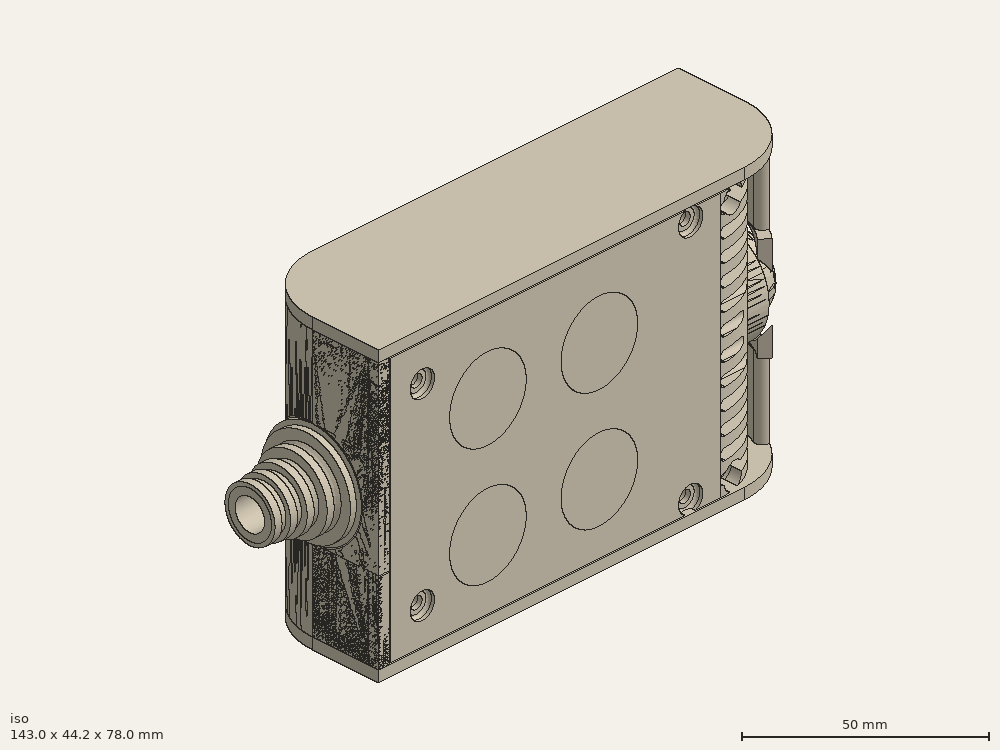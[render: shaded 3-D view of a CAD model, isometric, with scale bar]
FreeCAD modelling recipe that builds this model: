
FCSTD DOCUMENT  (FreeCAD 0.19R0.19.2)
Label: enclosure_142
License: All rights reserved
LicenseURL: http://en.wikipedia.org/wiki/All_rights_reserved
objects: Part::Feature×90, Part::Revolution×90, Part::MultiFuse×76, Sketcher::SketchObject×49, Part::Extrusion×37, Part::Cut×35, Part::Cylinder×34, Part::Fillet×27, Part::Box×22, App::MeasureDistance×4
note: 460 computed .brp shape members not serialized (recipe doc carries the construction recipe); baked Part::Feature solids carry a one-line shape summary decoded from their .brp

FEATURE [Sketcher::SketchObject] Sketch  label="topSketch"
  FullyConstrained = true
  sketch-geometry (20):
    g0: LineSegment StartX=5.21097e-06 StartY=3 StartZ=0 EndX=5.21097e-06 EndY=19 EndZ=0
    g1: ArcOfCircle CenterX=19 CenterY=19 CenterZ=0 NormalX=0 NormalY=0 NormalZ=1 AngleXU=0 Radius=19 StartAngle=1.5708 EndAngle=3.14159
    g2: ArcOfCircle CenterX=19 CenterY=19 CenterZ=0 NormalX=0 NormalY=0 NormalZ=1 AngleXU=0 Radius=16 StartAngle=1.5708 EndAngle=3.14159
    g3: LineSegment StartX=114 StartY=35 StartZ=0 EndX=19 EndY=35 EndZ=0
    g4: LineSegment StartX=5.21097e-06 StartY=3 StartZ=0 EndX=5.21097e-06 EndY=0 EndZ=0
    g5: LineSegment StartX=3 StartY=0 StartZ=0 EndX=5.21097e-06 EndY=0 EndZ=0
    g6: LineSegment StartX=3 StartY=19 StartZ=0 EndX=3 EndY=0 EndZ=0
    g7: LineSegment StartX=19 StartY=38 StartZ=0 EndX=124 EndY=38 EndZ=0
    g8: Circle CenterX=119 CenterY=35 CenterZ=0 NormalX=0 NormalY=0 NormalZ=1 AngleXU=0 Radius=1
    g9: Circle CenterX=121 CenterY=35 CenterZ=0 NormalX=0 NormalY=0 NormalZ=1 AngleXU=0 Radius=1
    g10: Circle CenterX=121 CenterY=33 CenterZ=0 NormalX=0 NormalY=0 NormalZ=1 AngleXU=0 Radius=1
    g11: BSplineCurve PolesCount=3 KnotsCount=2 Degree=2 IsPeriodic=0
    g12: GeomPoint X=119 Y=35 Z=0
    g13: GeomPoint X=121 Y=33 Z=0
    g14: LineSegment StartX=119 StartY=35 StartZ=0 EndX=114 EndY=35 EndZ=0
    g15: ArcOfCircle CenterX=105 CenterY=19 CenterZ=0 NormalX=0 NormalY=0 NormalZ=1 AngleXU=0 Radius=19 StartAngle=5.7297 EndAngle=6.28319
    g16: ArcOfCircle CenterX=105 CenterY=19 CenterZ=0 NormalX=0 NormalY=0 NormalZ=1 AngleXU=0 Radius=16 StartAngle=5.60905 EndAngle=6.28319
    g17: LineSegment StartX=121 StartY=33 StartZ=0 EndX=121 EndY=19 EndZ=0
    g18: LineSegment StartX=124 StartY=38 StartZ=0 EndX=124 EndY=19 EndZ=0
    g19: LineSegment StartX=117.5 StartY=9.01251 StartZ=0 EndX=121.163 EndY=9.0125 EndZ=0
  constraints (46):
    c: Vertical(g0)
    c: Block(g0)
    c: Coincident(g1,g0)
    c: Block(g1)
    c: Coincident(g2,g1)
    c: Block(g2)
    c: Coincident(g3,g2)
    c: Horizontal(g3)
    c: Tangent(g3,g2)
    c: Coincident(g4,g0)
    c: Distance(g4) = 3
    c: Vertical(g4)
    c: Coincident(g5,g4)
    c: Horizontal(g5)
    c: Coincident(g6,g2)
    c: Coincident(g6,g5)
    c: Vertical(g6)
    c: Horizontal(g7)
    c: Distance(g7) = 105
    c: Coincident(g7,g1)
    c: Block(g3)
    c: Weight(g8) = 1
    c: Equal(g8,g9)
    c: Equal(g8,g10)
    c: InternalAlignment(g8,g11)
    c: InternalAlignment(g9,g11)
    c: InternalAlignment(g10,g11)
    c: InternalAlignment(g12,g11)
    c: InternalAlignment(g13,g11)
    c: Block(g11)
    c: Coincident(g14,g11)
    c: Coincident(g14,g3)
    c: Horizontal(g14)
    c: Block(g15)
    c: Coincident(g16,g15)
    c: Block(g16)
    c: Coincident(g17,g11)
    c: Coincident(g17,g16)
    c: Vertical(g17)
    c: Distance(g17) = 14
    c: Coincident(g18,g7)
    c: Coincident(g18,g15)
    c: Vertical(g18)
    c: Distance(g18) = 19
    c: Coincident(g19,g16)
    c: Coincident(g19,g15)
FEATURE [Sketcher::SketchObject] Sketch001  label="bottomSketch"
  FullyConstrained = true
  sketch-geometry (32):
    g0: LineSegment StartX=3.3 StartY=-6.03275e-07 StartZ=0 EndX=98 EndY=-6.03275e-07 EndZ=0
    g1: ArcOfCircle CenterX=98 CenterY=19 CenterZ=0 NormalX=0 NormalY=0 NormalZ=1 AngleXU=0 Radius=19 StartAngle=4.71239 EndAngle=5.71103
    g2: LineSegment StartX=6.3 StartY=8 StartZ=0 EndX=3.3 EndY=8 EndZ=0
    g3: LineSegment StartX=3.3 StartY=8 StartZ=0 EndX=3.3 EndY=-6.03275e-07 EndZ=0
    g4: ArcOfCircle CenterX=8.3 CenterY=5 CenterZ=0 NormalX=0 NormalY=0 NormalZ=1 AngleXU=0 Radius=2 StartAngle=3.14159 EndAngle=4.71239
    g5: LineSegment StartX=6.3 StartY=8 StartZ=0 EndX=6.3 EndY=5 EndZ=0
    g6: ArcOfCircle CenterX=98 CenterY=19 CenterZ=0 NormalX=0 NormalY=0 NormalZ=1 AngleXU=0 Radius=12.7 StartAngle=4.71239 EndAngle=6.28319
    g7: LineSegment StartX=94.7 StartY=3 StartZ=0 EndX=8.3 EndY=3 EndZ=0
    g8-g12: Circle x5 (B-spline internal-alignment scaffolding for g13; pole/knot coordinates omitted)
    g13: BSplineCurve PolesCount=5 KnotsCount=3 Degree=3 IsPeriodic=0
    g14: GeomPoint X=98 Y=6.3 Z=0
    g15: GeomPoint X=96.3938 Y=4.71946 Z=0
    g16: GeomPoint X=94.7 Y=3 Z=0
    g17-g23: Circle x7 (B-spline internal-alignment scaffolding for g24; pole/knot coordinates omitted)
    g24: BSplineCurve PolesCount=7 KnotsCount=5 Degree=3 IsPeriodic=0
    g25-g29: GeomPoint x5 (B-spline internal-alignment scaffolding for g24; pole/knot coordinates omitted)
    g30: ArcOfCircle CenterX=98 CenterY=19 CenterZ=0 NormalX=0 NormalY=0 NormalZ=1 AngleXU=0 Radius=15.7 StartAngle=5.81226 EndAngle=6.28319
    g31: LineSegment StartX=110.7 StartY=19 StartZ=0 EndX=113.7 EndY=19 EndZ=0
  constraints (41):
    c: Horizontal(g0)
    c: Coincident(g1,g0)
    c: Block(g1)
    c: Horizontal(g2)
    c: Distance(g2) = 3
    c: Coincident(g3,g2)
    c: Vertical(g3)
    c: Coincident(g3,g0)
    c: Block(g4)
    c: Block(g2)
    c: Coincident(g5,g2)
    c: Coincident(g5,g4)
    c: Vertical(g5)
    c: Coincident(g6,g1)
    c: Block(g6)
    c: Coincident(g7,g4)
    c: Horizontal(g7)
    c: Block(g0)
    c: Block(g7)
    c: Block(g3)
    c: Coincident(g13,g6)
    c: Weight(g8) = 1
    c: Equal(g8, g9-g12) x4
    c: Coincident(g13,g7)
    c: InternalAlignment(g8-g12 -> g13) x5
    c: InternalAlignment(g14,g13)
    c: InternalAlignment(g15,g13)
    c: InternalAlignment(g16,g13)
    c: Block(g13)
    c: Weight(g17) = 1
    c: Equal(g17, g18-g23) x6
    c: Coincident(g24,g1)
    c: InternalAlignment(g17-g23 -> g24) x7
    c: InternalAlignment(g25-g29 -> g24) x5
    c: Block(g24)
    c: Coincident(g30,g24)
    c: Coincident(g31,g6)
    c: Coincident(g31,g30)
    c: Horizontal(g31)
    c: Block(g31)
    c: Block(g30)
FEATURE [Part::Extrusion] Extrude  label="top"
  Base = -> Sketch
  Dir = (0,0,1)
  DirMode = 2
  FaceMakerClass = Part::FaceMakerBullseye
  LengthFwd = 72
  LengthRev = 0
  Solid = true
  Symmetric = false
FEATURE [Part::Extrusion] Extrude001  label="bottom"
  Base = -> Sketch001
  Dir = (0,0,1)
  DirMode = 2
  FaceMakerClass = Part::FaceMakerBullseye
  LengthFwd = 71.4
  LengthRev = 0
  Placement = pos=(0,0,0.3) rot=(0,0,1;0rad)
  Solid = true
  Symmetric = false
FEATURE [Sketcher::SketchObject] Sketch002  label="topSketch001"
  FullyConstrained = true
  sketch-geometry (6):
    g0: ArcOfCircle CenterX=19 CenterY=19 CenterZ=0 NormalX=0 NormalY=0 NormalZ=1 AngleXU=0 Radius=19 StartAngle=1.5708 EndAngle=3.14159
    g1: LineSegment StartX=5.22862e-06 StartY=19 StartZ=0 EndX=5.22862e-06 EndY=1.19904e-11 EndZ=0
    g2: LineSegment StartX=19 StartY=38 StartZ=0 EndX=124 EndY=38 EndZ=0
    g3: LineSegment StartX=5.22862e-06 StartY=1.19904e-11 StartZ=0 EndX=105 EndY=1.19904e-11 EndZ=0
    g4: ArcOfCircle CenterX=105 CenterY=19 CenterZ=0 NormalX=0 NormalY=0 NormalZ=1 AngleXU=0 Radius=19 StartAngle=4.71239 EndAngle=6.28319
    g5: LineSegment StartX=124 StartY=38 StartZ=0 EndX=124 EndY=19 EndZ=0
  constraints (16):
    c: Block(g0)
    c: Coincident(g1,g0)
    c: Vertical(g1)
    c: Horizontal(g2)
    c: Distance(g2) = 105
    c: Coincident(g2,g0)
    c: Distance(g1) = 19
    c: Coincident(g3,g1)
    c: Horizontal(g3)
    c: Distance(g3) = 105
    c: Block(g4)
    c: Coincident(g4,g3)
    c: Coincident(g5,g2)
    c: Coincident(g5,g4)
    c: Vertical(g5)
    c: Distance(g5) = 19
FEATURE [Part::Extrusion] Extrude002  label="sideA"
  Base = -> Sketch002
  Dir = (0,0,1)
  DirMode = 2
  FaceMakerClass = Part::FaceMakerBullseye
  LengthFwd = 3
  LengthRev = 0
  Placement = pos=(0,0,-3) rot=(0,0,1;0rad)
  Solid = true
  Symmetric = false
FEATURE [Sketcher::SketchObject] Sketch003  label="topSketch002"
  FullyConstrained = true
  sketch-geometry (6):
    g0: LineSegment StartX=19 StartY=38 StartZ=0 EndX=117 EndY=38 EndZ=0
    g1: ArcOfCircle CenterX=19 CenterY=19 CenterZ=0 NormalX=0 NormalY=0 NormalZ=1 AngleXU=0 Radius=19 StartAngle=1.5708 EndAngle=3.14159
    g2: LineSegment StartX=117 StartY=38 StartZ=0 EndX=117 EndY=19 EndZ=0
    g3: LineSegment StartX=98 StartY=1.0161e-12 StartZ=0 EndX=5.22862e-06 EndY=1.0161e-12 EndZ=0
    g4: LineSegment StartX=5.22862e-06 StartY=19 StartZ=0 EndX=5.22862e-06 EndY=1.0161e-12 EndZ=0
    g5: ArcOfCircle CenterX=98 CenterY=19 CenterZ=0 NormalX=0 NormalY=0 NormalZ=1 AngleXU=0 Radius=19 StartAngle=4.71239 EndAngle=6.28319
  constraints (16):
    c: Horizontal(g0)
    c: Distance(g0) = 98
    c: Coincident(g1,g0)
    c: Block(g1)
    c: Coincident(g2,g0)
    c: Vertical(g2)
    c: Distance(g2) = 19
    c: Horizontal(g3)
    c: Coincident(g4,g1)
    c: Vertical(g4)
    c: Coincident(g3,g4)
    c: Block(g3)
    c: Coincident(g5,g2)
    c: Coincident(g5,g3)
    c: Block(g0)
    c: Block(g5)
FEATURE [Sketcher::SketchObject] Sketch004
  FullyConstrained = true
  MapMode = 3
  Placement = pos=(0,0,0) rot=(1,0,0;1.5708rad)
  Support = -> [Extrude]
  sketch-geometry (8):
    g0: Circle CenterX=80.351 CenterY=-67.6202 CenterZ=0 NormalX=0 NormalY=0 NormalZ=1 AngleXU=0 Radius=2
    g1: Circle CenterX=80.351 CenterY=-67.6202 CenterZ=0 NormalX=0 NormalY=0 NormalZ=1 AngleXU=0 Radius=3
    g2: Circle CenterX=80.351 CenterY=-4.92017 CenterZ=0 NormalX=0 NormalY=0 NormalZ=1 AngleXU=0 Radius=2
    g3: Circle CenterX=80.351 CenterY=-4.92017 CenterZ=0 NormalX=0 NormalY=0 NormalZ=1 AngleXU=0 Radius=3
    g4: Circle CenterX=23.851 CenterY=-4.92017 CenterZ=0 NormalX=0 NormalY=0 NormalZ=1 AngleXU=0 Radius=2
    g5: Circle CenterX=23.851 CenterY=-4.92017 CenterZ=0 NormalX=0 NormalY=0 NormalZ=1 AngleXU=0 Radius=3
    g6: Circle CenterX=23.851 CenterY=-67.6202 CenterZ=0 NormalX=0 NormalY=0 NormalZ=1 AngleXU=0 Radius=2
    g7: Circle CenterX=23.851 CenterY=-67.6202 CenterZ=0 NormalX=0 NormalY=0 NormalZ=1 AngleXU=0 Radius=3
  constraints (8):
    c: Block(g3)
    c: Block(g2)
    c: Block(g1)
    c: Block(g0)
    c: Block(g6)
    c: Block(g7)
    c: Block(g4)
    c: Block(g5)
FEATURE [Part::Extrusion] Extrude004
  Base = -> Sketch004
  Dir = (0,-1,2e-16)
  DirMode = 2
  FaceMakerClass = Part::FaceMakerBullseye
  LengthFwd = 6
  LengthRev = 0
  Placement = pos=(0,9,0) rot=(0,0,1;0rad)
  Solid = true
  Symmetric = false
FEATURE [Sketcher::SketchObject] Sketch005
  FullyConstrained = true
  MapMode = 3
  Placement = pos=(0,0,0) rot=(1,0,0;1.5708rad)
  Support = -> [Extrude]
  sketch-geometry (8):
    g0: Circle CenterX=80.351 CenterY=-67.6202 CenterZ=0 NormalX=0 NormalY=0 NormalZ=1 AngleXU=0 Radius=3
    g1: Circle CenterX=80.351 CenterY=-4.92017 CenterZ=0 NormalX=0 NormalY=0 NormalZ=1 AngleXU=0 Radius=3
    g2: Circle CenterX=23.851 CenterY=-4.92017 CenterZ=0 NormalX=0 NormalY=0 NormalZ=1 AngleXU=0 Radius=3
    g3: Circle CenterX=23.851 CenterY=-67.6202 CenterZ=0 NormalX=0 NormalY=0 NormalZ=1 AngleXU=0 Radius=3
    g4: Circle CenterX=23.851 CenterY=-67.6202 CenterZ=0 NormalX=0 NormalY=0 NormalZ=1 AngleXU=0 Radius=5
    g5: Circle CenterX=80.351 CenterY=-67.6202 CenterZ=0 NormalX=0 NormalY=0 NormalZ=1 AngleXU=0 Radius=5
    g6: Circle CenterX=23.851 CenterY=-4.92017 CenterZ=0 NormalX=0 NormalY=0 NormalZ=1 AngleXU=0 Radius=5
    g7: Circle CenterX=80.351 CenterY=-4.92017 CenterZ=0 NormalX=0 NormalY=0 NormalZ=1 AngleXU=0 Radius=5
  constraints (8):
    c: Block(g1)
    c: Block(g0)
    c: Block(g3)
    c: Block(g2)
    c: Block(g5)
    c: Block(g4)
    c: Block(g6)
    c: Block(g7)
FEATURE [Part::Extrusion] Extrude005
  Base = -> Sketch005
  Dir = (0,-1,2e-16)
  DirMode = 2
  FaceMakerClass = Part::FaceMakerBullseye
  LengthFwd = 2
  LengthRev = 0
  Solid = true
  Symmetric = false
FEATURE [Sketcher::SketchObject] Sketch006
  FullyConstrained = true
  MapMode = 3
  Placement = pos=(0,0,0) rot=(1,0,0;1.5708rad)
  sketch-geometry (8):
    g0: Circle CenterX=80.351 CenterY=-67.6202 CenterZ=0 NormalX=0 NormalY=0 NormalZ=1 AngleXU=0 Radius=3
    g1: Circle CenterX=80.351 CenterY=-4.92017 CenterZ=0 NormalX=0 NormalY=0 NormalZ=1 AngleXU=0 Radius=3
    g2: Circle CenterX=23.851 CenterY=-4.92017 CenterZ=0 NormalX=0 NormalY=0 NormalZ=1 AngleXU=0 Radius=3
    g3: Circle CenterX=23.851 CenterY=-67.6202 CenterZ=0 NormalX=0 NormalY=0 NormalZ=1 AngleXU=0 Radius=3
    g4: Circle CenterX=23.851 CenterY=-67.6202 CenterZ=0 NormalX=0 NormalY=0 NormalZ=1 AngleXU=0 Radius=5
    g5: Circle CenterX=80.351 CenterY=-67.6202 CenterZ=0 NormalX=0 NormalY=0 NormalZ=1 AngleXU=0 Radius=5
    g6: Circle CenterX=23.851 CenterY=-4.92017 CenterZ=0 NormalX=0 NormalY=0 NormalZ=1 AngleXU=0 Radius=5
    g7: Circle CenterX=80.351 CenterY=-4.92017 CenterZ=0 NormalX=0 NormalY=0 NormalZ=1 AngleXU=0 Radius=5
  constraints (8):
    c: Block(g1)
    c: Block(g0)
    c: Block(g3)
    c: Block(g2)
    c: Block(g5)
    c: Block(g4)
    c: Block(g6)
    c: Block(g7)
FEATURE [Part::Extrusion] Extrude007
  Base = -> Sketch006
  Dir = (0,-1,2e-16)
  DirMode = 2
  FaceMakerClass = Part::FaceMakerBullseye
  LengthFwd = 2
  LengthRev = 0
  Solid = true
  Symmetric = false
FEATURE [Part::Fillet] Fillet
  Base = -> Extrude007
  Edges = 4 edges r=1.99: [Edge6,Edge12,Edge18,Edge24]
FEATURE [Part::Cut] Cut
  Base = -> Extrude005
  Placement = pos=(0,5,0) rot=(0,0,1;0rad)
  Tool = -> Fillet
FEATURE [Part::MultiFuse] Fusion  label="pCBScrews"
  Placement = pos=(-2.5,0,72.3) rot=(0,0,1;0rad)
  Shapes = -> [Extrude004,Cut]
FEATURE [App::MeasureDistance] Distance  label="Distance: 0.69 mm"
  Distance = 0.685967
  P1 = (24.0138,2.9647,0.3)
  P2 = (23.8901,3,-0.373787)
FEATURE [App::MeasureDistance] Distance001  label="Distance: 0.53 mm"
  Distance = 0.533607
  P1 = (80.2939,3,72.2334)
  P2 = (80.281,2.99661,71.7)
FEATURE [Part::Fillet] Fillet001
  Base = -> Extrude001
  Edges = 1 edges r=2.4: [Edge17]
FEATURE [Part::Fillet] Fillet002  label="bottom001"
  Base = -> Fillet001
  Edges = 1 edges r=2.4: [Edge36]
FEATURE [Part::Fillet] Fillet003  label="top001"
  Base = -> Extrude
  Edges = 1 edges r=2: [Edge1]
FEATURE [Sketcher::SketchObject] Sketch007
  FullyConstrained = true
  sketch-geometry (16):
    g0: LineSegment StartX=4 StartY=0 StartZ=0 EndX=4 EndY=2.4 EndZ=0
    g1: LineSegment StartX=4 StartY=2.4 StartZ=0 EndX=7 EndY=2.4 EndZ=0
    g2: LineSegment StartX=4 StartY=0 StartZ=0 EndX=5.7 EndY=0 EndZ=0
    g3: LineSegment StartX=5.7 StartY=0 StartZ=0 EndX=5.7 EndY=-5.6 EndZ=0
    g4-g8: Circle x5 (B-spline internal-alignment scaffolding for g9; pole/knot coordinates omitted)
    g9: BSplineCurve PolesCount=5 KnotsCount=3 Degree=3 IsPeriodic=0
    g10: GeomPoint X=7 Y=2.4 Z=0
    g11: GeomPoint X=10.4582 Y=-1.55472 Z=0
    g12: GeomPoint X=14 Y=-5.6 Z=0
    g13: LineSegment StartX=14 StartY=-5.6 StartZ=0 EndX=14 EndY=-14.1 EndZ=0
    g14: LineSegment StartX=14 StartY=-14.1 StartZ=0 EndX=6.5 EndY=-14.1 EndZ=0
    g15: LineSegment StartX=5.7 StartY=-5.6 StartZ=0 EndX=6.5 EndY=-14.1 EndZ=0
  constraints (28):
    c: Distance(g0) = 2.4
    c: Vertical(g0)
    c: Block(g0)
    c: Coincident(g1,g0)
    c: Horizontal(g1)
    c: Distance(g1) = 3
    c: Coincident(g2,g0)
    c: Horizontal(g2)
    c: Distance(g2) = 1.7
    c: Coincident(g3,g2)
    c: Vertical(g3)
    c: Distance(g3) = 5.6
    c: Coincident(g9,g1)
    c: Weight(g4) = 1
    c: Equal(g4, g5-g8) x4
    c: InternalAlignment(g4-g8 -> g9) x5
    c: InternalAlignment(g10,g9)
    c: InternalAlignment(g11,g9)
    c: InternalAlignment(g12,g9)
    c: Block(g9)
    c: Coincident(g13,g9)
    c: Vertical(g13)
    c: Distance(g13) = 8.5
    c: Coincident(g14,g13)
    c: Horizontal(g14)
    c: Distance(g14) = 7.5
    c: Coincident(g15,g3)
    c: Coincident(g15,g14)
FEATURE [Part::Feature] Face
  shape: bbox 10 x 16.5 x 2e-07 mm, 1 faces, 0 solids (baked)
FEATURE [Part::Revolution] Revolve  label="plugHousing"
  Angle = 360
  Axis = (0,1,0)
  Base = (0,0,0)
  FaceMakerClass = Part::FaceMakerBullseye
  Placement = pos=(0,0,36.15) rot=(0,0,1;0rad)
  Solid = false
  Source = -> Face
  Symmetric = false
FEATURE [Part::Feature] Face001
  shape: bbox 10 x 16.5 x 2e-07 mm, 1 faces, 0 solids (baked)
FEATURE [Part::Revolution] Revolve001  label="plugHousing001"
  Angle = 360
  Axis = (0,1,0)
  Base = (0,0,0)
  FaceMakerClass = Part::FaceMakerBullseye
  Placement = pos=(0,0,36.15) rot=(0,0,1;0rad)
  Solid = false
  Source = -> Face001
  Symmetric = false
FEATURE [Part::MultiFuse] Fusion001  label="plugHousing002"
  Placement = pos=(0,0,0) rot=(0,0,1;1.5708rad)
  Shapes = -> [Revolve001,Revolve]
FEATURE [Part::Feature] Face002
  shape: bbox 10 x 16.5 x 2e-07 mm, 1 faces, 0 solids (baked)
FEATURE [Part::Revolution] Revolve003  label="plugHousing005"
  Angle = 360
  Axis = (0,1,0)
  Base = (0,0,0)
  FaceMakerClass = Part::FaceMakerBullseye
  Placement = pos=(0,0,36.15) rot=(0,0,1;0rad)
  Solid = false
  Source = -> Face002
  Symmetric = false
FEATURE [Part::Feature] Face003
  shape: bbox 10 x 16.5 x 2e-07 mm, 1 faces, 0 solids (baked)
FEATURE [Part::Revolution] Revolve002  label="plugHousing003"
  Angle = 360
  Axis = (0,1,0)
  Base = (0,0,0)
  FaceMakerClass = Part::FaceMakerBullseye
  Placement = pos=(0,0,36.15) rot=(0,0,1;0rad)
  Solid = false
  Source = -> Face003
  Symmetric = false
FEATURE [Part::MultiFuse] Fusion002  label="plugHousing004"
  Placement = pos=(0,0,0) rot=(0,0,1;1.5708rad)
  Shapes = -> [Revolve002,Revolve003]
FEATURE [Part::MultiFuse] Fusion003  label="plugHousing006"
  Placement = pos=(0,19,0) rot=(0,0,1;3.14159rad)
  Shapes = -> [Fusion002,Fusion001]
FEATURE [Part::Feature] Face004
  shape: bbox 10 x 16.5 x 2e-07 mm, 1 faces, 0 solids (baked)
FEATURE [Part::Revolution] Revolve006  label="plugHousing010"
  Angle = 360
  Axis = (0,1,0)
  Base = (0,0,0)
  FaceMakerClass = Part::FaceMakerBullseye
  Placement = pos=(0,0,36.15) rot=(0,0,1;0rad)
  Solid = false
  Source = -> Face004
  Symmetric = false
FEATURE [Part::Feature] Face005
  shape: bbox 10 x 16.5 x 2e-07 mm, 1 faces, 0 solids (baked)
FEATURE [Part::Revolution] Revolve007  label="plugHousing011"
  Angle = 360
  Axis = (0,1,0)
  Base = (0,0,0)
  FaceMakerClass = Part::FaceMakerBullseye
  Placement = pos=(0,0,36.15) rot=(0,0,1;0rad)
  Solid = false
  Source = -> Face005
  Symmetric = false
FEATURE [Part::Feature] Face006
  shape: bbox 10 x 16.5 x 2e-07 mm, 1 faces, 0 solids (baked)
FEATURE [Part::Revolution] Revolve004  label="plugHousing007"
  Angle = 360
  Axis = (0,1,0)
  Base = (0,0,0)
  FaceMakerClass = Part::FaceMakerBullseye
  Placement = pos=(0,0,36.15) rot=(0,0,1;0rad)
  Solid = false
  Source = -> Face006
  Symmetric = false
FEATURE [Part::MultiFuse] Fusion004  label="plugHousing009"
  Placement = pos=(0,0,0) rot=(0,0,1;1.5708rad)
  Shapes = -> [Revolve004,Revolve007]
FEATURE [Part::Feature] Face007
  shape: bbox 10 x 16.5 x 2e-07 mm, 1 faces, 0 solids (baked)
FEATURE [Part::Revolution] Revolve005  label="plugHousing008"
  Angle = 360
  Axis = (0,1,0)
  Base = (0,0,0)
  FaceMakerClass = Part::FaceMakerBullseye
  Placement = pos=(0,0,36.15) rot=(0,0,1;0rad)
  Solid = false
  Source = -> Face007
  Symmetric = false
FEATURE [Part::MultiFuse] Fusion005  label="plugHousing012"
  Placement = pos=(0,0,0) rot=(0,0,1;1.5708rad)
  Shapes = -> [Revolve006,Revolve005]
FEATURE [Part::MultiFuse] Fusion006  label="plugHousing013"
  Placement = pos=(0,19,0) rot=(0,0,1;3.14159rad)
  Shapes = -> [Fusion005,Fusion004]
FEATURE [Part::MultiFuse] Fusion007  label="plugHousing014"
  Placement = pos=(122.621,0,-0.15) rot=(0,0,1;0rad)
  Shapes = -> [Fusion003,Fusion006]
FEATURE [Part::Cylinder] Cylinder002
  Angle = 360
  AttacherType = Attacher::AttachEngine3D
  Height = 20
  Placement = pos=(0,0,36.15) rot=(0,0,1;0rad)
  Radius = 4
FEATURE [Part::Cylinder] Cylinder003
  Angle = 360
  AttacherType = Attacher::AttachEngine3D
  Height = 10
  Placement = pos=(0,0,36.15) rot=(0,0,1;0rad)
  Radius = 4
FEATURE [Part::MultiFuse] Fusion009  label="removeToCreateHoleForPlugHousing"
  Placement = pos=(70,19,36.15) rot=(0,1,0;1.5708rad)
  Shapes = -> [Cylinder002,Cylinder003]
FEATURE [Part::Cylinder] Cylinder004
  Angle = 360
  AttacherType = Attacher::AttachEngine3D
  Height = 20
  Placement = pos=(0,0,36.15) rot=(0,0,1;0rad)
  Radius = 4
FEATURE [Part::Cylinder] Cylinder005
  Angle = 360
  AttacherType = Attacher::AttachEngine3D
  Height = 10
  Placement = pos=(0,0,36.15) rot=(0,0,1;0rad)
  Radius = 4
FEATURE [Part::MultiFuse] Fusion010  label="removeToCreateHoleForPlugHousing001"
  Placement = pos=(70,19,36.15) rot=(0,1,0;1.5708rad)
  Shapes = -> [Cylinder004,Cylinder005]
FEATURE [Part::Cut] Cut001
  Base = -> Fillet003
  Tool = -> Fusion010
FEATURE [Part::Cut] Cut002  label="Bottom"
  Base = -> Fillet002
  Tool = -> Fusion009
FEATURE [Part::Feature] Face008
  shape: bbox 10 x 16.5 x 2e-07 mm, 1 faces, 0 solids (baked)
FEATURE [Part::Revolution] Revolve011  label="plugHousing021"
  Angle = 360
  Axis = (0,1,0)
  Base = (0,0,0)
  FaceMakerClass = Part::FaceMakerBullseye
  Placement = pos=(0,0,36.15) rot=(0,0,1;0rad)
  Solid = false
  Source = -> Face008
  Symmetric = false
FEATURE [Part::Feature] Face009
  shape: bbox 10 x 16.5 x 2e-07 mm, 1 faces, 0 solids (baked)
FEATURE [Part::Revolution] Revolve012  label="plugHousing022"
  Angle = 360
  Axis = (0,1,0)
  Base = (0,0,0)
  FaceMakerClass = Part::FaceMakerBullseye
  Placement = pos=(0,0,36.15) rot=(0,0,1;0rad)
  Solid = false
  Source = -> Face009
  Symmetric = false
FEATURE [Part::Feature] Face010 .. Face013  x4 (patterned run collapsed; names and placements below)
  shape: bbox 10 x 16.5 x 2e-07 mm, 1 faces, 0 solids (baked)
FEATURE [Part::Revolution] Revolve015  label="plugHousing027"
  Angle = 360
  Axis = (0,1,0)
  Base = (0,0,0)
  FaceMakerClass = Part::FaceMakerBullseye
  Placement = pos=(0,0,36.15) rot=(0,0,1;0rad)
  Solid = false
  Source = -> Face013
  Symmetric = false
FEATURE [Part::Feature] Face014
  shape: bbox 10 x 16.5 x 2e-07 mm, 1 faces, 0 solids (baked)
FEATURE [Part::Feature] Face015
  shape: bbox 10 x 16.5 x 2e-07 mm, 1 faces, 0 solids (baked)
FEATURE [Part::Feature] Face016
  shape: bbox 10 x 16.5 x 2e-07 mm, 1 faces, 0 solids (baked)
FEATURE [Part::Revolution] Revolve019  label="plugHousing033"
  Angle = 360
  Axis = (0,1,0)
  Base = (0,0,0)
  FaceMakerClass = Part::FaceMakerBullseye
  Placement = pos=(0,0,36.15) rot=(0,0,1;0rad)
  Solid = false
  Source = -> Face016
  Symmetric = false
FEATURE [Part::Feature] Face017
  shape: bbox 10 x 16.5 x 2e-07 mm, 1 faces, 0 solids (baked)
FEATURE [Part::Revolution] Revolve020  label="plugHousing034"
  Angle = 360
  Axis = (0,1,0)
  Base = (0,0,0)
  FaceMakerClass = Part::FaceMakerBullseye
  Placement = pos=(0,0,36.15) rot=(0,0,1;0rad)
  Solid = false
  Source = -> Face017
  Symmetric = false
FEATURE [Part::Feature] Face018
  shape: bbox 10 x 16.5 x 2e-07 mm, 1 faces, 0 solids (baked)
FEATURE [Part::Revolution] Revolve016  label="plugHousing030"
  Angle = 360
  Axis = (0,1,0)
  Base = (0,0,0)
  FaceMakerClass = Part::FaceMakerBullseye
  Placement = pos=(0,0,36.15) rot=(0,0,1;0rad)
  Solid = false
  Source = -> Face018
  Symmetric = false
FEATURE [Part::MultiFuse] Fusion020  label="plugHousing038"
  Placement = pos=(0,0,0) rot=(0,0,1;1.5708rad)
  Shapes = -> [Revolve016,Revolve020]
FEATURE [Part::Feature] Face019
  shape: bbox 10 x 16.5 x 2e-07 mm, 1 faces, 0 solids (baked)
FEATURE [Part::Feature] Face020
  shape: bbox 10 x 16.5 x 2e-07 mm, 1 faces, 0 solids (baked)
FEATURE [Part::Revolution] Revolve017  label="plugHousing031"
  Angle = 360
  Axis = (0,1,0)
  Base = (0,0,0)
  FaceMakerClass = Part::FaceMakerBullseye
  Placement = pos=(0,0,36.15) rot=(0,0,1;0rad)
  Solid = false
  Source = -> Face020
  Symmetric = false
FEATURE [Part::MultiFuse] Fusion021  label="plugHousing039"
  Placement = pos=(0,0,0) rot=(0,0,1;1.5708rad)
  Shapes = -> [Revolve019,Revolve017]
FEATURE [Part::MultiFuse] Fusion023  label="plugHousing041"
  Placement = pos=(0,19,0) rot=(0,0,1;3.14159rad)
  Shapes = -> [Fusion021,Fusion020]
FEATURE [Part::Revolution] Revolve022  label="plugHousing043"
  Angle = 360
  Axis = (0,1,0)
  Base = (0,0,0)
  FaceMakerClass = Part::FaceMakerBullseye
  Placement = pos=(0,0,36.15) rot=(0,0,1;0rad)
  Solid = false
  Source = -> Face019
  Symmetric = false
FEATURE [Part::Feature] Face021
  shape: bbox 10 x 16.5 x 2e-07 mm, 1 faces, 0 solids (baked)
FEATURE [Part::Revolution] Revolve023  label="plugHousing044"
  Angle = 360
  Axis = (0,1,0)
  Base = (0,0,0)
  FaceMakerClass = Part::FaceMakerBullseye
  Placement = pos=(0,0,36.15) rot=(0,0,1;0rad)
  Solid = false
  Source = -> Face021
  Symmetric = false
FEATURE [Part::Feature] Face022
  shape: bbox 10 x 16.5 x 2e-07 mm, 1 faces, 0 solids (baked)
FEATURE [Part::Revolution] Revolve018  label="plugHousing032"
  Angle = 360
  Axis = (0,1,0)
  Base = (0,0,0)
  FaceMakerClass = Part::FaceMakerBullseye
  Placement = pos=(0,0,36.15) rot=(0,0,1;0rad)
  Solid = false
  Source = -> Face022
  Symmetric = false
FEATURE [Part::MultiFuse] Fusion022  label="plugHousing040"
  Placement = pos=(0,0,0) rot=(0,0,1;1.5708rad)
  Shapes = -> [Revolve018,Revolve023]
FEATURE [Part::Feature] Face023
  shape: bbox 10 x 16.5 x 2e-07 mm, 1 faces, 0 solids (baked)
FEATURE [Part::Revolution] Revolve021  label="plugHousing035"
  Angle = 360
  Axis = (0,1,0)
  Base = (0,0,0)
  FaceMakerClass = Part::FaceMakerBullseye
  Placement = pos=(0,0,36.15) rot=(0,0,1;0rad)
  Solid = false
  Source = -> Face023
  Symmetric = false
FEATURE [Part::MultiFuse] Fusion018  label="plugHousing036"
  Placement = pos=(0,0,0) rot=(0,0,1;1.5708rad)
  Shapes = -> [Revolve022,Revolve021]
FEATURE [Part::MultiFuse] Fusion019  label="plugHousing037"
  Placement = pos=(0,19,0) rot=(0,0,1;3.14159rad)
  Shapes = -> [Fusion018,Fusion022]
FEATURE [Part::MultiFuse] Fusion024  label="plugHousing042"
  Placement = pos=(122.621,0,-0.15) rot=(0,0,1;0rad)
  Shapes = -> [Fusion023,Fusion019]
FEATURE [Part::Cylinder] Cylinder006
  Angle = 360
  AttacherType = Attacher::AttachEngine3D
  Height = 20
  Placement = pos=(0,0,36.15) rot=(0,0,1;0rad)
  Radius = 14.3
FEATURE [Part::Cylinder] Cylinder007
  Angle = 360
  AttacherType = Attacher::AttachEngine3D
  Height = 10
  Placement = pos=(0,0,36.15) rot=(0,0,1;0rad)
  Radius = 4
FEATURE [Part::MultiFuse] Fusion026  label="removeToCreteHoleForPlugHousing"
  Placement = pos=(70,19,36) rot=(0,1,0;1.5708rad)
  Shapes = -> [Cylinder006,Cylinder007]
FEATURE [Part::Box] Box001  label="Cube001"
  AttacherType = Attacher::AttachEngine3D
  Height = 28
  Length = 3
  Placement = pos=(110.7,19,22) rot=(0,0,1;0rad)
  Width = 15.7
FEATURE [Part::Cut] Cut003  label="top002"
  Base = -> Cut001
  Tool = -> Fusion007
FEATURE [Part::Revolution] Revolve008  label="plugHousing015"
  Angle = 360
  Axis = (0,1,0)
  Base = (0,0,0)
  FaceMakerClass = Part::FaceMakerBullseye
  Placement = pos=(0,0,36.15) rot=(0,0,1;0rad)
  Solid = false
  Source = -> Face010
  Symmetric = false
FEATURE [Part::MultiFuse] Fusion013  label="plugHousing020"
  Placement = pos=(0,0,0) rot=(0,0,1;1.5708rad)
  Shapes = -> [Revolve008,Revolve012]
FEATURE [Part::Cut] Cut004  label="top003"
  Base = -> Cut003
  Placement = pos=(1,0,0) rot=(0,0,1;0rad)
  Tool = -> Fusion026
FEATURE [Part::Cylinder] Cylinder008
  Angle = 360
  AttacherType = Attacher::AttachEngine3D
  Height = 20
  Placement = pos=(0,0,36.15) rot=(0,0,1;0rad)
  Radius = 10.3
FEATURE [Part::Cylinder] Cylinder009
  Angle = 360
  AttacherType = Attacher::AttachEngine3D
  Height = 10
  Placement = pos=(0,0,36.15) rot=(0,0,1;0rad)
  Radius = 4
FEATURE [Part::MultiFuse] Fusion027  label="removeToCreteHoleForPlugHousing001"
  Placement = pos=(70,19,36) rot=(0,1,0;1.5708rad)
  Shapes = -> [Cylinder008,Cylinder009]
FEATURE [Part::Cut] Cut005  label="plugHousingTab"
  Base = -> Box001
  Tool = -> Fusion027
FEATURE [Part::MultiFuse] Fusion028  label="plugHousing045"
  Shapes = -> [Fusion024,Cut005]
FEATURE [Part::Box] Box002  label="Cube002"
  AttacherType = Attacher::AttachEngine3D
  Height = 28.8
  Length = 3
  Placement = pos=(107.3,28,21.6) rot=(0,0,1;0rad)
  Width = 7
FEATURE [Part::Box] Box003  label="Cube003"
  AttacherType = Attacher::AttachEngine3D
  Height = 3
  Length = 6.4
  Placement = pos=(107.3,28,18.6) rot=(0,0,1;0rad)
  Width = 7
FEATURE [Part::Box] Box004  label="Cube004"
  AttacherType = Attacher::AttachEngine3D
  Height = 3
  Length = 6.4
  Placement = pos=(107.3,28,50.4) rot=(0,0,1;0rad)
  Width = 7
FEATURE [Part::MultiFuse] Fusion029  label="plugHousingBracketHolder"
  Shapes = -> [Box004,Box002,Box003]
FEATURE [Part::Cylinder] Cylinder010
  Angle = 360
  AttacherType = Attacher::AttachEngine3D
  Height = 20
  Placement = pos=(0,0,36.15) rot=(0,0,1;0rad)
  Radius = 14.3
FEATURE [Part::Cylinder] Cylinder011
  Angle = 360
  AttacherType = Attacher::AttachEngine3D
  Height = 10
  Placement = pos=(0,0,36.15) rot=(0,0,1;0rad)
  Radius = 4
FEATURE [Part::MultiFuse] Fusion030  label="removeToCreteHoleForPlugHousing002"
  Placement = pos=(70,19,36) rot=(0,1,0;1.5708rad)
  Shapes = -> [Cylinder010,Cylinder011]
FEATURE [Part::Cut] Cut006  label="plugHousingBracketHolder001"
  Base = -> Fusion029
  Tool = -> Fusion030
FEATURE [Part::Cylinder] Cylinder012
  Angle = 360
  AttacherType = Attacher::AttachEngine3D
  Height = 20
  Placement = pos=(0,0,36.15) rot=(0,0,1;0rad)
  Radius = 7
FEATURE [Part::Cylinder] Cylinder013
  Angle = 360
  AttacherType = Attacher::AttachEngine3D
  Height = 10
  Placement = pos=(0,0,36.15) rot=(0,0,1;0rad)
  Radius = 4
FEATURE [Part::MultiFuse] Fusion032  label="removeToCreteHoleForPlugHousing003"
  Placement = pos=(70,19,36) rot=(0,1,0;1.5708rad)
  Shapes = -> [Cylinder012,Cylinder013]
FEATURE [Part::Cut] Cut007  label="bottom002"
  Base = -> Cut002
  Tool = -> Fusion032
FEATURE [Sketcher::SketchObject] Sketch008
  FullyConstrained = true
  sketch-geometry (54):
    g0: LineSegment StartX=-4.2 StartY=0 StartZ=0 EndX=-6.2 EndY=0 EndZ=0
    g1: LineSegment StartX=-14 StartY=-18 StartZ=0 EndX=-14 EndY=-26.5 EndZ=0
    g2: LineSegment StartX=-4.2 StartY=0 StartZ=0 EndX=-4.2 EndY=-13.4877 EndZ=0
    g3: Circle CenterX=-4.2 CenterY=-13.4877 CenterZ=0 NormalX=0 NormalY=0 NormalZ=1 AngleXU=0 Radius=1
    g4: Circle CenterX=-4.2 CenterY=-26.5 CenterZ=0 NormalX=0 NormalY=0 NormalZ=1 AngleXU=0 Radius=1
    g5: Circle CenterX=-8.2 CenterY=-26.5 CenterZ=0 NormalX=0 NormalY=0 NormalZ=1 AngleXU=0 Radius=1
    g6: BSplineCurve PolesCount=3 KnotsCount=2 Degree=2 IsPeriodic=0
    g7: GeomPoint X=-4.2 Y=-13.4877 Z=0
    g8: GeomPoint X=-8.2 Y=-26.5 Z=0
    g9: LineSegment StartX=-14 StartY=-26.5 StartZ=0 EndX=-8.2 EndY=-26.5 EndZ=0
    g10: LineSegment StartX=-10.15 StartY=-12 StartZ=0 EndX=-10.15 EndY=-14 EndZ=0
    g11: LineSegment StartX=-12.8401 StartY=-16 StartZ=0 EndX=-10.1571 EndY=-16 EndZ=0
    g12: LineSegment StartX=-10.15 StartY=-14 StartZ=0 EndX=-8.70761 EndY=-14 EndZ=0
    g13: LineSegment StartX=-12.8401 StartY=-16 StartZ=0 EndX=-12.8401 EndY=-17.6958 EndZ=0
    g14: LineSegment StartX=-10.15 StartY=-12 StartZ=0 EndX=-7.79258 EndY=-12 EndZ=0
    g15: Circle CenterX=-6.2215 CenterY=-2 CenterZ=0 NormalX=0 NormalY=0 NormalZ=1 AngleXU=0 Radius=1
    g16: Circle CenterX=-6.22762 CenterY=-2.58724 CenterZ=0 NormalX=0 NormalY=0 NormalZ=1 AngleXU=0 Radius=1
    g17: Circle CenterX=-6.32538 CenterY=-4 CenterZ=0 NormalX=0 NormalY=0 NormalZ=1 AngleXU=0 Radius=1
    g18: BSplineCurve PolesCount=3 KnotsCount=2 Degree=2 IsPeriodic=0
    g19: GeomPoint X=-6.2215 Y=-2 Z=0
    g20: GeomPoint X=-6.32538 Y=-4 Z=0
    g21: Circle CenterX=-6.48644 CenterY=-5.99526 CenterZ=0 NormalX=0 NormalY=0 NormalZ=1 AngleXU=0 Radius=1
    g22: Circle CenterX=-6.58486 CenterY=-6.99526 CenterZ=0 NormalX=0 NormalY=0 NormalZ=1 AngleXU=0 Radius=1
    g23: Circle CenterX=-6.77343 CenterY=-8 CenterZ=0 NormalX=0 NormalY=0 NormalZ=1 AngleXU=0 Radius=1
    g24: BSplineCurve PolesCount=3 KnotsCount=2 Degree=2 IsPeriodic=0
    g25: GeomPoint X=-6.48644 Y=-5.99526 Z=0
    g26: GeomPoint X=-6.77343 Y=-8 Z=0
    g27: Circle CenterX=-7.19003 CenterY=-10 CenterZ=0 NormalX=0 NormalY=0 NormalZ=1 AngleXU=0 Radius=1
    g28: Circle CenterX=-7.44407 CenterY=-11.0915 CenterZ=0 NormalX=0 NormalY=0 NormalZ=1 AngleXU=0 Radius=1
    g29: Circle CenterX=-7.79258 CenterY=-12 CenterZ=0 NormalX=0 NormalY=0 NormalZ=1 AngleXU=0 Radius=1
    g30: BSplineCurve PolesCount=3 KnotsCount=2 Degree=2 IsPeriodic=0
    g31: GeomPoint X=-7.19003 Y=-10 Z=0
    g32: GeomPoint X=-7.79258 Y=-12 Z=0
    g33: Circle CenterX=-8.70761 CenterY=-14 CenterZ=0 NormalX=0 NormalY=0 NormalZ=1 AngleXU=0 Radius=1
    g34: Circle CenterX=-9.33087 CenterY=-15.1837 CenterZ=0 NormalX=0 NormalY=0 NormalZ=1 AngleXU=0 Radius=1
    g35: Circle CenterX=-10.1571 CenterY=-16 CenterZ=0 NormalX=0 NormalY=0 NormalZ=1 AngleXU=0 Radius=1
    g36: BSplineCurve PolesCount=3 KnotsCount=2 Degree=2 IsPeriodic=0
    g37: GeomPoint X=-8.70761 Y=-14 Z=0
    g38: GeomPoint X=-10.1571 Y=-16 Z=0
    g39: Circle CenterX=-12.8401 CenterY=-17.6958 CenterZ=0 NormalX=0 NormalY=0 NormalZ=1 AngleXU=0 Radius=1
    g40: Circle CenterX=-13.3521 CenterY=-17.9027 CenterZ=0 NormalX=0 NormalY=0 NormalZ=1 AngleXU=0 Radius=1
    g41: Circle CenterX=-14 CenterY=-18 CenterZ=0 NormalX=0 NormalY=0 NormalZ=1 AngleXU=0 Radius=1
    g42: BSplineCurve PolesCount=3 KnotsCount=2 Degree=2 IsPeriodic=0
    g43: GeomPoint X=-12.8401 Y=-17.6958 Z=0
    g44: GeomPoint X=-14 Y=-18 Z=0
    g45: LineSegment StartX=-6.2 StartY=0 StartZ=0 EndX=-7.2 EndY=0 EndZ=0
    g46: LineSegment StartX=-7.2 StartY=0 StartZ=0 EndX=-7.2 EndY=-2 EndZ=0
    g47: LineSegment StartX=-7.2 StartY=-2 StartZ=0 EndX=-6.2215 EndY=-2 EndZ=0
    g48: LineSegment StartX=-6.32538 StartY=-4 StartZ=0 EndX=-7.65538 EndY=-4 EndZ=0
    g49: LineSegment StartX=-7.65538 StartY=-4 StartZ=0 EndX=-7.65538 EndY=-5.99526 EndZ=0
    g50: LineSegment StartX=-7.65538 StartY=-5.99526 StartZ=0 EndX=-6.48644 EndY=-5.99526 EndZ=0
    g51: LineSegment StartX=-6.77343 StartY=-8 StartZ=0 EndX=-8.43343 EndY=-8 EndZ=0
    g52: LineSegment StartX=-8.43343 StartY=-8 StartZ=0 EndX=-8.43343 EndY=-10 EndZ=0
    g53: LineSegment StartX=-8.43343 StartY=-10 StartZ=0 EndX=-7.19003 EndY=-10 EndZ=0
  constraints (112):
    c: Horizontal(g0)
    c: Distance(g0) = 2
    c: Block(g0)
    c: Vertical(g1)
    c: Coincident(g2,g0)
    c: Vertical(g2)
    c: Block(g2)
    c: Coincident(g6,g2)
    c: Weight(g3) = 1
    c: Equal(g3,g4)
    c: Equal(g3,g5)
    c: InternalAlignment(g3,g6)
    c: InternalAlignment(g4,g6)
    c: InternalAlignment(g5,g6)
    c: InternalAlignment(g7,g6)
    c: InternalAlignment(g8,g6)
    c: Block(g6)
    c: Coincident(g9,g1)
    c: Coincident(g9,g6)
    c: Horizontal(g9)
    c: Vertical(g10)
    c: Block(g10)
    c: Horizontal(g11)
    c: Block(g11)
    c: Coincident(g12,g10)
    c: Horizontal(g12)
    c: Block(g12)
    c: Coincident(g13,g11)
    c: Vertical(g13)
    c: Block(g13)
    c: Coincident(g14,g10)
    c: Horizontal(g14)
    c: Block(g14)
    c: Block(g9)
    c: Block(g1)
    c: Weight(g15) = 1
    c: Equal(g15,g16)
    c: Equal(g15,g17)
    c: InternalAlignment(g15,g18)
    c: InternalAlignment(g16,g18)
    c: InternalAlignment(g17,g18)
    c: InternalAlignment(g19,g18)
    c: InternalAlignment(g20,g18)
    c: Weight(g21) = 1
    c: Equal(g21,g22)
    c: Equal(g21,g23)
    c: InternalAlignment(g21,g24)
    c: InternalAlignment(g22,g24)
    c: InternalAlignment(g23,g24)
    c: InternalAlignment(g25,g24)
    c: InternalAlignment(g26,g24)
    c: Weight(g27) = 1
    c: Equal(g27,g28)
    c: Equal(g27,g29)
    c: Coincident(g30,g14)
    c: InternalAlignment(g27,g30)
    c: InternalAlignment(g28,g30)
    c: InternalAlignment(g29,g30)
    c: InternalAlignment(g31,g30)
    c: InternalAlignment(g32,g30)
    c: Coincident(g36,g12)
    c: Weight(g33) = 1
    c: Equal(g33,g34)
    c: Equal(g33,g35)
    c: Coincident(g36,g11)
    c: InternalAlignment(g33,g36)
    c: InternalAlignment(g34,g36)
    c: InternalAlignment(g35,g36)
    c: InternalAlignment(g37,g36)
    c: InternalAlignment(g38,g36)
    c: Coincident(g42,g13)
    c: Weight(g39) = 1
    c: Equal(g39,g40)
    c: Equal(g39,g41)
    c: Coincident(g42,g1)
    c: InternalAlignment(g39,g42)
    c: InternalAlignment(g40,g42)
    c: InternalAlignment(g41,g42)
    c: InternalAlignment(g43,g42)
    c: InternalAlignment(g44,g42)
    c: Block(g18)
    c: Block(g24)
    c: Block(g30)
    c: Block(g36)
    c: Block(g42)
    c: Horizontal(g45)
    c: Coincident(g45,g0)
    c: Vertical(g46)
    c: Coincident(g46,g45)
    c: Coincident(g47,g46)
    c: Coincident(g47,g18)
    c: Horizontal(g47)
    c: Block(g46)
    c: Coincident(g48,g18)
    c: Horizontal(g48)
    c: Distance(g48) = 1.33
    c: Vertical(g49)
    c: Coincident(g49,g48)
    c: Coincident(g50,g49)
    c: Coincident(g50,g24)
    c: Horizontal(g50)
    c: Tangent(g50,g22)
    c: Horizontal(g51)
    c: Coincident(g51,g24)
    c: Block(g51)
    c: Vertical(g52)
    c: Block(g52)
    c: Coincident(g52,g51)
    c: Coincident(g53,g52)
    c: Coincident(g53,g30)
    c: Horizontal(g53)
    c: Distance(g1) = 8.5
FEATURE [Part::Feature] Face024
  shape: bbox 9.8 x 26.5 x 2e-07 mm, 1 faces, 0 solids (baked)
FEATURE [Part::Revolution] Revolve024
  Angle = 360
  Axis = (0,1,0)
  Base = (0,0,0)
  FaceMakerClass = Part::FaceMakerBullseye
  Placement = pos=(0,0,0) rot=(0,0,1;1.5708rad)
  Solid = false
  Source = -> Face024
  Symmetric = false
FEATURE [Part::Feature] Face025
  shape: bbox 9.8 x 26.5 x 2e-07 mm, 1 faces, 0 solids (baked)
FEATURE [Part::Revolution] Revolve025
  Angle = 360
  Axis = (0,1,0)
  Base = (0,0,0)
  FaceMakerClass = Part::FaceMakerBullseye
  Placement = pos=(0,0,0) rot=(0,0,1;1.5708rad)
  Solid = false
  Source = -> Face025
  Symmetric = false
FEATURE [Part::MultiFuse] Fusion033
  Placement = pos=(-18,19,36) rot=(0,0,1;0rad)
  Shapes = -> [Revolve025,Revolve024]
FEATURE [Part::Cylinder] Cylinder014
  Angle = 360
  AttacherType = Attacher::AttachEngine3D
  Height = 20
  Placement = pos=(0,0,36.15) rot=(0,0,1;0rad)
  Radius = 14.3
FEATURE [Part::Cylinder] Cylinder015
  Angle = 360
  AttacherType = Attacher::AttachEngine3D
  Height = 10
  Placement = pos=(0,0,36.15) rot=(0,0,1;0rad)
  Radius = 4
FEATURE [Part::MultiFuse] Fusion034  label="removeToCreteHoleForPlugHousing004"
  Placement = pos=(-42,19,36) rot=(0,1,0;1.5708rad)
  Shapes = -> [Cylinder014,Cylinder015]
FEATURE [Part::Cut] Cut008  label="top004"
  Base = -> Cut004
  Placement = pos=(-1,0,0) rot=(0,0,1;0rad)
  Tool = -> Fusion034
FEATURE [Part::Box] Box005  label="Cube005"
  AttacherType = Attacher::AttachEngine3D
  Height = 28
  Length = 3
  Placement = pos=(110.7,19,22) rot=(0,0,1;0rad)
  Width = 15.7
FEATURE [Part::Cylinder] Cylinder016
  Angle = 360
  AttacherType = Attacher::AttachEngine3D
  Height = 10
  Placement = pos=(0,0,36.15) rot=(0,0,1;0rad)
  Radius = 4
FEATURE [Part::Cylinder] Cylinder017
  Angle = 360
  AttacherType = Attacher::AttachEngine3D
  Height = 20
  Placement = pos=(0,0,36.15) rot=(0,0,1;0rad)
  Radius = 10.3
FEATURE [Part::MultiFuse] Fusion035  label="removeToCreteHoleForPlugHousing005"
  Placement = pos=(70,19,36) rot=(0,1,0;1.5708rad)
  Shapes = -> [Cylinder017,Cylinder016]
FEATURE [Part::Cut] Cut009  label="plugHousingTab001"
  Base = -> Box005
  Placement = pos=(-107.4,-14,0) rot=(0,0,1;0rad)
  Tool = -> Fusion035
FEATURE [Part::Box] Box006  label="Cube006"
  AttacherType = Attacher::AttachEngine3D
  Height = 28
  Length = 3
  Placement = pos=(110.7,19,22) rot=(0,0,1;0rad)
  Width = 15.7
FEATURE [Part::Cylinder] Cylinder018
  Angle = 360
  AttacherType = Attacher::AttachEngine3D
  Height = 10
  Placement = pos=(0,0,36.15) rot=(0,0,1;0rad)
  Radius = 4
FEATURE [Part::Cylinder] Cylinder019
  Angle = 360
  AttacherType = Attacher::AttachEngine3D
  Height = 20
  Placement = pos=(0,0,36.15) rot=(0,0,1;0rad)
  Radius = 10.3
FEATURE [Part::MultiFuse] Fusion036  label="removeToCreteHoleForPlugHousing006"
  Placement = pos=(70,19,36) rot=(0,1,0;1.5708rad)
  Shapes = -> [Cylinder019,Cylinder018]
FEATURE [Part::Cut] Cut010  label="plugHousingTab002"
  Base = -> Box006
  Placement = pos=(-107.4,-14,0) rot=(0,0,1;0rad)
  Tool = -> Fusion036
FEATURE [Part::MultiFuse] Fusion037
  Placement = pos=(9.6,23,0) rot=(0,0,1;3.14159rad)
  Shapes = -> [Cut009,Cut010]
FEATURE [Part::Box] Box  label="Cube"
  AttacherType = Attacher::AttachEngine3D
  Height = 10
  Length = 3
  Placement = pos=(3.3,4,12) rot=(0,0,1;0rad)
  Width = 10
FEATURE [Part::Fillet] Fillet004
  Base = -> Fusion028
  Edges = 1 edges r=2: [Edge25]
FEATURE [Part::Fillet] Fillet005  label="plugHousing046"
  Base = -> Fillet004
  Edges = 1 edges r=2: [Edge8]
FEATURE [Part::Fillet] Fillet006
  Base = -> Box
  Edges = 1 edges r=2: [Edge11]
FEATURE [Part::Box] Box007  label="Cube007"
  AttacherType = Attacher::AttachEngine3D
  Height = 10
  Length = 3
  Placement = pos=(3.3,4,50) rot=(0,0,1;0rad)
  Width = 10
FEATURE [Part::Fillet] Fillet007
  Base = -> Box007
  Edges = 1 edges r=2: [Edge12]
FEATURE [Part::Box] Box008  label="Cube008"
  AttacherType = Attacher::AttachEngine3D
  Height = 28
  Length = 4
  Placement = pos=(5,0,22) rot=(0,0,1;0rad)
  Width = 10
FEATURE [Part::Fillet] Fillet008
  Base = -> Box008
  Edges = 1 edges r=1: [Edge7]
FEATURE [Part::Fillet] Fillet009
  Base = -> Fillet008
  Edges = 1 edges r=2: [Edge5]
FEATURE [Part::Fillet] Fillet010
  Base = -> Fillet009
  Edges = 1 edges r=2: [Edge2]
FEATURE [Sketcher::SketchObject] Sketch009  label="topSketch003"
  FullyConstrained = true
  sketch-geometry (4):
    g0: LineSegment StartX=16.8446 StartY=31.512 StartZ=0 EndX=16.3251 EndY=34.4666 EndZ=0
    g1: ArcOfCircle CenterX=19 CenterY=19.2524 CenterZ=0 NormalX=0 NormalY=0 NormalZ=1 AngleXU=0 Radius=15.4476 StartAngle=1.74483 EndAngle=2.72717
    g2: ArcOfCircle CenterX=19 CenterY=19.2524 CenterZ=0 NormalX=0 NormalY=0 NormalZ=1 AngleXU=0 Radius=12.4476 StartAngle=1.74483 EndAngle=2.73189
    g3: LineSegment StartX=4.86004 StartY=25.4725 StartZ=0 EndX=7.58253 EndY=24.2107 EndZ=0
  constraints (7):
    c: Block(g0)
    c: Coincident(g1,g0)
    c: Coincident(g2,g0)
    c: Coincident(g3,g1)
    c: Coincident(g3,g2)
    c: Block(g1)
    c: Block(g2)
FEATURE [Part::Extrusion] Extrude008
  Base = -> Sketch009
  Dir = (0,0,1)
  DirMode = 2
  FaceMakerClass = Part::FaceMakerBullseye
  LengthFwd = 10
  LengthRev = 0
  Placement = pos=(0,0,31) rot=(0,0,1;0rad)
  Solid = true
  Symmetric = false
FEATURE [Part::Cylinder] Cylinder020
  Angle = 360
  AttacherType = Attacher::AttachEngine3D
  Height = 20
  Placement = pos=(0,0,36.15) rot=(0,0,1;0rad)
  Radius = 8.2
FEATURE [Part::Cylinder] Cylinder021
  Angle = 360
  AttacherType = Attacher::AttachEngine3D
  Height = 10
  Placement = pos=(0,0,36.15) rot=(0,0,1;0rad)
  Radius = 4
FEATURE [Part::MultiFuse] Fusion038  label="removeToCreteHoleForPlugHousing007"
  Placement = pos=(-42,19,36) rot=(0,1,0;1.5708rad)
  Shapes = -> [Cylinder020,Cylinder021]
FEATURE [Part::Cut] Cut011
  Base = -> Extrude008
  Tool = -> Fusion038
FEATURE [Part::Fillet] Fillet011
  Base = -> Cut011
  Edges = 1 edges r=2: [Edge1]
FEATURE [Part::Fillet] Fillet012
  Base = -> Fillet011
  Edges = 1 edges r=2.5: [Edge1]
FEATURE [Part::Fillet] Fillet013
  Base = -> Fillet012
  Edges = 1 edges r=2.5: [Edge2]
FEATURE [Part::Box] Box010  label="Cube010"
  AttacherType = Attacher::AttachEngine3D
  Height = 16
  Length = 8
  Placement = pos=(12.7,31.52,28) rot=(0,0,1;0rad)
  Width = 4
FEATURE [Sketcher::SketchObject] Sketch010  label="topSketch004"
  FullyConstrained = true
  sketch-geometry (4):
    g0: LineSegment StartX=16.8446 StartY=31.512 StartZ=0 EndX=16.3251 EndY=34.4666 EndZ=0
    g1: ArcOfCircle CenterX=19 CenterY=19.2524 CenterZ=0 NormalX=0 NormalY=0 NormalZ=1 AngleXU=0 Radius=15.4476 StartAngle=1.74483 EndAngle=2.72717
    g2: ArcOfCircle CenterX=19 CenterY=19.2524 CenterZ=0 NormalX=0 NormalY=0 NormalZ=1 AngleXU=0 Radius=12.4476 StartAngle=1.74483 EndAngle=2.73189
    g3: LineSegment StartX=4.86004 StartY=25.4725 StartZ=0 EndX=7.58253 EndY=24.2107 EndZ=0
  constraints (7):
    c: Block(g0)
    c: Coincident(g1,g0)
    c: Coincident(g2,g0)
    c: Coincident(g3,g1)
    c: Coincident(g3,g2)
    c: Block(g1)
    c: Block(g2)
FEATURE [Part::Cylinder] Cylinder022
  Angle = 360
  AttacherType = Attacher::AttachEngine3D
  Height = 10
  Placement = pos=(0,0,36.15) rot=(0,0,1;0rad)
  Radius = 4
FEATURE [Sketcher::SketchObject] Sketch011  label="topSketch005"
  FullyConstrained = true
  sketch-geometry (4):
    g0: LineSegment StartX=16.8446 StartY=31.512 StartZ=0 EndX=16.3251 EndY=34.4666 EndZ=0
    g1: ArcOfCircle CenterX=19 CenterY=19.2524 CenterZ=0 NormalX=0 NormalY=0 NormalZ=1 AngleXU=0 Radius=15.4476 StartAngle=1.74483 EndAngle=2.72717
    g2: ArcOfCircle CenterX=19 CenterY=19.2524 CenterZ=0 NormalX=0 NormalY=0 NormalZ=1 AngleXU=0 Radius=12.4476 StartAngle=1.74483 EndAngle=2.73189
    g3: LineSegment StartX=4.86004 StartY=25.4725 StartZ=0 EndX=7.58253 EndY=24.2107 EndZ=0
  constraints (7):
    c: Block(g0)
    c: Coincident(g1,g0)
    c: Coincident(g2,g0)
    c: Coincident(g3,g1)
    c: Coincident(g3,g2)
    c: Block(g1)
    c: Block(g2)
FEATURE [Part::Extrusion] Extrude010
  Base = -> Sketch011
  Dir = (0,0,1)
  DirMode = 2
  FaceMakerClass = Part::FaceMakerBullseye
  LengthFwd = 10.6
  LengthRev = 0
  Placement = pos=(0,0,31) rot=(0,0,1;0rad)
  Solid = true
  Symmetric = false
FEATURE [Part::Cylinder] Cylinder023
  Angle = 360
  AttacherType = Attacher::AttachEngine3D
  Height = 20
  Placement = pos=(0,0,36.15) rot=(0,0,1;0rad)
  Radius = 8.2
FEATURE [Part::MultiFuse] Fusion039  label="removeToCreteHoleForPlugHousing008"
  Placement = pos=(-42,19,36) rot=(0,1,0;1.5708rad)
  Shapes = -> [Cylinder023,Cylinder022]
FEATURE [Part::Cut] Cut012
  Base = -> Extrude010
  Placement = pos=(0,0,-0.3) rot=(0,0,1;0rad)
  Tool = -> Fusion039
FEATURE [Part::Cut] Cut013
  Base = -> Box010
  Tool = -> Cut012
FEATURE [Part::Fillet] Fillet014
  Base = -> Cut013
  Edges = 1 edges r=0.7: [Edge13]
FEATURE [Part::Fillet] Fillet015
  Base = -> Fillet014
  Edges = 1 edges r=0.7: [Edge13]
FEATURE [Part::Fillet] Fillet016
  Base = -> Fillet015
  Edges = 1 edges r=0.7: [Edge16]
FEATURE [Part::Fillet] Fillet017
  Base = -> Fillet016
  Edges = 1 edges r=0.7: [Edge11]
FEATURE [Part::Fillet] Fillet018
  Base = -> Fillet017
  Edges = 1 edges r=0.7: [Edge10]
FEATURE [Part::Fillet] Fillet019
  Base = -> Fillet018
  Edges = 1 edges r=1.2: [Edge5]
FEATURE [Part::Fillet] Fillet020
  Base = -> Fillet019
  Edges = 1 edges r=1.2: [Edge12]
FEATURE [Part::Fillet] Fillet021
  Base = -> Fillet020
  Edges = 1 edges r=2: [Edge1]
  Placement = pos=(0.3,0,0) rot=(0,0,1;0rad)
FEATURE [Part::MultiFuse] Fusion040  label="top005"
  Shapes = -> [Cut008,Fillet021]
FEATURE [Part::MultiFuse] Fusion041  label="wireHolder"
  Shapes = -> [Fusion033,Fillet013]
FEATURE [Part::MultiFuse] Fusion042
  Shapes = -> [Fillet007,Fusion041]
FEATURE [Part::MultiFuse] Fusion043  label="wireHolder001"
  Shapes = -> [Fusion042,Fillet010]
FEATURE [Part::MultiFuse] Fusion044  label="wireHolder002"
  Shapes = -> [Fillet006,Fusion037,Fusion043]
FEATURE [Part::Feature] Face026
  shape: bbox 11 x 6 x 2e-07 mm, 1 faces, 0 solids (baked)
FEATURE [Part::Revolution] Revolve026
  Angle = 360
  Axis = (0,1,0)
  Base = (0,0,0)
  FaceMakerClass = Part::FaceMakerBullseye
  Placement = pos=(30.3,-1,19.7) rot=(0,0,1;0rad)
  Solid = false
  Source = -> Face026
  Symmetric = false
FEATURE [Sketcher::SketchObject] Sketch013  label="topSketch006"
  FullyConstrained = true
  sketch-geometry (13):
    g0: LineSegment StartX=117 StartY=19 StartZ=0 EndX=117 EndY=38 EndZ=0
    g1: ArcOfCircle CenterX=98 CenterY=19 CenterZ=0 NormalX=0 NormalY=0 NormalZ=1 AngleXU=0 Radius=19 StartAngle=5.7297 EndAngle=6.28319
    g2: LineSegment StartX=0 StartY=3 StartZ=0 EndX=0 EndY=19 EndZ=0
    g3: LineSegment StartX=19 StartY=38 StartZ=0 EndX=117 EndY=38 EndZ=0
    g4: ArcOfCircle CenterX=19 CenterY=19 CenterZ=0 NormalX=0 NormalY=0 NormalZ=1 AngleXU=0 Radius=19 StartAngle=1.5708 EndAngle=3.14159
    g5: ArcOfCircle CenterX=19 CenterY=19 CenterZ=0 NormalX=0 NormalY=0 NormalZ=1 AngleXU=0 Radius=16 StartAngle=1.5708 EndAngle=3.14159
    g6: ArcOfCircle CenterX=98 CenterY=19 CenterZ=0 NormalX=0 NormalY=0 NormalZ=1 AngleXU=0 Radius=16 StartAngle=5.60905 EndAngle=6.28319
    g7: LineSegment StartX=114 StartY=19 StartZ=0 EndX=114 EndY=35 EndZ=0
    g8: LineSegment StartX=110.5 StartY=9.01251 StartZ=0 EndX=114.163 EndY=9.01251 EndZ=0
    g9: LineSegment StartX=114 StartY=35 StartZ=0 EndX=19 EndY=35 EndZ=0
    g10: LineSegment StartX=0 StartY=3 StartZ=0 EndX=0 EndY=0 EndZ=0
    g11: LineSegment StartX=3 StartY=0 StartZ=0 EndX=0 EndY=0 EndZ=0
    g12: LineSegment StartX=3 StartY=19 StartZ=0 EndX=3 EndY=0 EndZ=0
  constraints (33):
    c: Vertical(g0)
    c: Distance(g0) = 19
    c: Block(g0)
    c: Coincident(g1,g0)
    c: Block(g1)
    c: Vertical(g2)
    c: Block(g2)
    c: Coincident(g3,g0)
    c: Horizontal(g3)
    c: Distance(g3) = 98
    c: Coincident(g4,g3)
    c: Coincident(g4,g2)
    c: Block(g4)
    c: Coincident(g5,g4)
    c: Coincident(g6,g1)
    c: Block(g6)
    c: Block(g5)
    c: Coincident(g7,g6)
    c: Vertical(g7)
    c: Coincident(g8,g6)
    c: Coincident(g8,g1)
    c: Coincident(g9,g7)
    c: Coincident(g9,g5)
    c: Horizontal(g9)
    c: Tangent(g9,g5)
    c: Coincident(g10,g2)
    c: Distance(g10) = 3
    c: Vertical(g10)
    c: Coincident(g11,g10)
    c: Horizontal(g11)
    c: Coincident(g12,g5)
    c: Coincident(g12,g11)
    c: Vertical(g12)
FEATURE [Part::Extrusion] Extrude011  label="top006"
  Base = -> Sketch013
  Dir = (0,0,1)
  DirMode = 2
  FaceMakerClass = Part::FaceMakerBullseye
  LengthFwd = 72
  LengthRev = 0
  Solid = true
  Symmetric = false
FEATURE [Sketcher::SketchObject] Sketch014
  FullyConstrained = true
  MapMode = 3
  Placement = pos=(0,0,0) rot=(1,0,0;1.5708rad)
  Support = -> [Extrude011]
  sketch-geometry (8):
    g0: Circle CenterX=80.351 CenterY=-67.6202 CenterZ=0 NormalX=0 NormalY=0 NormalZ=1 AngleXU=0 Radius=2
    g1: Circle CenterX=80.351 CenterY=-67.6202 CenterZ=0 NormalX=0 NormalY=0 NormalZ=1 AngleXU=0 Radius=3
    g2: Circle CenterX=80.351 CenterY=-4.92017 CenterZ=0 NormalX=0 NormalY=0 NormalZ=1 AngleXU=0 Radius=2
    g3: Circle CenterX=80.351 CenterY=-4.92017 CenterZ=0 NormalX=0 NormalY=0 NormalZ=1 AngleXU=0 Radius=3
    g4: Circle CenterX=23.851 CenterY=-4.92017 CenterZ=0 NormalX=0 NormalY=0 NormalZ=1 AngleXU=0 Radius=2
    g5: Circle CenterX=23.851 CenterY=-4.92017 CenterZ=0 NormalX=0 NormalY=0 NormalZ=1 AngleXU=0 Radius=3
    g6: Circle CenterX=23.851 CenterY=-67.6202 CenterZ=0 NormalX=0 NormalY=0 NormalZ=1 AngleXU=0 Radius=2
    g7: Circle CenterX=23.851 CenterY=-67.6202 CenterZ=0 NormalX=0 NormalY=0 NormalZ=1 AngleXU=0 Radius=3
  constraints (8):
    c: Block(g3)
    c: Block(g2)
    c: Block(g1)
    c: Block(g0)
    c: Block(g6)
    c: Block(g7)
    c: Block(g4)
    c: Block(g5)
FEATURE [Part::Feature] Face027
  shape: bbox 11 x 6 x 2e-07 mm, 1 faces, 0 solids (baked)
FEATURE [Part::Revolution] Revolve027
  Angle = 360
  Axis = (0,1,0)
  Base = (0,0,0)
  FaceMakerClass = Part::FaceMakerBullseye
  Placement = pos=(30.3,-1,51.7) rot=(0,0,1;0rad)
  Solid = false
  Source = -> Face027
  Symmetric = false
FEATURE [Part::Feature] Face028
  shape: bbox 11 x 6 x 2e-07 mm, 1 faces, 0 solids (baked)
FEATURE [Part::Revolution] Revolve028
  Angle = 360
  Axis = (0,1,0)
  Base = (0,0,0)
  FaceMakerClass = Part::FaceMakerBullseye
  Placement = pos=(62.3,-1,19.7) rot=(0,0,1;0rad)
  Solid = false
  Source = -> Face028
  Symmetric = false
FEATURE [Part::Feature] Face029
  shape: bbox 11 x 6 x 2e-07 mm, 1 faces, 0 solids (baked)
FEATURE [Part::Revolution] Revolve029
  Angle = 360
  Axis = (0,1,0)
  Base = (0,0,0)
  FaceMakerClass = Part::FaceMakerBullseye
  Placement = pos=(62.3,-1,51.7) rot=(0,0,1;0rad)
  Solid = false
  Source = -> Face029
  Symmetric = false
FEATURE [Part::Feature] Wire
  shape: bbox 11 x 5.2 x 2e-07 mm, 0 faces, 0 solids (baked)
FEATURE [Part::Revolution] Revolve030
  Angle = 360
  Axis = (0,1,0)
  Base = (0,0,0)
  FaceMakerClass = Part::FaceMakerBullseye
  Placement = pos=(30.3,38,19.7) rot=(0,0,1;0rad)
  Solid = true
  Source = -> Wire
  Symmetric = false
FEATURE [Part::Feature] Wire001
  shape: bbox 11 x 5.2 x 2e-07 mm, 0 faces, 0 solids (baked)
FEATURE [Part::Revolution] Revolve031
  Angle = 360
  Axis = (0,1,0)
  Base = (0,0,0)
  FaceMakerClass = Part::FaceMakerBullseye
  Placement = pos=(30.3,38,51.7) rot=(0,0,1;0rad)
  Solid = true
  Source = -> Wire001
  Symmetric = false
FEATURE [Part::Feature] Wire002
  shape: bbox 11 x 5.2 x 2e-07 mm, 0 faces, 0 solids (baked)
FEATURE [Part::Revolution] Revolve032
  Angle = 360
  Axis = (0,1,0)
  Base = (0,0,0)
  FaceMakerClass = Part::FaceMakerBullseye
  Placement = pos=(62.3,38,51.7) rot=(0,0,1;0rad)
  Solid = true
  Source = -> Wire002
  Symmetric = false
FEATURE [Part::Feature] Wire003
  shape: bbox 11 x 5.2 x 2e-07 mm, 0 faces, 0 solids (baked)
FEATURE [Part::Revolution] Revolve033
  Angle = 360
  Axis = (0,1,0)
  Base = (0,0,0)
  FaceMakerClass = Part::FaceMakerBullseye
  Placement = pos=(62.3,38,19.7) rot=(0,0,1;0rad)
  Solid = true
  Source = -> Wire003
  Symmetric = false
FEATURE [Part::MultiFuse] Fusion045  label="altRandScrewHousing"
  Shapes = -> [Revolve029,Revolve027,Revolve028,Revolve026]
FEATURE [Part::MultiFuse] Fusion046  label="fanScrewHousing"
  Shapes = -> [Revolve033,Revolve032,Revolve031,Revolve030]
FEATURE [Sketcher::SketchObject] Sketch015
  FullyConstrained = true
  sketch-geometry (17):
    g0: Circle CenterX=-3.5 CenterY=23.5 CenterZ=0 NormalX=0 NormalY=0 NormalZ=1 AngleXU=0 Radius=1
    g1: Circle CenterX=-1 CenterY=15.25 CenterZ=0 NormalX=0 NormalY=0 NormalZ=1 AngleXU=0 Radius=1
    g2: Circle CenterX=-3.5 CenterY=7 CenterZ=0 NormalX=0 NormalY=0 NormalZ=1 AngleXU=0 Radius=1
    g3: BSplineCurve PolesCount=3 KnotsCount=2 Degree=2 IsPeriodic=0
    g4: GeomPoint X=-3.5 Y=23.5 Z=0
    g5: GeomPoint X=-3.5 Y=7 Z=0
    g6: Circle CenterX=-4.8 CenterY=30.5 CenterZ=0 NormalX=0 NormalY=0 NormalZ=1 AngleXU=0 Radius=1
    g7: Circle CenterX=-3.5 CenterY=30.5 CenterZ=0 NormalX=0 NormalY=0 NormalZ=1 AngleXU=0 Radius=1
    g8: Circle CenterX=-3.5 CenterY=29.2 CenterZ=0 NormalX=0 NormalY=0 NormalZ=1 AngleXU=0 Radius=1
    g9: BSplineCurve PolesCount=3 KnotsCount=2 Degree=2 IsPeriodic=0
    g10: GeomPoint X=-4.8 Y=30.5 Z=0
    g11: GeomPoint X=-3.5 Y=29.2 Z=0
    g12: LineSegment StartX=-3.5 StartY=29.2 StartZ=0 EndX=-3.5 EndY=23.5 EndZ=0
    g13: LineSegment StartX=-4.8 StartY=30.5 StartZ=0 EndX=0 EndY=30.5 EndZ=0
    g14: LineSegment StartX=-3.5 StartY=0.3 StartZ=0 EndX=0 EndY=0.3 EndZ=0
    g15: LineSegment StartX=-3.5 StartY=0.3 StartZ=0 EndX=-3.5 EndY=7 EndZ=0
    g16: LineSegment StartX=0 StartY=0.3 StartZ=0 EndX=0 EndY=30.5 EndZ=0
  constraints (33):
    c: Weight(g0) = 1
    c: Equal(g0,g1)
    c: Equal(g0,g2)
    c: InternalAlignment(g0,g3)
    c: InternalAlignment(g1,g3)
    c: InternalAlignment(g2,g3)
    c: InternalAlignment(g4,g3)
    c: InternalAlignment(g5,g3)
    c: Block(g3)
    c: Weight(g6) = 1
    c: Equal(g6,g7)
    c: Equal(g6,g8)
    c: InternalAlignment(g6,g9)
    c: InternalAlignment(g7,g9)
    c: InternalAlignment(g8,g9)
    c: InternalAlignment(g10,g9)
    c: InternalAlignment(g11,g9)
    c: Block(g9)
    c: Coincident(g12,g9)
    c: Coincident(g12,g3)
    c: Vertical(g12)
    c: Coincident(g13,g9)
    c: Horizontal(g13)
    c: Distance(g13) = 4.8
    c: Horizontal(g14)
    c: Block(g14)
    c: Coincident(g15,g14)
    c: Coincident(g15,g3)
    c: Vertical(g15)
    c: Coincident(g16,g14)
    c: Coincident(g16,g13)
    c: Vertical(g16)
    c: Tangent(g16,g1)
FEATURE [Sketcher::SketchObject] Sketch016
  FullyConstrained = true
  sketch-geometry (16):
    g0: Circle CenterX=-3.5 CenterY=23.5 CenterZ=0 NormalX=0 NormalY=0 NormalZ=1 AngleXU=0 Radius=1
    g1: Circle CenterX=-1 CenterY=15.25 CenterZ=0 NormalX=0 NormalY=0 NormalZ=1 AngleXU=0 Radius=1
    g2: Circle CenterX=-3.5 CenterY=7 CenterZ=0 NormalX=0 NormalY=0 NormalZ=1 AngleXU=0 Radius=1
    g3: BSplineCurve PolesCount=3 KnotsCount=2 Degree=2 IsPeriodic=0
    g4: GeomPoint X=-3.5 Y=23.5 Z=0
    g5: GeomPoint X=-3.5 Y=7 Z=0
    g6: LineSegment StartX=-3.5 StartY=28.2 StartZ=0 EndX=-3.5 EndY=23.5 EndZ=0
    g7: LineSegment StartX=0 StartY=29.5 StartZ=0 EndX=0 EndY=30 EndZ=0
    g8: LineSegment StartX=-3.5 StartY=28.2 StartZ=0 EndX=-3.5 EndY=30 EndZ=0
    g9: LineSegment StartX=0 StartY=30 StartZ=0 EndX=0 EndY=30.5 EndZ=0
    g10: LineSegment StartX=0 StartY=30.5 StartZ=0 EndX=-3.5 EndY=30.5 EndZ=0
    g11: LineSegment StartX=-3.5 StartY=30.5 StartZ=0 EndX=-3.5 EndY=30 EndZ=0
    g12: LineSegment StartX=0 StartY=29.5 StartZ=0 EndX=0 EndY=5 EndZ=0
    g13: LineSegment StartX=-3.5 StartY=0.3 StartZ=0 EndX=-3.5 EndY=7 EndZ=0
    g14: LineSegment StartX=-3.5 StartY=0.3 StartZ=0 EndX=0 EndY=0.3 EndZ=0
    g15: LineSegment StartX=0 StartY=5 StartZ=0 EndX=0 EndY=0.3 EndZ=0
  constraints (39):
    c: Weight(g0) = 1
    c: Equal(g0,g1)
    c: Equal(g0,g2)
    c: InternalAlignment(g0,g3)
    c: InternalAlignment(g1,g3)
    c: InternalAlignment(g2,g3)
    c: InternalAlignment(g4,g3)
    c: InternalAlignment(g5,g3)
    c: Block(g3)
    c: Coincident(g6,g3)
    c: Vertical(g6)
    c: Vertical(g7)
    c: Distance(g7) = 0.5
    c: Coincident(g8,g6)
    c: Vertical(g8)
    c: Block(g6)
    c: Block(g7)
    c: Vertical(g9)
    c: Equal(g7,g9) = 0.5
    c: Block(g9)
    c: Coincident(g9,g7)
    c: Horizontal(g10)
    c: Coincident(g10,g9)
    c: Coincident(g11,g10)
    c: Coincident(g11,g8)
    c: Vertical(g11)
    c: Block(g11)
    c: Coincident(g12,g7)
    c: Vertical(g12)
    c: Coincident(g13,g3)
    c: Vertical(g13)
    c: Distance(g13) = 6.7
    c: Coincident(g14,g13)
    c: Horizontal(g14)
    c: Block(g14)
    c: Coincident(g15,g12)
    c: Coincident(g15,g14)
    c: Vertical(g15)
    c: Block(g15)
FEATURE [Sketcher::SketchObject] Sketch017
  FullyConstrained = true
  sketch-geometry (11):
    g0: LineSegment StartX=-3.5 StartY=1e-16 StartZ=0 EndX=-1.6 EndY=1e-16 EndZ=0
    g1: LineSegment StartX=-1.6 StartY=1e-16 StartZ=0 EndX=-1.6 EndY=1.5 EndZ=0
    g2: LineSegment StartX=-3.5 StartY=1.5 StartZ=0 EndX=-1.6 EndY=1.5 EndZ=0
    g3: LineSegment StartX=-3.5 StartY=1e-16 StartZ=0 EndX=-4.8 EndY=1e-16 EndZ=0
    g4: Circle CenterX=-3.5 CenterY=1.3 CenterZ=0 NormalX=0 NormalY=0 NormalZ=1 AngleXU=0 Radius=1
    g5: Circle CenterX=-3.5 CenterY=1e-16 CenterZ=0 NormalX=0 NormalY=0 NormalZ=1 AngleXU=0 Radius=1
    g6: Circle CenterX=-4.8 CenterY=1e-16 CenterZ=0 NormalX=0 NormalY=0 NormalZ=1 AngleXU=0 Radius=1
    g7: BSplineCurve PolesCount=3 KnotsCount=2 Degree=2 IsPeriodic=0
    g8: GeomPoint X=-3.5 Y=1.3 Z=0
    g9: GeomPoint X=-4.8 Y=1e-16 Z=0
    g10: LineSegment StartX=-3.5 StartY=1.3 StartZ=0 EndX=-3.5 EndY=1.5 EndZ=0
  constraints (24):
    c: Horizontal(g0)
    c: Distance(g0) = 1.9
    c: Block(g0)
    c: Coincident(g1,g0)
    c: Vertical(g1)
    c: Coincident(g2,g1)
    c: Horizontal(g2)
    c: Coincident(g3,g0)
    c: Horizontal(g3)
    c: Distance(g3) = 1.3
    c: Weight(g4) = 1
    c: Equal(g4,g5)
    c: Coincident(g5,g0)
    c: Equal(g4,g6)
    c: Coincident(g7,g3)
    c: InternalAlignment(g4,g7)
    c: InternalAlignment(g5,g7)
    c: InternalAlignment(g6,g7)
    c: InternalAlignment(g8,g7)
    c: InternalAlignment(g9,g7)
    c: Coincident(g10,g7)
    c: Coincident(g10,g2)
    c: Vertical(g10)
    c: Block(g10)
FEATURE [Part::Feature] Face035
  shape: bbox 3.2 x 1.5 x 2e-07 mm, 1 faces, 0 solids (baked)
FEATURE [Part::Revolution] Revolve039  label="backCaseScrewRetainer"
  Angle = 360
  Axis = (0,1,0)
  Base = (0,0,0)
  FaceMakerClass = Part::FaceMakerBullseye
  Placement = pos=(12.5,3,62) rot=(0,0,1;0rad)
  Solid = false
  Source = -> Face035
  Symmetric = false
FEATURE [Part::Feature] Face036
  shape: bbox 3.2 x 1.5 x 2e-07 mm, 1 faces, 0 solids (baked)
FEATURE [Part::Feature] Face039
  shape: bbox 4.8 x 30.2 x 2e-07 mm, 1 faces, 0 solids (baked)
FEATURE [Part::Revolution] Revolve043  label="frontCaseScrewPost002"
  Angle = 360
  Axis = (0,1,0)
  Base = (0,0,0)
  FaceMakerClass = Part::FaceMakerBullseye
  Placement = pos=(89.5,4.5,3.5) rot=(0,0,1;0rad)
  Solid = false
  Source = -> Face039
  Symmetric = false
FEATURE [Part::Feature] Face042
  shape: bbox 4.8 x 30.2 x 2e-07 mm, 1 faces, 0 solids (baked)
FEATURE [Part::Revolution] Revolve046  label="frontCaseScrewPost003"
  Angle = 360
  Axis = (0,1,0)
  Base = (0,0,0)
  FaceMakerClass = Part::FaceMakerBullseye
  Placement = pos=(89.5,4.5,68.5) rot=(0,0,1;0rad)
  Solid = false
  Source = -> Face042
  Symmetric = false
FEATURE [Part::Feature] Face043
  shape: bbox 3.2 x 1.5 x 2e-07 mm, 1 faces, 0 solids (baked)
FEATURE [Part::Revolution] Revolve047  label="frontCaseScrewRetainer002"
  Angle = 360
  Axis = (0,1,0)
  Base = (0,0,0)
  FaceMakerClass = Part::FaceMakerBullseye
  Placement = pos=(89.5,3,68.5) rot=(0,0,1;0rad)
  Solid = false
  Source = -> Face043
  Symmetric = false
FEATURE [Part::Feature] Face044
  shape: bbox 3.2 x 1.5 x 2e-07 mm, 1 faces, 0 solids (baked)
FEATURE [Part::Revolution] Revolve048  label="frontCaseScrewRetainer003"
  Angle = 360
  Axis = (0,1,0)
  Base = (0,0,0)
  FaceMakerClass = Part::FaceMakerBullseye
  Placement = pos=(89.5,3,3.5) rot=(0,0,1;0rad)
  Solid = false
  Source = -> Face044
  Symmetric = false
FEATURE [App::MeasureDistance] Distance002  label="Distance: 1.67 mm"
  Distance = 1.66921
  P1 = (99.2361,4.7524,71.7)
  P2 = (99.2347,6.42161,71.7)
FEATURE [Sketcher::SketchObject] Sketch018
  FullyConstrained = true
  sketch-geometry (7):
    g0: LineSegment StartX=0 StartY=0 StartZ=0 EndX=0 EndY=6 EndZ=0
    g1: Circle CenterX=0 CenterY=0 CenterZ=0 NormalX=0 NormalY=0 NormalZ=1 AngleXU=0 Radius=1
    g2: Circle CenterX=8 CenterY=6 CenterZ=0 NormalX=0 NormalY=0 NormalZ=1 AngleXU=0 Radius=1
    g3: BSplineCurve PolesCount=3 KnotsCount=2 Degree=2 IsPeriodic=0
    g4: GeomPoint X=0 Y=0 Z=0
    g5: GeomPoint X=8 Y=6 Z=0
    g6: LineSegment StartX=0 StartY=6 StartZ=0 EndX=8 EndY=6 EndZ=0
  constraints (14):
    c: Coincident(g0,g-1)
    c: Distance(g0) = 6
    c: Vertical(g0)
    c: Coincident(g3,g0)
    c: Weight(g1) = 1
    c: Equal(g1,g2)
    c: InternalAlignment(g1,g3)
    c: InternalAlignment(g2,g3)
    c: InternalAlignment(g4,g3)
    c: InternalAlignment(g5,g3)
    c: Block(g3)
    c: Coincident(g6,g0)
    c: Coincident(g6,g3)
    c: Horizontal(g6)
FEATURE [Part::Extrusion] Extrude012  label="caseScrewPillarBracket"
  Base = -> Sketch018
  Dir = (0,0,1)
  DirMode = 2
  FaceMakerClass = Part::FaceMakerBullseye
  LengthFwd = 2.4
  LengthRev = 0
  Placement = pos=(15.76,29,8.8) rot=(0,1,0;0rad)
  Solid = true
  Symmetric = false
FEATURE [Sketcher::SketchObject] Sketch019
  FullyConstrained = true
  sketch-geometry (7):
    g0: LineSegment StartX=0 StartY=0 StartZ=0 EndX=0 EndY=6 EndZ=0
    g1: Circle CenterX=0 CenterY=0 CenterZ=0 NormalX=0 NormalY=0 NormalZ=1 AngleXU=0 Radius=1
    g2: Circle CenterX=8 CenterY=6 CenterZ=0 NormalX=0 NormalY=0 NormalZ=1 AngleXU=0 Radius=1
    g3: BSplineCurve PolesCount=3 KnotsCount=2 Degree=2 IsPeriodic=0
    g4: GeomPoint X=0 Y=0 Z=0
    g5: GeomPoint X=8 Y=6 Z=0
    g6: LineSegment StartX=0 StartY=6 StartZ=0 EndX=8 EndY=6 EndZ=0
  constraints (14):
    c: Coincident(g0,g-1)
    c: Distance(g0) = 6
    c: Vertical(g0)
    c: Coincident(g3,g0)
    c: Weight(g1) = 1
    c: Equal(g1,g2)
    c: InternalAlignment(g1,g3)
    c: InternalAlignment(g2,g3)
    c: InternalAlignment(g4,g3)
    c: InternalAlignment(g5,g3)
    c: Block(g3)
    c: Coincident(g6,g0)
    c: Coincident(g6,g3)
    c: Horizontal(g6)
FEATURE [Part::Extrusion] Extrude013  label="caseScrewPillarBracket001"
  Base = -> Sketch019
  Dir = (0,0,1)
  DirMode = 2
  FaceMakerClass = Part::FaceMakerBullseye
  LengthFwd = 2.4
  LengthRev = 0
  Placement = pos=(15.76,29,60.8) rot=(0,0,1;0rad)
  Solid = true
  Symmetric = false
FEATURE [Sketcher::SketchObject] Sketch020
  FullyConstrained = true
  sketch-geometry (7):
    g0: LineSegment StartX=0 StartY=0 StartZ=0 EndX=0 EndY=6 EndZ=0
    g1: Circle CenterX=0 CenterY=0 CenterZ=0 NormalX=0 NormalY=0 NormalZ=1 AngleXU=0 Radius=1
    g2: Circle CenterX=8 CenterY=6 CenterZ=0 NormalX=0 NormalY=0 NormalZ=1 AngleXU=0 Radius=1
    g3: BSplineCurve PolesCount=3 KnotsCount=2 Degree=2 IsPeriodic=0
    g4: GeomPoint X=0 Y=0 Z=0
    g5: GeomPoint X=8 Y=6 Z=0
    g6: LineSegment StartX=0 StartY=6 StartZ=0 EndX=8 EndY=6 EndZ=0
  constraints (14):
    c: Coincident(g0,g-1)
    c: Distance(g0) = 6
    c: Vertical(g0)
    c: Coincident(g3,g0)
    c: Weight(g1) = 1
    c: Equal(g1,g2)
    c: InternalAlignment(g1,g3)
    c: InternalAlignment(g2,g3)
    c: InternalAlignment(g4,g3)
    c: InternalAlignment(g5,g3)
    c: Block(g3)
    c: Coincident(g6,g0)
    c: Coincident(g6,g3)
    c: Horizontal(g6)
FEATURE [Part::Extrusion] Extrude014  label="caseScrewPillarBracket002"
  Base = -> Sketch020
  Dir = (0,0,1)
  DirMode = 2
  FaceMakerClass = Part::FaceMakerBullseye
  LengthFwd = 2.4
  LengthRev = 0
  Placement = pos=(13.7,29,13.26) rot=(0,-1,0;1.5708rad)
  Solid = true
  Symmetric = false
FEATURE [Sketcher::SketchObject] Sketch021
  FullyConstrained = true
  sketch-geometry (7):
    g0: LineSegment StartX=0 StartY=0 StartZ=0 EndX=0 EndY=6 EndZ=0
    g1: Circle CenterX=0 CenterY=0 CenterZ=0 NormalX=0 NormalY=0 NormalZ=1 AngleXU=0 Radius=1
    g2: Circle CenterX=8 CenterY=6 CenterZ=0 NormalX=0 NormalY=0 NormalZ=1 AngleXU=0 Radius=1
    g3: BSplineCurve PolesCount=3 KnotsCount=2 Degree=2 IsPeriodic=0
    g4: GeomPoint X=0 Y=0 Z=0
    g5: GeomPoint X=8 Y=6 Z=0
    g6: LineSegment StartX=0 StartY=6 StartZ=0 EndX=8 EndY=6 EndZ=0
  constraints (14):
    c: Coincident(g0,g-1)
    c: Distance(g0) = 6
    c: Vertical(g0)
    c: Coincident(g3,g0)
    c: Weight(g1) = 1
    c: Equal(g1,g2)
    c: InternalAlignment(g1,g3)
    c: InternalAlignment(g2,g3)
    c: InternalAlignment(g4,g3)
    c: InternalAlignment(g5,g3)
    c: Block(g3)
    c: Coincident(g6,g0)
    c: Coincident(g6,g3)
    c: Horizontal(g6)
FEATURE [Part::Extrusion] Extrude015  label="caseScrewPillarBracket003"
  Base = -> Sketch021
  Dir = (0,0,1)
  DirMode = 2
  FaceMakerClass = Part::FaceMakerBullseye
  LengthFwd = 2.4
  LengthRev = 0
  Placement = pos=(11.3,29,58.74) rot=(0,1,0;1.5708rad)
  Solid = true
  Symmetric = false
FEATURE [Sketcher::SketchObject] Sketch022
  FullyConstrained = true
  sketch-geometry (7):
    g0: LineSegment StartX=0 StartY=0 StartZ=0 EndX=0 EndY=6 EndZ=0
    g1: Circle CenterX=0 CenterY=0 CenterZ=0 NormalX=0 NormalY=0 NormalZ=1 AngleXU=0 Radius=1
    g2: Circle CenterX=8 CenterY=6 CenterZ=0 NormalX=0 NormalY=0 NormalZ=1 AngleXU=0 Radius=1
    g3: BSplineCurve PolesCount=3 KnotsCount=2 Degree=2 IsPeriodic=0
    g4: GeomPoint X=0 Y=0 Z=0
    g5: GeomPoint X=8 Y=6 Z=0
    g6: LineSegment StartX=0 StartY=6 StartZ=0 EndX=8 EndY=6 EndZ=0
  constraints (14):
    c: Coincident(g0,g-1)
    c: Distance(g0) = 6
    c: Vertical(g0)
    c: Coincident(g3,g0)
    c: Weight(g1) = 1
    c: Equal(g1,g2)
    c: InternalAlignment(g1,g3)
    c: InternalAlignment(g2,g3)
    c: InternalAlignment(g4,g3)
    c: InternalAlignment(g5,g3)
    c: Block(g3)
    c: Coincident(g6,g0)
    c: Coincident(g6,g3)
    c: Horizontal(g6)
FEATURE [Part::Extrusion] Extrude016  label="caseScrewPillarBracket004"
  Base = -> Sketch022
  Dir = (0,0,1)
  DirMode = 2
  FaceMakerClass = Part::FaceMakerBullseye
  LengthFwd = 2.4
  LengthRev = 0
  Placement = pos=(88.3,29,65.23) rot=(0,1,0;1.5708rad)
  Solid = true
  Symmetric = false
FEATURE [Sketcher::SketchObject] Sketch023
  FullyConstrained = true
  sketch-geometry (7):
    g0: LineSegment StartX=0 StartY=0 StartZ=0 EndX=0 EndY=6 EndZ=0
    g1: Circle CenterX=0 CenterY=0 CenterZ=0 NormalX=0 NormalY=0 NormalZ=1 AngleXU=0 Radius=1
    g2: Circle CenterX=8 CenterY=6 CenterZ=0 NormalX=0 NormalY=0 NormalZ=1 AngleXU=0 Radius=1
    g3: BSplineCurve PolesCount=3 KnotsCount=2 Degree=2 IsPeriodic=0
    g4: GeomPoint X=0 Y=0 Z=0
    g5: GeomPoint X=8 Y=6 Z=0
    g6: LineSegment StartX=0 StartY=6 StartZ=0 EndX=8 EndY=6 EndZ=0
  constraints (14):
    c: Coincident(g0,g-1)
    c: Distance(g0) = 6
    c: Vertical(g0)
    c: Coincident(g3,g0)
    c: Weight(g1) = 1
    c: Equal(g1,g2)
    c: InternalAlignment(g1,g3)
    c: InternalAlignment(g2,g3)
    c: InternalAlignment(g4,g3)
    c: InternalAlignment(g5,g3)
    c: Block(g3)
    c: Coincident(g6,g0)
    c: Coincident(g6,g3)
    c: Horizontal(g6)
FEATURE [Part::Extrusion] Extrude017  label="caseScrewPillarBracket005"
  Base = -> Sketch023
  Dir = (0,0,1)
  DirMode = 2
  FaceMakerClass = Part::FaceMakerBullseye
  LengthFwd = 2.4
  LengthRev = 0
  Placement = pos=(90.7,29,6.77) rot=(0,-1,0;1.5708rad)
  Solid = true
  Symmetric = false
FEATURE [Sketcher::SketchObject] Sketch024
  FullyConstrained = true
  sketch-geometry (7):
    g0: LineSegment StartX=0 StartY=0 StartZ=0 EndX=0 EndY=6 EndZ=0
    g1: Circle CenterX=0 CenterY=0 CenterZ=0 NormalX=0 NormalY=0 NormalZ=1 AngleXU=0 Radius=1
    g2: Circle CenterX=8 CenterY=6 CenterZ=0 NormalX=0 NormalY=0 NormalZ=1 AngleXU=0 Radius=1
    g3: BSplineCurve PolesCount=3 KnotsCount=2 Degree=2 IsPeriodic=0
    g4: GeomPoint X=0 Y=0 Z=0
    g5: GeomPoint X=8 Y=6 Z=0
    g6: LineSegment StartX=0 StartY=6 StartZ=0 EndX=8 EndY=6 EndZ=0
  constraints (14):
    c: Coincident(g0,g-1)
    c: Distance(g0) = 6
    c: Vertical(g0)
    c: Coincident(g3,g0)
    c: Weight(g1) = 1
    c: Equal(g1,g2)
    c: InternalAlignment(g1,g3)
    c: InternalAlignment(g2,g3)
    c: InternalAlignment(g4,g3)
    c: InternalAlignment(g5,g3)
    c: Block(g3)
    c: Coincident(g6,g0)
    c: Coincident(g6,g3)
    c: Horizontal(g6)
FEATURE [Part::Extrusion] Extrude018  label="caseScrewPillarBracket006"
  Base = -> Sketch024
  Dir = (0,0,1)
  DirMode = 2
  FaceMakerClass = Part::FaceMakerBullseye
  LengthFwd = 2.4
  LengthRev = 0
  Placement = pos=(103.7,29,6.77) rot=(0,-1,0;1.5708rad)
  Solid = true
  Symmetric = false
FEATURE [Sketcher::SketchObject] Sketch025
  FullyConstrained = true
  sketch-geometry (7):
    g0: LineSegment StartX=0 StartY=0 StartZ=0 EndX=0 EndY=6 EndZ=0
    g1: Circle CenterX=0 CenterY=0 CenterZ=0 NormalX=0 NormalY=0 NormalZ=1 AngleXU=0 Radius=1
    g2: Circle CenterX=8 CenterY=6 CenterZ=0 NormalX=0 NormalY=0 NormalZ=1 AngleXU=0 Radius=1
    g3: BSplineCurve PolesCount=3 KnotsCount=2 Degree=2 IsPeriodic=0
    g4: GeomPoint X=0 Y=0 Z=0
    g5: GeomPoint X=8 Y=6 Z=0
    g6: LineSegment StartX=0 StartY=6 StartZ=0 EndX=8 EndY=6 EndZ=0
  constraints (14):
    c: Coincident(g0,g-1)
    c: Distance(g0) = 6
    c: Vertical(g0)
    c: Coincident(g3,g0)
    c: Weight(g1) = 1
    c: Equal(g1,g2)
    c: InternalAlignment(g1,g3)
    c: InternalAlignment(g2,g3)
    c: InternalAlignment(g4,g3)
    c: InternalAlignment(g5,g3)
    c: Block(g3)
    c: Coincident(g6,g0)
    c: Coincident(g6,g3)
    c: Horizontal(g6)
FEATURE [Part::Extrusion] Extrude019  label="caseScrewPillarBracket007"
  Base = -> Sketch025
  Dir = (0,0,1)
  DirMode = 2
  FaceMakerClass = Part::FaceMakerBullseye
  LengthFwd = 2.4
  LengthRev = 0
  Placement = pos=(101.3,29,65.23) rot=(0,1,0;1.5708rad)
  Solid = true
  Symmetric = false
FEATURE [Part::Box] Box011  label="frontCaseScrewPillarBracket"
  AttacherType = Attacher::AttachEngine3D
  Height = 2.4
  Length = 16
  Placement = pos=(87,28,2.3) rot=(0,0,1;0rad)
  Width = 7
FEATURE [Part::Box] Box012  label="frontCaseScrewPillarBracket001"
  AttacherType = Attacher::AttachEngine3D
  Height = 2.4
  Length = 16
  Placement = pos=(87,28,67.3) rot=(0,0,1;0rad)
  Width = 7
FEATURE [Sketcher::SketchObject] Sketch026
  FullyConstrained = true
  sketch-geometry (17):
    g0: Circle CenterX=-3.5 CenterY=23.5 CenterZ=0 NormalX=0 NormalY=0 NormalZ=1 AngleXU=0 Radius=1
    g1: Circle CenterX=-1 CenterY=15.25 CenterZ=0 NormalX=0 NormalY=0 NormalZ=1 AngleXU=0 Radius=1
    g2: Circle CenterX=-3.5 CenterY=7 CenterZ=0 NormalX=0 NormalY=0 NormalZ=1 AngleXU=0 Radius=1
    g3: BSplineCurve PolesCount=3 KnotsCount=2 Degree=2 IsPeriodic=0
    g4: GeomPoint X=-3.5 Y=23.5 Z=0
    g5: GeomPoint X=-3.5 Y=7 Z=0
    g6: Circle CenterX=-4.8 CenterY=30.5 CenterZ=0 NormalX=0 NormalY=0 NormalZ=1 AngleXU=0 Radius=1
    g7: Circle CenterX=-3.5 CenterY=30.5 CenterZ=0 NormalX=0 NormalY=0 NormalZ=1 AngleXU=0 Radius=1
    g8: Circle CenterX=-3.5 CenterY=29.2 CenterZ=0 NormalX=0 NormalY=0 NormalZ=1 AngleXU=0 Radius=1
    g9: BSplineCurve PolesCount=3 KnotsCount=2 Degree=2 IsPeriodic=0
    g10: GeomPoint X=-4.8 Y=30.5 Z=0
    g11: GeomPoint X=-3.5 Y=29.2 Z=0
    g12: LineSegment StartX=-3.5 StartY=29.2 StartZ=0 EndX=-3.5 EndY=23.5 EndZ=0
    g13: LineSegment StartX=-4.8 StartY=30.5 StartZ=0 EndX=0 EndY=30.5 EndZ=0
    g14: LineSegment StartX=-3.5 StartY=5 StartZ=0 EndX=-3.5 EndY=7 EndZ=0
    g15: LineSegment StartX=0 StartY=5 StartZ=0 EndX=0 EndY=30.5 EndZ=0
    g16: LineSegment StartX=-3.5 StartY=5 StartZ=0 EndX=0 EndY=5 EndZ=0
  constraints (33):
    c: Weight(g0) = 1
    c: Equal(g0,g1)
    c: Equal(g0,g2)
    c: InternalAlignment(g0,g3)
    c: InternalAlignment(g1,g3)
    c: InternalAlignment(g2,g3)
    c: InternalAlignment(g4,g3)
    c: InternalAlignment(g5,g3)
    c: Block(g3)
    c: Weight(g6) = 1
    c: Equal(g6,g7)
    c: Equal(g6,g8)
    c: InternalAlignment(g6,g9)
    c: InternalAlignment(g7,g9)
    c: InternalAlignment(g8,g9)
    c: InternalAlignment(g10,g9)
    c: InternalAlignment(g11,g9)
    c: Block(g9)
    c: Coincident(g12,g9)
    c: Coincident(g12,g3)
    c: Vertical(g12)
    c: Coincident(g13,g9)
    c: Horizontal(g13)
    c: Distance(g13) = 4.8
    c: Coincident(g14,g3)
    c: Vertical(g14)
    c: Coincident(g15,g13)
    c: Vertical(g15)
    c: Tangent(g15,g1)
    c: Distance(g14) = 2
    c: Coincident(g16,g14)
    c: Horizontal(g16)
    c: Coincident(g15,g16)
FEATURE [Part::Feature] Face050
  shape: bbox 4.8 x 25.5 x 2e-07 mm, 1 faces, 0 solids (baked)
FEATURE [Part::Revolution] Revolve054  label="moreFrontCaseScrewPost001"
  Angle = 360
  Axis = (0,1,0)
  Base = (0,0,0)
  FaceMakerClass = Part::FaceMakerBullseye
  Placement = pos=(102.5,4.5,3.5) rot=(0,0,1;0rad)
  Solid = false
  Source = -> Face050
  Symmetric = false
FEATURE [Part::Feature] Face051
  shape: bbox 4.8 x 25.5 x 2e-07 mm, 1 faces, 0 solids (baked)
FEATURE [Part::Revolution] Revolve055  label="moreFrontCaseScrewPost002"
  Angle = 360
  Axis = (0,1,0)
  Base = (0,0,0)
  FaceMakerClass = Part::FaceMakerBullseye
  Placement = pos=(102.5,4.5,68.5) rot=(0,0,1;0rad)
  Solid = false
  Source = -> Face051
  Symmetric = false
FEATURE [Sketcher::SketchObject] Sketch027
  FullyConstrained = true
  sketch-geometry (10):
    g0: LineSegment StartX=-1.6 StartY=4.7 StartZ=0 EndX=-1.6 EndY=1.7 EndZ=0
    g1: LineSegment StartX=-3.5 StartY=4.7 StartZ=0 EndX=-1.6 EndY=4.7 EndZ=0
    g2: LineSegment StartX=-1.6 StartY=1.7 StartZ=0 EndX=-1.6 EndY=1.5 EndZ=0
    g3: LineSegment StartX=-1.6 StartY=1.5 StartZ=0 EndX=-5.2 EndY=1.5 EndZ=0
    g4: Circle CenterX=-3.5 CenterY=4.7 CenterZ=0 NormalX=0 NormalY=0 NormalZ=1 AngleXU=0 Radius=1
    g5: Circle CenterX=-3.59627 CenterY=2.99743 CenterZ=0 NormalX=0 NormalY=0 NormalZ=1 AngleXU=0 Radius=1
    g6: Circle CenterX=-5.2 CenterY=1.5 CenterZ=0 NormalX=0 NormalY=0 NormalZ=1 AngleXU=0 Radius=1
    g7: BSplineCurve PolesCount=3 KnotsCount=2 Degree=2 IsPeriodic=0
    g8: GeomPoint X=-3.5 Y=4.7 Z=0
    g9: GeomPoint X=-5.2 Y=1.5 Z=0
  constraints (23):
    c: Vertical(g0)
    c: Distance(g0) = 3
    c: Coincident(g1,g0)
    c: Horizontal(g1)
    c: Block(g0)
    c: Block(g1)
    c: Coincident(g2,g0)
    c: Vertical(g2)
    c: Distance(g2) = 0.2
    c: Coincident(g3,g2)
    c: Horizontal(g3)
    c: Block(g3)
    c: Coincident(g7,g1)
    c: Weight(g4) = 1
    c: Equal(g4,g5)
    c: Equal(g4,g6)
    c: Coincident(g7,g3)
    c: InternalAlignment(g4,g7)
    c: InternalAlignment(g5,g7)
    c: InternalAlignment(g6,g7)
    c: InternalAlignment(g8,g7)
    c: InternalAlignment(g9,g7)
    c: Block(g7)
FEATURE [Sketcher::SketchObject] Sketch028
  FullyConstrained = true
  sketch-geometry (18):
    g0: LineSegment StartX=0 StartY=3e-16 StartZ=0 EndX=0 EndY=1.7 EndZ=0
    g1: LineSegment StartX=-3.5 StartY=0 StartZ=0 EndX=-3.5 EndY=0.9 EndZ=0
    g2: Circle CenterX=-2.7 CenterY=1.7 CenterZ=0 NormalX=0 NormalY=0 NormalZ=1 AngleXU=0 Radius=1
    g3: Circle CenterX=-3.5 CenterY=1.7 CenterZ=0 NormalX=0 NormalY=0 NormalZ=1 AngleXU=0 Radius=1
    g4: Circle CenterX=-3.5 CenterY=0.9 CenterZ=0 NormalX=0 NormalY=0 NormalZ=1 AngleXU=0 Radius=1
    g5: BSplineCurve PolesCount=3 KnotsCount=2 Degree=2 IsPeriodic=0
    g6: GeomPoint X=-2.7 Y=1.7 Z=0
    g7: GeomPoint X=-3.5 Y=0.9 Z=0
    g8: LineSegment StartX=-3.5 StartY=0 StartZ=0 EndX=-3.5 EndY=-7 EndZ=0
    g9: LineSegment StartX=0 StartY=3e-16 StartZ=0 EndX=0 EndY=-7 EndZ=0
    g10: LineSegment StartX=-3.5 StartY=-7 StartZ=0 EndX=0 EndY=-7 EndZ=0
    g11: LineSegment StartX=-2.7 StartY=1.7 StartZ=0 EndX=-1.6 EndY=1.7 EndZ=0
    g12: LineSegment StartX=0 StartY=1.7 StartZ=0 EndX=0 EndY=4.5 EndZ=0
    g13: LineSegment StartX=0 StartY=4.5 StartZ=0 EndX=0 EndY=10.8 EndZ=0
    g14: LineSegment StartX=0 StartY=10.8 StartZ=0 EndX=-2 EndY=10.8 EndZ=0
    g15: LineSegment StartX=-1.6 StartY=4.7 StartZ=0 EndX=-1.6 EndY=1.7 EndZ=0
    g16: LineSegment StartX=-1.6 StartY=4.7 StartZ=0 EndX=-2 EndY=4.7 EndZ=0
    g17: LineSegment StartX=-2 StartY=4.7 StartZ=0 EndX=-2 EndY=10.8 EndZ=0
  constraints (44):
    c: Vertical(g0)
    c: Vertical(g1)
    c: Distance(g1) = 0.9
    c: Block(g0)
    c: Distance(g0) = 1.7
    c: Weight(g2) = 1
    c: Equal(g2,g3)
    c: Equal(g2,g4)
    c: Coincident(g5,g1)
    c: InternalAlignment(g2,g5)
    c: InternalAlignment(g3,g5)
    c: InternalAlignment(g4,g5)
    c: InternalAlignment(g6,g5)
    c: InternalAlignment(g7,g5)
    c: Block(g5)
    c: Coincident(g8,g1)
    c: Vertical(g8)
    c: Distance(g8) = 7
    c: Vertical(g9)
    c: Equal(g8,g9) = 7
    c: Coincident(g9,g0)
    c: Coincident(g10,g8)
    c: Coincident(g10,g9)
    c: Horizontal(g10)
    c: Coincident(g11,g5)
    c: Horizontal(g11)
    c: Coincident(g12,g0)
    c: Vertical(g12)
    c: Distance(g12) = 2.8
    c: Coincident(g13,g12)
    c: Vertical(g13)
    c: Distance(g13) = 6.3
    c: Coincident(g14,g13)
    c: Horizontal(g14)
    c: Distance(g14) = 2
    c: Vertical(g15)
    c: Distance(g15) = 3
    c: Block(g11)
    c: Coincident(g15,g11)
    c: Coincident(g16,g15)
    c: Horizontal(g16)
    c: Coincident(g17,g16)
    c: Coincident(g17,g14)
    c: Vertical(g17)
FEATURE [Part::Revolution] Revolve040  label="backCaseScrewRetainer001"
  Angle = 360
  Axis = (0,1,0)
  Base = (0,0,0)
  FaceMakerClass = Part::FaceMakerBullseye
  Placement = pos=(12.5,3,10) rot=(0,0,1;0rad)
  Solid = false
  Source = -> Face036
  Symmetric = false
FEATURE [Part::Feature] Face055
  shape: bbox 3.5 x 30.2 x 2e-07 mm, 1 faces, 0 solids (baked)
FEATURE [Part::Revolution] Revolve059  label="backCaseScrewPost"
  Angle = 360
  Axis = (0,1,0)
  Base = (0,0,0)
  FaceMakerClass = Part::FaceMakerBullseye
  Placement = pos=(12.5,4.5,10) rot=(0,0,1;0rad)
  Solid = false
  Source = -> Face055
  Symmetric = false
FEATURE [Part::Feature] Face056
  shape: bbox 3.5 x 30.2 x 2e-07 mm, 1 faces, 0 solids (baked)
FEATURE [Part::Revolution] Revolve060  label="backCaseScrewPost001"
  Angle = 360
  Axis = (0,1,0)
  Base = (0,0,0)
  FaceMakerClass = Part::FaceMakerBullseye
  Placement = pos=(12.5,4.5,62) rot=(0,0,1;0rad)
  Solid = false
  Source = -> Face056
  Symmetric = false
FEATURE [Part::Feature] Face057
  shape: bbox 3.5 x 17.8 x 2e-07 mm, 1 faces, 0 solids (baked)
FEATURE [Part::Revolution] Revolve061  label="removeToCreateScrewAndThreadedInsertHole"
  Angle = 360
  Axis = (0,1,0)
  Base = (0,0,0)
  FaceMakerClass = Part::FaceMakerBullseye
  Placement = pos=(12.5,0,10) rot=(0,0,1;0rad)
  Solid = false
  Source = -> Face057
  Symmetric = false
FEATURE [Part::Feature] Face058
  shape: bbox 3.5 x 17.8 x 2e-07 mm, 1 faces, 0 solids (baked)
FEATURE [Part::Revolution] Revolve062  label="removeToCreateScrewAndThreadedInsertHole001"
  Angle = 360
  Axis = (0,1,0)
  Base = (0,0,0)
  FaceMakerClass = Part::FaceMakerBullseye
  Placement = pos=(12.5,0,62) rot=(0,0,1;0rad)
  Solid = false
  Source = -> Face058
  Symmetric = false
FEATURE [Part::Feature] Face059
  shape: bbox 3.5 x 17.8 x 2e-07 mm, 1 faces, 0 solids (baked)
FEATURE [Part::Revolution] Revolve063  label="removeToCreateScrewAndThreadedInsertHole002"
  Angle = 360
  Axis = (0,1,0)
  Base = (0,0,0)
  FaceMakerClass = Part::FaceMakerBullseye
  Placement = pos=(89.5,0,68.5) rot=(0,0,1;0rad)
  Solid = false
  Source = -> Face059
  Symmetric = false
FEATURE [Part::Feature] Face060
  shape: bbox 3.5 x 17.8 x 2e-07 mm, 1 faces, 0 solids (baked)
FEATURE [Part::Revolution] Revolve064  label="removeToCreateScrewAndThreadedInsertHole003"
  Angle = 360
  Axis = (0,1,0)
  Base = (0,0,0)
  FaceMakerClass = Part::FaceMakerBullseye
  Placement = pos=(89.5,0,3.5) rot=(0,0,1;0rad)
  Solid = false
  Source = -> Face060
  Symmetric = false
FEATURE [Part::Feature] Face061
  shape: bbox 3.5 x 17.8 x 2e-07 mm, 1 faces, 0 solids (baked)
FEATURE [Part::Revolution] Revolve065  label="removeToCreateScrewAndThreadedInsertHole004"
  Angle = 360
  Axis = (0,1,0)
  Base = (0,0,0)
  FaceMakerClass = Part::FaceMakerBullseye
  Placement = pos=(102.5,4.7,3.5) rot=(0,0,1;0rad)
  Solid = false
  Source = -> Face061
  Symmetric = false
FEATURE [Part::Feature] Face062
  shape: bbox 3.5 x 17.8 x 2e-07 mm, 1 faces, 0 solids (baked)
FEATURE [Part::Revolution] Revolve066  label="removeToCreateScrewAndThreadedInsertHole005"
  Angle = 360
  Axis = (0,1,0)
  Base = (0,0,0)
  FaceMakerClass = Part::FaceMakerBullseye
  Placement = pos=(102.5,4.7,68.5) rot=(0,0,1;0rad)
  Solid = false
  Source = -> Face062
  Symmetric = false
FEATURE [Part::MultiFuse] Fusion047  label="makeHoles"
  Shapes = -> [Revolve066,Revolve065,Revolve064,Revolve063,Revolve062,Revolve061]
FEATURE [Part::Feature] Face063
  shape: bbox 3.6 x 3.2 x 2e-07 mm, 1 faces, 0 solids (baked)
FEATURE [Part::Revolution] Revolve067  label="moreFrontCaseScrewRetainer002"
  Angle = 360
  Axis = (0,1,0)
  Base = (0,0,0)
  FaceMakerClass = Part::FaceMakerBullseye
  Placement = pos=(102.5,4.5,68.5) rot=(0,0,1;0rad)
  Solid = false
  Source = -> Face063
  Symmetric = false
FEATURE [Part::Feature] Face064
  shape: bbox 3.6 x 3.2 x 2e-07 mm, 1 faces, 0 solids (baked)
FEATURE [Part::Revolution] Revolve068  label="moreFrontCaseScrewRetainer003"
  Angle = 360
  Axis = (0,1,0)
  Base = (0,0,0)
  FaceMakerClass = Part::FaceMakerBullseye
  Placement = pos=(102.5,4.5,3.5) rot=(0,0,1;0rad)
  Solid = false
  Source = -> Face064
  Symmetric = false
FEATURE [Part::Feature] Face065
  shape: bbox 3.5 x 17.8 x 2e-07 mm, 1 faces, 0 solids (baked)
FEATURE [Part::Revolution] Revolve069  label="removeToCreateScrewAndThreadedInsertHole006"
  Angle = 360
  Axis = (0,1,0)
  Base = (0,0,0)
  FaceMakerClass = Part::FaceMakerBullseye
  Placement = pos=(12.5,0,10) rot=(0,0,1;0rad)
  Solid = false
  Source = -> Face065
  Symmetric = false
FEATURE [Part::Feature] Face066
  shape: bbox 3.5 x 17.8 x 2e-07 mm, 1 faces, 0 solids (baked)
FEATURE [Part::Revolution] Revolve070  label="removeToCreateScrewAndThreadedInsertHole007"
  Angle = 360
  Axis = (0,1,0)
  Base = (0,0,0)
  FaceMakerClass = Part::FaceMakerBullseye
  Placement = pos=(12.5,0,62) rot=(0,0,1;0rad)
  Solid = false
  Source = -> Face066
  Symmetric = false
FEATURE [Part::Feature] Face067
  shape: bbox 3.5 x 17.8 x 2e-07 mm, 1 faces, 0 solids (baked)
FEATURE [Part::Revolution] Revolve071  label="removeToCreateScrewAndThreadedInsertHole008"
  Angle = 360
  Axis = (0,1,0)
  Base = (0,0,0)
  FaceMakerClass = Part::FaceMakerBullseye
  Placement = pos=(89.5,0,68.5) rot=(0,0,1;0rad)
  Solid = false
  Source = -> Face067
  Symmetric = false
FEATURE [Part::Feature] Face068
  shape: bbox 3.5 x 17.8 x 2e-07 mm, 1 faces, 0 solids (baked)
FEATURE [Part::Revolution] Revolve072  label="removeToCreateScrewAndThreadedInsertHole009"
  Angle = 360
  Axis = (0,1,0)
  Base = (0,0,0)
  FaceMakerClass = Part::FaceMakerBullseye
  Placement = pos=(89.5,0,3.5) rot=(0,0,1;0rad)
  Solid = false
  Source = -> Face068
  Symmetric = false
FEATURE [Part::Feature] Face069
  shape: bbox 3.5 x 17.8 x 2e-07 mm, 1 faces, 0 solids (baked)
FEATURE [Part::Feature] Face070
  shape: bbox 3.5 x 17.8 x 2e-07 mm, 1 faces, 0 solids (baked)
FEATURE [Part::Revolution] Revolve073  label="removeToCreateScrewAndThreadedInsertHole010"
  Angle = 360
  Axis = (0,1,0)
  Base = (0,0,0)
  FaceMakerClass = Part::FaceMakerBullseye
  Placement = pos=(102.5,4.7,3.5) rot=(0,0,1;0rad)
  Solid = false
  Source = -> Face069
  Symmetric = false
FEATURE [Part::Revolution] Revolve074  label="removeToCreateScrewAndThreadedInsertHole011"
  Angle = 360
  Axis = (0,1,0)
  Base = (0,0,0)
  FaceMakerClass = Part::FaceMakerBullseye
  Placement = pos=(102.5,4.7,68.5) rot=(0,0,1;0rad)
  Solid = false
  Source = -> Face070
  Symmetric = false
FEATURE [Part::MultiFuse] Fusion048  label="makeHoles001"
  Shapes = -> [Revolve074,Revolve073,Revolve072,Revolve071,Revolve070,Revolve069]
FEATURE [Part::MultiFuse] Fusion049  label="caseScrewRetainers"
  Shapes = -> [Revolve067,Revolve068,Revolve048,Revolve047,Revolve039,Revolve040]
FEATURE [Part::Cut] Cut015  label="caseScrewRetainers001"
  Base = -> Fusion049
  Tool = -> Fusion048
FEATURE [Part::MultiFuse] Fusion050  label="casePillars"
  Shapes = -> [Revolve055,Revolve054,Revolve043,Revolve046,Revolve059,Revolve060]
FEATURE [Part::Feature] Face071 .. Face076  x6 (patterned run collapsed; names and placements below)
  shape: bbox 3.5 x 17.8 x 2e-07 mm, 1 faces, 0 solids (baked)
FEATURE [Part::Revolution] Revolve075  label="removeToCreateScrewAndThreadedInsertHole012"
  Angle = 360
  Axis = (0,1,0)
  Base = (0,0,0)
  FaceMakerClass = Part::FaceMakerBullseye
  Placement = pos=(12.5,0,10) rot=(0,0,1;0rad)
  Solid = false
  Source = -> Face071
  Symmetric = false
FEATURE [Part::Revolution] Revolve076  label="removeToCreateScrewAndThreadedInsertHole013"
  Angle = 360
  Axis = (0,1,0)
  Base = (0,0,0)
  FaceMakerClass = Part::FaceMakerBullseye
  Placement = pos=(12.5,0,62) rot=(0,0,1;0rad)
  Solid = false
  Source = -> Face072
  Symmetric = false
FEATURE [Part::Revolution] Revolve077  label="removeToCreateScrewAndThreadedInsertHole014"
  Angle = 360
  Axis = (0,1,0)
  Base = (0,0,0)
  FaceMakerClass = Part::FaceMakerBullseye
  Placement = pos=(89.5,0,68.5) rot=(0,0,1;0rad)
  Solid = false
  Source = -> Face073
  Symmetric = false
FEATURE [Part::Revolution] Revolve078  label="removeToCreateScrewAndThreadedInsertHole015"
  Angle = 360
  Axis = (0,1,0)
  Base = (0,0,0)
  FaceMakerClass = Part::FaceMakerBullseye
  Placement = pos=(89.5,0,3.5) rot=(0,0,1;0rad)
  Solid = false
  Source = -> Face074
  Symmetric = false
FEATURE [Part::Revolution] Revolve079  label="removeToCreateScrewAndThreadedInsertHole016"
  Angle = 360
  Axis = (0,1,0)
  Base = (0,0,0)
  FaceMakerClass = Part::FaceMakerBullseye
  Placement = pos=(102.5,4.7,3.5) rot=(0,0,1;0rad)
  Solid = false
  Source = -> Face075
  Symmetric = false
FEATURE [Part::Revolution] Revolve080  label="removeToCreateScrewAndThreadedInsertHole017"
  Angle = 360
  Axis = (0,1,0)
  Base = (0,0,0)
  FaceMakerClass = Part::FaceMakerBullseye
  Placement = pos=(102.5,4.7,68.5) rot=(0,0,1;0rad)
  Solid = false
  Source = -> Face076
  Symmetric = false
FEATURE [Part::MultiFuse] Fusion051  label="makeHoles002"
  Shapes = -> [Revolve080,Revolve079,Revolve078,Revolve077,Revolve076,Revolve075]
FEATURE [Part::Cut] Cut016  label="caesPillars"
  Base = -> Fusion050
  Tool = -> Fusion051
FEATURE [Part::Revolution] Revolve009  label="plugHousing016"
  Angle = 360
  Axis = (0,1,0)
  Base = (0,0,0)
  FaceMakerClass = Part::FaceMakerBullseye
  Placement = pos=(0,0,36.15) rot=(0,0,1;0rad)
  Solid = false
  Source = -> Face012
  Symmetric = false
FEATURE [Part::MultiFuse] Fusion014  label="plugHousing023"
  Placement = pos=(0,0,0) rot=(0,0,1;1.5708rad)
  Shapes = -> [Revolve011,Revolve009]
FEATURE [Part::Revolution] Revolve010  label="plugHousing017"
  Angle = 360
  Axis = (0,1,0)
  Base = (0,0,0)
  FaceMakerClass = Part::FaceMakerBullseye
  Placement = pos=(0,0,36.15) rot=(0,0,1;0rad)
  Solid = false
  Source = -> Face014
  Symmetric = false
FEATURE [Part::MultiFuse] Fusion015  label="plugHousing024"
  Placement = pos=(0,0,0) rot=(0,0,1;1.5708rad)
  Shapes = -> [Revolve010,Revolve015]
FEATURE [Part::Revolution] Revolve014  label="plugHousing026"
  Angle = 360
  Axis = (0,1,0)
  Base = (0,0,0)
  FaceMakerClass = Part::FaceMakerBullseye
  Placement = pos=(0,0,36.15) rot=(0,0,1;0rad)
  Solid = false
  Source = -> Face011
  Symmetric = false
FEATURE [Part::Revolution] Revolve013  label="plugHousing025"
  Angle = 360
  Axis = (0,1,0)
  Base = (0,0,0)
  FaceMakerClass = Part::FaceMakerBullseye
  Placement = pos=(0,0,36.15) rot=(0,0,1;0rad)
  Solid = false
  Source = -> Face015
  Symmetric = false
FEATURE [Part::MultiFuse] Fusion016  label="plugHousing028"
  Placement = pos=(0,19,0) rot=(0,0,1;3.14159rad)
  Shapes = -> [Fusion014,Fusion013]
FEATURE [Part::MultiFuse] Fusion011  label="plugHousing018"
  Placement = pos=(0,0,0) rot=(0,0,1;1.5708rad)
  Shapes = -> [Revolve014,Revolve013]
FEATURE [Part::MultiFuse] Fusion012  label="plugHousing019"
  Placement = pos=(0,19,0) rot=(0,0,1;3.14159rad)
  Shapes = -> [Fusion011,Fusion015]
FEATURE [Part::MultiFuse] Fusion017  label="plugHousing029"
  Placement = pos=(122.621,0,-0.15) rot=(0,0,1;0rad)
  Shapes = -> [Fusion016,Fusion012]
FEATURE [Part::MultiFuse] Fusion052  label="casePillarRetainers"
  Shapes = -> [Extrude012,Extrude013,Extrude014,Extrude015,Extrude016,Extrude017,Extrude018,Extrude019,Box011,Box012]
FEATURE [Part::Feature] Face077
  shape: bbox 3.5 x 17.8 x 2e-07 mm, 1 faces, 0 solids (baked)
FEATURE [Part::Revolution] Revolve081  label="removeToCreateScrewAndThreadedInsertHole018"
  Angle = 360
  Axis = (0,1,0)
  Base = (0,0,0)
  FaceMakerClass = Part::FaceMakerBullseye
  Placement = pos=(62.3,30.3,19.7) rot=(0,0,1;0rad)
  Solid = false
  Source = -> Face077
  Symmetric = false
FEATURE [Part::Feature] Face078
  shape: bbox 3.5 x 17.8 x 2e-07 mm, 1 faces, 0 solids (baked)
FEATURE [Part::Revolution] Revolve082  label="removeToCreateScrewAndThreadedInsertHole019"
  Angle = 360
  Axis = (0,1,0)
  Base = (0,0,0)
  FaceMakerClass = Part::FaceMakerBullseye
  Placement = pos=(62.3,30.3,51.7) rot=(0,0,1;0rad)
  Solid = false
  Source = -> Face078
  Symmetric = false
FEATURE [Part::Feature] Face079
  shape: bbox 3.5 x 17.8 x 2e-07 mm, 1 faces, 0 solids (baked)
FEATURE [Part::Revolution] Revolve083  label="removeToCreateScrewAndThreadedInsertHole020"
  Angle = 360
  Axis = (0,1,0)
  Base = (0,0,0)
  FaceMakerClass = Part::FaceMakerBullseye
  Placement = pos=(30.3,30.3,19.7) rot=(0,0,1;0rad)
  Solid = false
  Source = -> Face079
  Symmetric = false
FEATURE [Part::Feature] Face080
  shape: bbox 3.5 x 17.8 x 2e-07 mm, 1 faces, 0 solids (baked)
FEATURE [Part::Revolution] Revolve084  label="removeToCreateScrewAndThreadedInsertHole021"
  Angle = 360
  Axis = (0,1,0)
  Base = (0,0,0)
  FaceMakerClass = Part::FaceMakerBullseye
  Placement = pos=(30.3,30.3,51.7) rot=(0,0,1;0rad)
  Solid = false
  Source = -> Face080
  Symmetric = false
FEATURE [Part::MultiFuse] Fusion053  label="createThreadedInsertHolesForFan"
  Shapes = -> [Revolve081,Revolve082,Revolve083,Revolve084]
FEATURE [Part::Cut] Cut017  label="fanScrewHousing001"
  Base = -> Fusion046
  Tool = -> Fusion053
FEATURE [Part::Feature] Face081
  shape: bbox 3.5 x 17.8 x 2e-07 mm, 1 faces, 0 solids (baked)
FEATURE [Part::Revolution] Revolve085  label="removeToCreateScrewAndThreadedInsertHole022"
  Angle = 360
  Axis = (0,1,0)
  Base = (0,0,0)
  FaceMakerClass = Part::FaceMakerBullseye
  Placement = pos=(62.3,30.3,19.7) rot=(0,0,1;0rad)
  Solid = false
  Source = -> Face081
  Symmetric = false
FEATURE [Part::Feature] Face082
  shape: bbox 3.5 x 17.8 x 2e-07 mm, 1 faces, 0 solids (baked)
FEATURE [Part::Revolution] Revolve086  label="removeToCreateScrewAndThreadedInsertHole023"
  Angle = 360
  Axis = (0,1,0)
  Base = (0,0,0)
  FaceMakerClass = Part::FaceMakerBullseye
  Placement = pos=(62.3,30.3,51.7) rot=(0,0,1;0rad)
  Solid = false
  Source = -> Face082
  Symmetric = false
FEATURE [Part::Feature] Face083
  shape: bbox 3.5 x 17.8 x 2e-07 mm, 1 faces, 0 solids (baked)
FEATURE [Part::Revolution] Revolve087  label="removeToCreateScrewAndThreadedInsertHole024"
  Angle = 360
  Axis = (0,1,0)
  Base = (0,0,0)
  FaceMakerClass = Part::FaceMakerBullseye
  Placement = pos=(30.3,30.3,19.7) rot=(0,0,1;0rad)
  Solid = false
  Source = -> Face083
  Symmetric = false
FEATURE [Part::Feature] Face084
  shape: bbox 3.5 x 17.8 x 2e-07 mm, 1 faces, 0 solids (baked)
FEATURE [Part::Revolution] Revolve088  label="removeToCreateScrewAndThreadedInsertHole025"
  Angle = 360
  Axis = (0,1,0)
  Base = (0,0,0)
  FaceMakerClass = Part::FaceMakerBullseye
  Placement = pos=(30.3,30.3,51.7) rot=(0,0,1;0rad)
  Solid = false
  Source = -> Face084
  Symmetric = false
FEATURE [Part::MultiFuse] Fusion054  label="createThreadedInsertHolesForFan001"
  Shapes = -> [Revolve085,Revolve086,Revolve087,Revolve088]
FEATURE [Part::Cut] Cut018  label="top007"
  Base = -> Fusion040
  Tool = -> Fusion054
FEATURE [Sketcher::SketchObject] Sketch029
  FullyConstrained = false
  Placement = pos=(0,0,0) rot=(1,0,0;1.5708rad)
  sketch-geometry (24):
    g0: ArcOfCircle CenterX=-4 CenterY=-10.5 CenterZ=0 NormalX=0 NormalY=0 NormalZ=1 AngleXU=0 Radius=1.5 StartAngle=6e-16 EndAngle=3.14159
    g1: ArcOfCircle CenterX=-34.2 CenterY=-10.5 CenterZ=0 NormalX=0 NormalY=0 NormalZ=1 AngleXU=0 Radius=1.5 StartAngle=0 EndAngle=3.14159
    g2: ArcOfCircle CenterX=-34.2 CenterY=-27.7 CenterZ=0 NormalX=0 NormalY=0 NormalZ=1 AngleXU=0 Radius=1.5 StartAngle=3.14159 EndAngle=6.28319
    g3: ArcOfCircle CenterX=-4 CenterY=-27.7 CenterZ=0 NormalX=0 NormalY=0 NormalZ=1 AngleXU=0 Radius=1.5 StartAngle=3.1416 EndAngle=6.28319
    g4: ArcOfCircle CenterX=-10 CenterY=-4.3 CenterZ=0 NormalX=0 NormalY=0 NormalZ=1 AngleXU=0 Radius=1.5 StartAngle=2e-16 EndAngle=3.14159
    g5: ArcOfCircle CenterX=-16.1 CenterY=-1.8 CenterZ=0 NormalX=0 NormalY=0 NormalZ=1 AngleXU=0 Radius=1.5 StartAngle=5e-16 EndAngle=3.14159
    g6: ArcOfCircle CenterX=-22.1 CenterY=-1.8 CenterZ=0 NormalX=0 NormalY=0 NormalZ=1 AngleXU=0 Radius=1.5 StartAngle=5e-16 EndAngle=3.14159
    g7: ArcOfCircle CenterX=-28.2 CenterY=-4.3 CenterZ=0 NormalX=0 NormalY=0 NormalZ=1 AngleXU=0 Radius=1.5 StartAngle=2e-16 EndAngle=3.14159
    g8: ArcOfCircle CenterX=-10 CenterY=-33.9 CenterZ=0 NormalX=0 NormalY=0 NormalZ=1 AngleXU=0 Radius=1.5 StartAngle=3.14159 EndAngle=6.28319
    g9: ArcOfCircle CenterX=-16.1 CenterY=-36.4 CenterZ=0 NormalX=0 NormalY=0 NormalZ=1 AngleXU=0 Radius=1.5 StartAngle=3.14159 EndAngle=6.28319
    g10: ArcOfCircle CenterX=-22.1 CenterY=-36.4 CenterZ=0 NormalX=0 NormalY=0 NormalZ=1 AngleXU=0 Radius=1.5 StartAngle=3.14159 EndAngle=6.28319
    g11: ArcOfCircle CenterX=-28.2 CenterY=-33.9 CenterZ=0 NormalX=0 NormalY=0 NormalZ=1 AngleXU=0 Radius=1.5 StartAngle=3.14159 EndAngle=6.28319
    g12: LineSegment StartX=-35.7 StartY=-10.5 StartZ=0 EndX=-35.7 EndY=-27.7 EndZ=0
    g13: LineSegment StartX=-32.7 StartY=-10.5 StartZ=0 EndX=-32.7 EndY=-27.7 EndZ=0
    g14: LineSegment StartX=-29.7 StartY=-33.9 StartZ=0 EndX=-29.7 EndY=-4.3 EndZ=0
    g15: LineSegment StartX=-26.7 StartY=-33.9 StartZ=0 EndX=-26.7 EndY=-4.3 EndZ=0
    g16: LineSegment StartX=-2.5 StartY=-10.5 StartZ=0 EndX=-2.5 EndY=-27.7 EndZ=0
    g17: LineSegment StartX=-8.5 StartY=-4.3 StartZ=0 EndX=-8.5 EndY=-33.9 EndZ=0
    g18: LineSegment StartX=-5.5 StartY=-10.5 StartZ=0 EndX=-5.5 EndY=-27.7 EndZ=0
    g19: LineSegment StartX=-11.5 StartY=-4.3 StartZ=0 EndX=-11.5 EndY=-33.9 EndZ=0
    g20: LineSegment StartX=-14.6 StartY=-1.8 StartZ=0 EndX=-14.6 EndY=-36.4 EndZ=0
    g21: LineSegment StartX=-17.6 StartY=-1.8 StartZ=0 EndX=-17.6 EndY=-36.4 EndZ=0
    g22: LineSegment StartX=-20.6 StartY=-36.4 StartZ=0 EndX=-20.6 EndY=-1.8 EndZ=0
    g23: LineSegment StartX=-23.6 StartY=-1.8 StartZ=0 EndX=-23.6 EndY=-36.4 EndZ=0
  constraints (48):
    c: Block(g0)
    c: Block(g1)
    c: Block(g2)
    c: Block(g3)
    c: Block(g4)
    c: Block(g5)
    c: Block(g6)
    c: Block(g7)
    c: Block(g8)
    c: Block(g9)
    c: Block(g10)
    c: Block(g11)
    c: Coincident(g12,g1)
    c: Coincident(g12,g2)
    c: Vertical(g12)
    c: Coincident(g13,g1)
    c: Coincident(g13,g2)
    c: Vertical(g13)
    c: Coincident(g14,g11)
    c: Coincident(g14,g7)
    c: Vertical(g14)
    c: Coincident(g15,g11)
    c: Coincident(g15,g7)
    c: Vertical(g15)
    c: Coincident(g16,g0)
    c: Coincident(g16,g3)
    c: Vertical(g16)
    c: Coincident(g17,g4)
    c: Coincident(g17,g8)
    c: Vertical(g17)
    c: Coincident(g18,g0)
    c: Coincident(g18,g3)
    c: Vertical(g18)
    c: Coincident(g19,g4)
    c: Coincident(g19,g8)
    c: Vertical(g19)
    c: Coincident(g20,g5)
    c: Coincident(g20,g9)
    c: Vertical(g20)
    c: Coincident(g21,g5)
    c: Coincident(g21,g9)
    c: Vertical(g21)
    c: Coincident(g22,g10)
    c: Coincident(g22,g6)
    c: Vertical(g22)
    c: Coincident(g23,g6)
    c: Coincident(g23,g10)
    c: Vertical(g23)
FEATURE [Part::Extrusion] Extrude020  label="removeToCreateFanGrillHoles"
  Base = -> Sketch029
  Dir = (0,-1,6e-16)
  DirMode = 2
  FaceMakerClass = Part::FaceMakerBullseye
  LengthFwd = 10
  LengthRev = 0
  Placement = pos=(65.4,44,54.82) rot=(0,0,1;0rad)
  Solid = true
  Symmetric = false
FEATURE [Part::MultiFuse] Fusion055  label="top008"
  Shapes = -> [Cut017,Cut018]
FEATURE [Part::Cut] Cut019  label="top009"
  Base = -> Fusion055
  Tool = -> Extrude020
FEATURE [App::MeasureDistance] Distance003  label="Distance: 71.95 mm"
  Distance = 71.9513
  P1 = (117,38,72)
  P2 = (117,38,0.0487319)
FEATURE [Sketcher::SketchObject] Sketch030
  FullyConstrained = true
  Placement = pos=(117,19,0) rot=(0.57735,0.57735,0.57735;2.0944rad)
  sketch-geometry (48):
    g0: LineSegment StartX=-49.19 StartY=69.25 StartZ=0 EndX=-49.19 EndY=66.25 EndZ=0
    g1: LineSegment StartX=-49.19 StartY=63.5 StartZ=0 EndX=-49.19 EndY=60.5 EndZ=0
    g2: LineSegment StartX=-49.19 StartY=57.75 StartZ=0 EndX=-49.19 EndY=54.75 EndZ=0
    g3: LineSegment StartX=-49.19 StartY=52 StartZ=0 EndX=-49.19 EndY=49 EndZ=0
    g4: LineSegment StartX=-49.19 StartY=46.25 StartZ=0 EndX=-49.19 EndY=43.25 EndZ=0
    g5: LineSegment StartX=-49.19 StartY=40.5 StartZ=0 EndX=-49.19 EndY=37.5 EndZ=0
    g6: LineSegment StartX=-49.19 StartY=34.5 StartZ=0 EndX=-49.19 EndY=31.5 EndZ=0
    g7: LineSegment StartX=-49.19 StartY=28.75 StartZ=0 EndX=-49.19 EndY=25.75 EndZ=0
    g8: LineSegment StartX=-49.19 StartY=23 StartZ=0 EndX=-49.19 EndY=20 EndZ=0
    g9: LineSegment StartX=-49.19 StartY=17.25 StartZ=0 EndX=-49.19 EndY=14.25 EndZ=0
    g10: LineSegment StartX=-49.19 StartY=11.5 StartZ=0 EndX=-49.19 EndY=8.5 EndZ=0
    g11: LineSegment StartX=-49.19 StartY=5.75 StartZ=0 EndX=-49.19 EndY=2.75 EndZ=0
    g12: ArcOfCircle CenterX=-1.5 CenterY=67.75 CenterZ=0 NormalX=0 NormalY=0 NormalZ=1 AngleXU=0 Radius=1.5 StartAngle=4.71239 EndAngle=7.85398
    g13: ArcOfCircle CenterX=-1.5 CenterY=62 CenterZ=0 NormalX=0 NormalY=0 NormalZ=1 AngleXU=0 Radius=1.5 StartAngle=4.71239 EndAngle=7.85398
    g14: ArcOfCircle CenterX=-1.5 CenterY=56.25 CenterZ=0 NormalX=0 NormalY=0 NormalZ=1 AngleXU=0 Radius=1.5 StartAngle=4.71239 EndAngle=7.85398
    g15: ArcOfCircle CenterX=-11.49 CenterY=50.5 CenterZ=0 NormalX=0 NormalY=0 NormalZ=1 AngleXU=0 Radius=1.5 StartAngle=4.71239 EndAngle=7.85398
    g16: ArcOfCircle CenterX=-16.28 CenterY=44.75 CenterZ=0 NormalX=0 NormalY=0 NormalZ=1 AngleXU=0 Radius=1.5 StartAngle=4.71239 EndAngle=7.85398
    g17: ArcOfCircle CenterX=-18.2337 CenterY=39 CenterZ=0 NormalX=0 NormalY=0 NormalZ=1 AngleXU=0 Radius=1.5 StartAngle=4.71485 EndAngle=7.85398
    g18: ArcOfCircle CenterX=-16.2837 CenterY=27.25 CenterZ=0 NormalX=0 NormalY=0 NormalZ=1 AngleXU=0 Radius=1.5 StartAngle=4.71485 EndAngle=7.85398
    g19: ArcOfCircle CenterX=-18.2337 CenterY=33 CenterZ=0 NormalX=0 NormalY=0 NormalZ=1 AngleXU=0 Radius=1.5 StartAngle=4.71485 EndAngle=7.85398
    g20: ArcOfCircle CenterX=-11.49 CenterY=21.5 CenterZ=0 NormalX=0 NormalY=0 NormalZ=1 AngleXU=0 Radius=1.5 StartAngle=4.71239 EndAngle=7.85398
    g21: ArcOfCircle CenterX=-1.5 CenterY=4.25 CenterZ=0 NormalX=0 NormalY=0 NormalZ=1 AngleXU=0 Radius=1.5 StartAngle=4.71239 EndAngle=7.85398
    g22: ArcOfCircle CenterX=-1.5 CenterY=10 CenterZ=0 NormalX=0 NormalY=0 NormalZ=1 AngleXU=0 Radius=1.5 StartAngle=4.71239 EndAngle=7.85398
    g23: ArcOfCircle CenterX=-1.5 CenterY=15.75 CenterZ=0 NormalX=0 NormalY=0 NormalZ=1 AngleXU=0 Radius=1.5 StartAngle=4.71239 EndAngle=7.85398
    g24: LineSegment StartX=-49.19 StartY=69.25 StartZ=0 EndX=-1.5 EndY=69.25 EndZ=0
    g25: LineSegment StartX=-49.19 StartY=66.25 StartZ=0 EndX=-1.5 EndY=66.25 EndZ=0
    g26: LineSegment StartX=-49.19 StartY=63.5 StartZ=0 EndX=-1.5 EndY=63.5 EndZ=0
    g27: LineSegment StartX=-49.19 StartY=60.5 StartZ=0 EndX=-1.5 EndY=60.5 EndZ=0
    g28: LineSegment StartX=-49.19 StartY=57.75 StartZ=0 EndX=-1.5 EndY=57.75 EndZ=0
    g29: LineSegment StartX=-49.19 StartY=54.75 StartZ=0 EndX=-1.5 EndY=54.75 EndZ=0
    g30: LineSegment StartX=-49.19 StartY=52 StartZ=0 EndX=-11.49 EndY=52 EndZ=0
    g31: LineSegment StartX=-49.19 StartY=49 StartZ=0 EndX=-11.49 EndY=49 EndZ=0
    g32: LineSegment StartX=-49.19 StartY=46.25 StartZ=0 EndX=-16.28 EndY=46.25 EndZ=0
    g33: LineSegment StartX=-49.19 StartY=43.25 StartZ=0 EndX=-16.28 EndY=43.25 EndZ=0
    g34: LineSegment StartX=-49.19 StartY=40.5 StartZ=0 EndX=-18.2337 EndY=40.5 EndZ=0
    g35: LineSegment StartX=-49.19 StartY=37.5 StartZ=0 EndX=-18.23 EndY=37.5 EndZ=0
    g36: LineSegment StartX=-49.19 StartY=34.5 StartZ=0 EndX=-18.2337 EndY=34.5 EndZ=0
    g37: LineSegment StartX=-49.19 StartY=31.5 StartZ=0 EndX=-18.23 EndY=31.5 EndZ=0
    g38: LineSegment StartX=-49.19 StartY=28.75 StartZ=0 EndX=-16.2837 EndY=28.75 EndZ=0
    g39: LineSegment StartX=-49.19 StartY=25.75 StartZ=0 EndX=-16.28 EndY=25.75 EndZ=0
    g40: LineSegment StartX=-49.19 StartY=23 StartZ=0 EndX=-11.49 EndY=23 EndZ=0
    g41: LineSegment StartX=-49.19 StartY=20 StartZ=0 EndX=-11.49 EndY=20 EndZ=0
    g42: LineSegment StartX=-49.19 StartY=17.25 StartZ=0 EndX=-1.5 EndY=17.25 EndZ=0
    g43: LineSegment StartX=-49.19 StartY=14.25 StartZ=0 EndX=-1.5 EndY=14.25 EndZ=0
    g44: LineSegment StartX=-49.19 StartY=11.5 StartZ=0 EndX=-1.5 EndY=11.5 EndZ=0
    g45: LineSegment StartX=-49.19 StartY=8.5 StartZ=0 EndX=-1.5 EndY=8.5 EndZ=0
    g46: LineSegment StartX=-49.19 StartY=5.75 StartZ=0 EndX=-1.5 EndY=5.75 EndZ=0
    g47: LineSegment StartX=-49.19 StartY=2.75 StartZ=0 EndX=-1.5 EndY=2.75 EndZ=0
  constraints (120):
    c: Vertical(g0)
    c: Distance(g0) = 3
    c: Block(g0)
    c: Vertical(g1)
    c: Distance(g1) = 3
    c: Vertical(g2)
    c: Equal(g0,g2) = 3
    c: Block(g2)
    c: Vertical(g3)
    c: Equal(g1,g3) = 3
    c: Vertical(g4)
    c: Equal(g0,g4) = 3
    c: Block(g4)
    c: Vertical(g5)
    c: Equal(g1,g5) = 3
    c: Vertical(g6)
    c: Equal(g0,g6) = 3
    c: Block(g6)
    c: Vertical(g7)
    c: Equal(g1,g7) = 3
    c: Vertical(g8)
    c: Equal(g0,g8) = 3
    c: Block(g8)
    c: Vertical(g9)
    c: Equal(g1,g9) = 3
    c: Vertical(g10)
    c: Equal(g0,g10) = 3
    c: Block(g10)
    c: Vertical(g11)
    c: Equal(g1,g11) = 3
    c: Block(g12)
    c: Block(g13)
    c: Block(g14)
    c: Block(g15)
    c: Block(g16)
    c: Block(g17)
    c: Block(g18)
    c: Block(g19)
    c: Block(g20)
    c: Block(g21)
    c: Block(g22)
    c: Block(g23)
    c: Block(g11)
    c: Block(g9)
    c: Block(g7)
    c: Block(g5)
    c: Block(g3)
    c: Block(g1)
    c: Coincident(g24,g0)
    c: Coincident(g24,g12)
    c: Horizontal(g24)
    c: Coincident(g25,g0)
    c: Coincident(g25,g12)
    c: Horizontal(g25)
    c: Coincident(g26,g1)
    c: Coincident(g26,g13)
    c: Horizontal(g26)
    c: Coincident(g27,g1)
    c: Coincident(g27,g13)
    c: Horizontal(g27)
    c: Coincident(g28,g2)
    c: Coincident(g28,g14)
    c: Horizontal(g28)
    c: Coincident(g29,g2)
    c: Coincident(g29,g14)
    c: Horizontal(g29)
    c: Coincident(g30,g3)
    c: Coincident(g30,g15)
    c: Horizontal(g30)
    c: Coincident(g31,g3)
    c: Coincident(g31,g15)
    c: Horizontal(g31)
    c: Coincident(g32,g4)
    c: Coincident(g32,g16)
    c: Horizontal(g32)
    c: Coincident(g33,g4)
    c: Coincident(g33,g16)
    c: Horizontal(g33)
    c: Coincident(g34,g5)
    c: Coincident(g34,g17)
    c: Horizontal(g34)
    c: Coincident(g35,g5)
    c: Coincident(g35,g17)
    c: Horizontal(g35)
    c: Coincident(g36,g6)
    c: Coincident(g36,g19)
    c: Horizontal(g36)
    c: Coincident(g37,g6)
    c: Coincident(g37,g19)
    c: Horizontal(g37)
    c: Coincident(g38,g7)
    c: Coincident(g38,g18)
    c: Horizontal(g38)
    c: Coincident(g39,g7)
    c: Coincident(g39,g18)
    c: Horizontal(g39)
    c: Coincident(g40,g8)
    c: Coincident(g40,g20)
    c: Horizontal(g40)
    c: Coincident(g41,g8)
    c: Coincident(g41,g20)
    c: Horizontal(g41)
    c: Coincident(g42,g9)
    c: Coincident(g42,g23)
    c: Horizontal(g42)
    c: Coincident(g43,g9)
    c: Coincident(g43,g23)
    c: Horizontal(g43)
    c: Coincident(g44,g10)
    c: Coincident(g44,g22)
    c: Horizontal(g44)
    c: Coincident(g45,g10)
    c: Coincident(g45,g22)
    c: Horizontal(g45)
    c: Coincident(g46,g11)
    c: Coincident(g46,g21)
    c: Horizontal(g46)
    c: Coincident(g47,g11)
    c: Coincident(g47,g21)
    c: Horizontal(g47)
FEATURE [Sketcher::SketchObject] Sketch031
  FullyConstrained = true
  Placement = pos=(117,19,0) rot=(0.57735,0.57735,0.57735;2.0944rad)
  sketch-geometry (24):
    g0: ArcOfCircle CenterX=-49.19 CenterY=67.75 CenterZ=0 NormalX=0 NormalY=0 NormalZ=1 AngleXU=0 Radius=1.5 StartAngle=1.5708 EndAngle=4.71239
    g1: ArcOfCircle CenterX=-49.19 CenterY=62 CenterZ=0 NormalX=0 NormalY=0 NormalZ=1 AngleXU=0 Radius=1.5 StartAngle=1.5708 EndAngle=4.71239
    g2: ArcOfCircle CenterX=-49.19 CenterY=56.25 CenterZ=0 NormalX=0 NormalY=0 NormalZ=1 AngleXU=0 Radius=1.5 StartAngle=1.5708 EndAngle=4.71239
    g3: ArcOfCircle CenterX=-49.19 CenterY=50.5 CenterZ=0 NormalX=0 NormalY=0 NormalZ=1 AngleXU=0 Radius=1.5 StartAngle=1.5708 EndAngle=4.71239
    g4: ArcOfCircle CenterX=-49.19 CenterY=44.75 CenterZ=0 NormalX=0 NormalY=0 NormalZ=1 AngleXU=0 Radius=1.5 StartAngle=1.5708 EndAngle=4.71239
    g5: ArcOfCircle CenterX=-49.19 CenterY=39 CenterZ=0 NormalX=0 NormalY=0 NormalZ=1 AngleXU=0 Radius=1.5 StartAngle=1.5708 EndAngle=4.71239
    g6: ArcOfCircle CenterX=-49.19 CenterY=33 CenterZ=0 NormalX=0 NormalY=0 NormalZ=1 AngleXU=0 Radius=1.5 StartAngle=1.5708 EndAngle=4.71239
    g7: ArcOfCircle CenterX=-49.19 CenterY=27.25 CenterZ=0 NormalX=0 NormalY=0 NormalZ=1 AngleXU=0 Radius=1.5 StartAngle=1.5708 EndAngle=4.71239
    g8: ArcOfCircle CenterX=-49.19 CenterY=21.5 CenterZ=0 NormalX=0 NormalY=0 NormalZ=1 AngleXU=0 Radius=1.5 StartAngle=1.5708 EndAngle=4.71239
    g9: ArcOfCircle CenterX=-49.19 CenterY=15.75 CenterZ=0 NormalX=0 NormalY=0 NormalZ=1 AngleXU=0 Radius=1.5 StartAngle=1.5708 EndAngle=4.71239
    g10: ArcOfCircle CenterX=-49.19 CenterY=10 CenterZ=0 NormalX=0 NormalY=0 NormalZ=1 AngleXU=0 Radius=1.5 StartAngle=1.5708 EndAngle=4.71239
    g11: ArcOfCircle CenterX=-49.19 CenterY=4.25 CenterZ=0 NormalX=0 NormalY=0 NormalZ=1 AngleXU=0 Radius=1.5 StartAngle=1.5708 EndAngle=4.71239
    g12: LineSegment StartX=-49.19 StartY=69.25 StartZ=0 EndX=-49.19 EndY=66.25 EndZ=0
    g13: LineSegment StartX=-49.19 StartY=63.5 StartZ=0 EndX=-49.19 EndY=60.5 EndZ=0
    g14: LineSegment StartX=-49.19 StartY=57.75 StartZ=0 EndX=-49.19 EndY=54.75 EndZ=0
    g15: LineSegment StartX=-49.19 StartY=52 StartZ=0 EndX=-49.19 EndY=49 EndZ=0
    g16: LineSegment StartX=-49.19 StartY=46.25 StartZ=0 EndX=-49.19 EndY=43.25 EndZ=0
    g17: LineSegment StartX=-49.19 StartY=40.5 StartZ=0 EndX=-49.19 EndY=37.5 EndZ=0
    g18: LineSegment StartX=-49.19 StartY=34.5 StartZ=0 EndX=-49.19 EndY=31.5 EndZ=0
    g19: LineSegment StartX=-49.19 StartY=28.75 StartZ=0 EndX=-49.19 EndY=25.75 EndZ=0
    g20: LineSegment StartX=-49.19 StartY=23 StartZ=0 EndX=-49.19 EndY=20 EndZ=0
    g21: LineSegment StartX=-49.19 StartY=17.25 StartZ=0 EndX=-49.19 EndY=14.25 EndZ=0
    g22: LineSegment StartX=-49.19 StartY=11.5 StartZ=0 EndX=-49.19 EndY=8.5 EndZ=0
    g23: LineSegment StartX=-49.19 StartY=5.75 StartZ=0 EndX=-49.19 EndY=2.75 EndZ=0
  constraints (48):
    c: Block(g0)
    c: Block(g1)
    c: Block(g2)
    c: Block(g3)
    c: Block(g4)
    c: Block(g5)
    c: Block(g6)
    c: Block(g7)
    c: Block(g8)
    c: Block(g9)
    c: Block(g10)
    c: Block(g11)
    c: Coincident(g12,g0)
    c: Coincident(g12,g0)
    c: Vertical(g12)
    c: Vertical(g13)
    c: Coincident(g13,g1)
    c: Vertical(g14)
    c: Coincident(g14,g2)
    c: Vertical(g15)
    c: Coincident(g15,g3)
    c: Vertical(g16)
    c: Coincident(g16,g4)
    c: Vertical(g17)
    c: Coincident(g17,g5)
    c: Vertical(g18)
    c: Coincident(g18,g6)
    c: Vertical(g19)
    c: Coincident(g19,g7)
    c: Vertical(g20)
    c: Coincident(g20,g8)
    c: Vertical(g21)
    c: Coincident(g21,g9)
    c: Vertical(g22)
    c: Coincident(g22,g10)
    c: Vertical(g23)
    c: Coincident(g23,g11)
    c: Block(g23)
    c: Block(g22)
    c: Block(g21)
    c: Block(g20)
    c: Block(g13)
    c: Block(g14)
    c: Block(g15)
    c: Block(g16)
    c: Block(g17)
    c: Block(g18)
    c: Block(g19)
FEATURE [Part::Extrusion] Extrude022
  Base = -> Sketch030
  Dir = (1,-2e-16,2e-16)
  DirMode = 2
  FaceMakerClass = Part::FaceMakerBullseye
  LengthFwd = 19
  LengthRev = 0
  Placement = pos=(-19,0,0) rot=(0,0,1;0rad)
  Solid = true
  Symmetric = false
FEATURE [Part::Fillet] Fillet022
  Base = -> Extrude022
  Edges = 24 edges r=1.49: [Edge6,Edge11,Edge18,Edge23,Edge30,Edge35,Edge42,Edge47,Edge54,Edge59,Edge66,Edge71,Edge78,Edge83,Edge90,Edge95,Edge102,Edge107,Edge114,Edge119,Edge126,Edge131,Edge138,Edge143]
FEATURE [Part::Cut] Cut020  label="top010"
  Base = -> Cut019
  Tool = -> Fillet022
FEATURE [Sketcher::SketchObject] Sketch032
  FullyConstrained = true
  Placement = pos=(117,19,0) rot=(0.57735,0.57735,0.57735;2.0944rad)
  sketch-geometry (48):
    g0: LineSegment StartX=-49.19 StartY=69.25 StartZ=0 EndX=-49.19 EndY=66.25 EndZ=0
    g1: LineSegment StartX=-49.19 StartY=63.5 StartZ=0 EndX=-49.19 EndY=60.5 EndZ=0
    g2: LineSegment StartX=-49.19 StartY=57.75 StartZ=0 EndX=-49.19 EndY=54.75 EndZ=0
    g3: LineSegment StartX=-49.19 StartY=52 StartZ=0 EndX=-49.19 EndY=49 EndZ=0
    g4: LineSegment StartX=-49.19 StartY=46.25 StartZ=0 EndX=-49.19 EndY=43.25 EndZ=0
    g5: LineSegment StartX=-49.19 StartY=40.5 StartZ=0 EndX=-49.19 EndY=37.5 EndZ=0
    g6: LineSegment StartX=-49.19 StartY=34.5 StartZ=0 EndX=-49.19 EndY=31.5 EndZ=0
    g7: LineSegment StartX=-49.19 StartY=28.75 StartZ=0 EndX=-49.19 EndY=25.75 EndZ=0
    g8: LineSegment StartX=-49.19 StartY=23 StartZ=0 EndX=-49.19 EndY=20 EndZ=0
    g9: LineSegment StartX=-49.19 StartY=17.25 StartZ=0 EndX=-49.19 EndY=14.25 EndZ=0
    g10: LineSegment StartX=-49.19 StartY=11.5 StartZ=0 EndX=-49.19 EndY=8.5 EndZ=0
    g11: LineSegment StartX=-49.19 StartY=5.75 StartZ=0 EndX=-49.19 EndY=2.75 EndZ=0
    g12: ArcOfCircle CenterX=-1.5 CenterY=67.75 CenterZ=0 NormalX=0 NormalY=0 NormalZ=1 AngleXU=0 Radius=1.5 StartAngle=4.71239 EndAngle=7.85398
    g13: ArcOfCircle CenterX=-1.5 CenterY=62 CenterZ=0 NormalX=0 NormalY=0 NormalZ=1 AngleXU=0 Radius=1.5 StartAngle=4.71239 EndAngle=7.85398
    g14: ArcOfCircle CenterX=-1.5 CenterY=56.25 CenterZ=0 NormalX=0 NormalY=0 NormalZ=1 AngleXU=0 Radius=1.5 StartAngle=4.71239 EndAngle=7.85398
    g15: ArcOfCircle CenterX=-11.49 CenterY=50.5 CenterZ=0 NormalX=0 NormalY=0 NormalZ=1 AngleXU=0 Radius=1.5 StartAngle=4.71239 EndAngle=7.85398
    g16: ArcOfCircle CenterX=-16.28 CenterY=44.75 CenterZ=0 NormalX=0 NormalY=0 NormalZ=1 AngleXU=0 Radius=1.5 StartAngle=4.71239 EndAngle=7.85398
    g17: ArcOfCircle CenterX=-18.2337 CenterY=39 CenterZ=0 NormalX=0 NormalY=0 NormalZ=1 AngleXU=0 Radius=1.5 StartAngle=4.71485 EndAngle=7.85398
    g18: ArcOfCircle CenterX=-16.2837 CenterY=27.25 CenterZ=0 NormalX=0 NormalY=0 NormalZ=1 AngleXU=0 Radius=1.5 StartAngle=4.71485 EndAngle=7.85398
    g19: ArcOfCircle CenterX=-18.2337 CenterY=33 CenterZ=0 NormalX=0 NormalY=0 NormalZ=1 AngleXU=0 Radius=1.5 StartAngle=4.71485 EndAngle=7.85398
    g20: ArcOfCircle CenterX=-11.49 CenterY=21.5 CenterZ=0 NormalX=0 NormalY=0 NormalZ=1 AngleXU=0 Radius=1.5 StartAngle=4.71239 EndAngle=7.85398
    g21: ArcOfCircle CenterX=-1.5 CenterY=4.25 CenterZ=0 NormalX=0 NormalY=0 NormalZ=1 AngleXU=0 Radius=1.5 StartAngle=4.71239 EndAngle=7.85398
    g22: ArcOfCircle CenterX=-1.5 CenterY=10 CenterZ=0 NormalX=0 NormalY=0 NormalZ=1 AngleXU=0 Radius=1.5 StartAngle=4.71239 EndAngle=7.85398
    g23: ArcOfCircle CenterX=-1.5 CenterY=15.75 CenterZ=0 NormalX=0 NormalY=0 NormalZ=1 AngleXU=0 Radius=1.5 StartAngle=4.71239 EndAngle=7.85398
    g24: LineSegment StartX=-49.19 StartY=69.25 StartZ=0 EndX=-1.5 EndY=69.25 EndZ=0
    g25: LineSegment StartX=-49.19 StartY=66.25 StartZ=0 EndX=-1.5 EndY=66.25 EndZ=0
    g26: LineSegment StartX=-49.19 StartY=63.5 StartZ=0 EndX=-1.5 EndY=63.5 EndZ=0
    g27: LineSegment StartX=-49.19 StartY=60.5 StartZ=0 EndX=-1.5 EndY=60.5 EndZ=0
    g28: LineSegment StartX=-49.19 StartY=57.75 StartZ=0 EndX=-1.5 EndY=57.75 EndZ=0
    g29: LineSegment StartX=-49.19 StartY=54.75 StartZ=0 EndX=-1.5 EndY=54.75 EndZ=0
    g30: LineSegment StartX=-49.19 StartY=52 StartZ=0 EndX=-11.49 EndY=52 EndZ=0
    g31: LineSegment StartX=-49.19 StartY=49 StartZ=0 EndX=-11.49 EndY=49 EndZ=0
    g32: LineSegment StartX=-49.19 StartY=46.25 StartZ=0 EndX=-16.28 EndY=46.25 EndZ=0
    g33: LineSegment StartX=-49.19 StartY=43.25 StartZ=0 EndX=-16.28 EndY=43.25 EndZ=0
    g34: LineSegment StartX=-49.19 StartY=40.5 StartZ=0 EndX=-18.2337 EndY=40.5 EndZ=0
    g35: LineSegment StartX=-49.19 StartY=37.5 StartZ=0 EndX=-18.23 EndY=37.5 EndZ=0
    g36: LineSegment StartX=-49.19 StartY=34.5 StartZ=0 EndX=-18.2337 EndY=34.5 EndZ=0
    g37: LineSegment StartX=-49.19 StartY=31.5 StartZ=0 EndX=-18.23 EndY=31.5 EndZ=0
    g38: LineSegment StartX=-49.19 StartY=28.75 StartZ=0 EndX=-16.2837 EndY=28.75 EndZ=0
    g39: LineSegment StartX=-49.19 StartY=25.75 StartZ=0 EndX=-16.28 EndY=25.75 EndZ=0
    g40: LineSegment StartX=-49.19 StartY=23 StartZ=0 EndX=-11.49 EndY=23 EndZ=0
    g41: LineSegment StartX=-49.19 StartY=20 StartZ=0 EndX=-11.49 EndY=20 EndZ=0
    g42: LineSegment StartX=-49.19 StartY=17.25 StartZ=0 EndX=-1.5 EndY=17.25 EndZ=0
    g43: LineSegment StartX=-49.19 StartY=14.25 StartZ=0 EndX=-1.5 EndY=14.25 EndZ=0
    g44: LineSegment StartX=-49.19 StartY=11.5 StartZ=0 EndX=-1.5 EndY=11.5 EndZ=0
    g45: LineSegment StartX=-49.19 StartY=8.5 StartZ=0 EndX=-1.5 EndY=8.5 EndZ=0
    g46: LineSegment StartX=-49.19 StartY=5.75 StartZ=0 EndX=-1.5 EndY=5.75 EndZ=0
    g47: LineSegment StartX=-49.19 StartY=2.75 StartZ=0 EndX=-1.5 EndY=2.75 EndZ=0
  constraints (120):
    c: Vertical(g0)
    c: Distance(g0) = 3
    c: Block(g0)
    c: Vertical(g1)
    c: Distance(g1) = 3
    c: Vertical(g2)
    c: Equal(g0,g2) = 3
    c: Block(g2)
    c: Vertical(g3)
    c: Equal(g1,g3) = 3
    c: Vertical(g4)
    c: Equal(g0,g4) = 3
    c: Block(g4)
    c: Vertical(g5)
    c: Equal(g1,g5) = 3
    c: Vertical(g6)
    c: Equal(g0,g6) = 3
    c: Block(g6)
    c: Vertical(g7)
    c: Equal(g1,g7) = 3
    c: Vertical(g8)
    c: Equal(g0,g8) = 3
    c: Block(g8)
    c: Vertical(g9)
    c: Equal(g1,g9) = 3
    c: Vertical(g10)
    c: Equal(g0,g10) = 3
    c: Block(g10)
    c: Vertical(g11)
    c: Equal(g1,g11) = 3
    c: Block(g12)
    c: Block(g13)
    c: Block(g14)
    c: Block(g15)
    c: Block(g16)
    c: Block(g17)
    c: Block(g18)
    c: Block(g19)
    c: Block(g20)
    c: Block(g21)
    c: Block(g22)
    c: Block(g23)
    c: Block(g11)
    c: Block(g9)
    c: Block(g7)
    c: Block(g5)
    c: Block(g3)
    c: Block(g1)
    c: Coincident(g24,g0)
    c: Coincident(g24,g12)
    c: Horizontal(g24)
    c: Coincident(g25,g0)
    c: Coincident(g25,g12)
    c: Horizontal(g25)
    c: Coincident(g26,g1)
    c: Coincident(g26,g13)
    c: Horizontal(g26)
    c: Coincident(g27,g1)
    c: Coincident(g27,g13)
    c: Horizontal(g27)
    c: Coincident(g28,g2)
    c: Coincident(g28,g14)
    c: Horizontal(g28)
    c: Coincident(g29,g2)
    c: Coincident(g29,g14)
    c: Horizontal(g29)
    c: Coincident(g30,g3)
    c: Coincident(g30,g15)
    c: Horizontal(g30)
    c: Coincident(g31,g3)
    c: Coincident(g31,g15)
    c: Horizontal(g31)
    c: Coincident(g32,g4)
    c: Coincident(g32,g16)
    c: Horizontal(g32)
    c: Coincident(g33,g4)
    c: Coincident(g33,g16)
    c: Horizontal(g33)
    c: Coincident(g34,g5)
    c: Coincident(g34,g17)
    c: Horizontal(g34)
    c: Coincident(g35,g5)
    c: Coincident(g35,g17)
    c: Horizontal(g35)
    c: Coincident(g36,g6)
    c: Coincident(g36,g19)
    c: Horizontal(g36)
    c: Coincident(g37,g6)
    c: Coincident(g37,g19)
    c: Horizontal(g37)
    c: Coincident(g38,g7)
    c: Coincident(g38,g18)
    c: Horizontal(g38)
    c: Coincident(g39,g7)
    c: Coincident(g39,g18)
    c: Horizontal(g39)
    c: Coincident(g40,g8)
    c: Coincident(g40,g20)
    c: Horizontal(g40)
    c: Coincident(g41,g8)
    c: Coincident(g41,g20)
    c: Horizontal(g41)
    c: Coincident(g42,g9)
    c: Coincident(g42,g23)
    c: Horizontal(g42)
    c: Coincident(g43,g9)
    c: Coincident(g43,g23)
    c: Horizontal(g43)
    c: Coincident(g44,g10)
    c: Coincident(g44,g22)
    c: Horizontal(g44)
    c: Coincident(g45,g10)
    c: Coincident(g45,g22)
    c: Horizontal(g45)
    c: Coincident(g46,g11)
    c: Coincident(g46,g21)
    c: Horizontal(g46)
    c: Coincident(g47,g11)
    c: Coincident(g47,g21)
    c: Horizontal(g47)
FEATURE [Part::Extrusion] Extrude023
  Base = -> Sketch032
  Dir = (1,-2e-16,2e-16)
  DirMode = 2
  FaceMakerClass = Part::FaceMakerBullseye
  LengthFwd = 19
  LengthRev = 0
  Placement = pos=(-19,0,0) rot=(0,0,1;0rad)
  Solid = true
  Symmetric = false
FEATURE [Part::Fillet] Fillet023
  Base = -> Extrude023
  Edges = 24 edges r=1.49: [Edge6,Edge11,Edge18,Edge23,Edge30,Edge35,Edge42,Edge47,Edge54,Edge59,Edge66,Edge71,Edge78,Edge83,Edge90,Edge95,Edge102,Edge107,Edge114,Edge119,Edge126,Edge131,Edge138,Edge143]
  Placement = pos=(0,0.05,0) rot=(0,0,1;0rad)
FEATURE [Part::Cut] Cut014  label="bottom003"
  Base = -> Cut007
  Tool = -> Fusion047
FEATURE [Part::Cut] Cut021  label="bottom004"
  Base = -> Cut014
  Tool = -> Fillet023
FEATURE [Sketcher::SketchObject] Sketch033
  FullyConstrained = true
  Placement = pos=(117,19,0) rot=(0.57735,0.57735,0.57735;2.0944rad)
  sketch-geometry (8):
    g0: LineSegment StartX=-49.19 StartY=69.25 StartZ=0 EndX=-49.19 EndY=66.25 EndZ=0
    g1: LineSegment StartX=-49.19 StartY=5.75 StartZ=0 EndX=-49.19 EndY=2.75 EndZ=0
    g2: ArcOfCircle CenterX=-1.5 CenterY=67.75 CenterZ=0 NormalX=0 NormalY=0 NormalZ=1 AngleXU=0 Radius=1.5 StartAngle=4.71239 EndAngle=7.85398
    g3: ArcOfCircle CenterX=-1.5 CenterY=4.25 CenterZ=0 NormalX=0 NormalY=0 NormalZ=1 AngleXU=0 Radius=1.5 StartAngle=4.71239 EndAngle=7.85398
    g4: LineSegment StartX=-49.19 StartY=69.25 StartZ=0 EndX=-1.5 EndY=69.25 EndZ=0
    g5: LineSegment StartX=-49.19 StartY=66.25 StartZ=0 EndX=-1.5 EndY=66.25 EndZ=0
    g6: LineSegment StartX=-49.19 StartY=5.75 StartZ=0 EndX=-1.5 EndY=5.75 EndZ=0
    g7: LineSegment StartX=-49.19 StartY=2.75 StartZ=0 EndX=-1.5 EndY=2.75 EndZ=0
  constraints (19):
    c: Vertical(g0)
    c: Distance(g0) = 3
    c: Block(g0)
    c: Vertical(g1)
    c: Block(g2)
    c: Block(g3)
    c: Block(g1)
    c: Coincident(g4,g0)
    c: Coincident(g4,g2)
    c: Horizontal(g4)
    c: Coincident(g5,g0)
    c: Coincident(g5,g2)
    c: Horizontal(g5)
    c: Coincident(g6,g1)
    c: Coincident(g6,g3)
    c: Horizontal(g6)
    c: Coincident(g7,g1)
    c: Coincident(g7,g3)
    c: Horizontal(g7)
FEATURE [Sketcher::SketchObject] Sketch034
  FullyConstrained = true
  Placement = pos=(117,19,0) rot=(0.57735,0.57735,0.57735;2.0944rad)
  sketch-geometry (8):
    g0: LineSegment StartX=-49.19 StartY=63.5 StartZ=0 EndX=-49.19 EndY=60.5 EndZ=0
    g1: LineSegment StartX=-49.19 StartY=11.5 StartZ=0 EndX=-49.19 EndY=8.5 EndZ=0
    g2: ArcOfCircle CenterX=-1.5 CenterY=62 CenterZ=0 NormalX=0 NormalY=0 NormalZ=1 AngleXU=0 Radius=1.5 StartAngle=4.71239 EndAngle=7.85398
    g3: ArcOfCircle CenterX=-1.5 CenterY=10 CenterZ=0 NormalX=0 NormalY=0 NormalZ=1 AngleXU=0 Radius=1.5 StartAngle=4.71239 EndAngle=7.85398
    g4: LineSegment StartX=-49.19 StartY=63.5 StartZ=0 EndX=-1.5 EndY=63.5 EndZ=0
    g5: LineSegment StartX=-49.19 StartY=60.5 StartZ=0 EndX=-1.5 EndY=60.5 EndZ=0
    g6: LineSegment StartX=-49.19 StartY=11.5 StartZ=0 EndX=-1.5 EndY=11.5 EndZ=0
    g7: LineSegment StartX=-49.19 StartY=8.5 StartZ=0 EndX=-1.5 EndY=8.5 EndZ=0
  constraints (19):
    c: Vertical(g0)
    c: Distance(g0) = 3
    c: Vertical(g1)
    c: Block(g1)
    c: Block(g2)
    c: Block(g3)
    c: Block(g0)
    c: Coincident(g4,g0)
    c: Coincident(g4,g2)
    c: Horizontal(g4)
    c: Coincident(g5,g0)
    c: Coincident(g5,g2)
    c: Horizontal(g5)
    c: Coincident(g6,g1)
    c: Coincident(g6,g3)
    c: Horizontal(g6)
    c: Coincident(g7,g1)
    c: Coincident(g7,g3)
    c: Horizontal(g7)
FEATURE [Part::Extrusion] Extrude024
  Base = -> Sketch033
  Dir = (1,0,0)
  DirMode = 2
  FaceMakerClass = Part::FaceMakerBullseye
  LengthFwd = 10
  LengthRev = 0
  Solid = true
  Symmetric = false
FEATURE [Part::Extrusion] Extrude025
  Base = -> Sketch034
  Dir = (1,0,0)
  DirMode = 2
  FaceMakerClass = Part::FaceMakerBullseye
  LengthFwd = 10
  LengthRev = 0
  Solid = true
  Symmetric = false
FEATURE [Part::Fillet] Fillet024  label="removeFromtMoreFrontCaseScrewRetainers"
  Base = -> Extrude024
  Edges = 4 edges r=1.49: [Edge6,Edge11,Edge18,Edge23]
  Placement = pos=(-11,0,0) rot=(0,0,1;0rad)
FEATURE [Part::Fillet] Fillet025  label="removeFromtMoreFrontCaseScrewRetainers001"
  Base = -> Extrude025
  Edges = 4 edges r=1.49: [Edge6,Edge11,Edge18,Edge23]
  Placement = pos=(-19,0,0) rot=(0,0,1;0rad)
FEATURE [Part::Cut] Cut022
  Base = -> Cut015
  Tool = -> Fillet025
FEATURE [Part::Cut] Cut023  label="screwRetainers"
  Base = -> Cut022
  Tool = -> Fillet024
FEATURE [Part::MultiFuse] Fusion056  label="bottom005"
  Shapes = -> [Fusion044,Cut021]
FEATURE [Part::MultiFuse] Fusion057  label="casePillars001"
  Shapes = -> [Cut016,Fusion052]
FEATURE [Part::MultiFuse] Fusion058  label="bottom006"
  Shapes = -> [Fusion056,Cut023]
FEATURE [Part::MultiFuse] Fusion059  label="bottom007"
  Shapes = -> [Fusion058,Fillet005]
FEATURE [Part::MultiFuse] Fusion060  label="bottom008"
  Shapes = -> [Fusion059,Fusion]
FEATURE [Part::MultiFuse] Fusion061  label="top011"
  Shapes = -> [Cut006,Cut020]
FEATURE [Part::MultiFuse] Fusion062  label="top012"
  Shapes = -> [Fusion057,Fusion061]
FEATURE [Sketcher::SketchObject] Sketch035  label="topSketch007"
  FullyConstrained = true
  sketch-geometry (6):
    g0: LineSegment StartX=19 StartY=38 StartZ=0 EndX=117 EndY=38 EndZ=0
    g1: ArcOfCircle CenterX=19 CenterY=19 CenterZ=0 NormalX=0 NormalY=0 NormalZ=1 AngleXU=0 Radius=19 StartAngle=1.5708 EndAngle=3.14159
    g2: LineSegment StartX=117 StartY=38 StartZ=0 EndX=117 EndY=19 EndZ=0
    g3: LineSegment StartX=98 StartY=1.0161e-12 StartZ=0 EndX=5.22862e-06 EndY=1.0161e-12 EndZ=0
    g4: LineSegment StartX=5.22862e-06 StartY=19 StartZ=0 EndX=5.22862e-06 EndY=1.0161e-12 EndZ=0
    g5: ArcOfCircle CenterX=98 CenterY=19 CenterZ=0 NormalX=0 NormalY=0 NormalZ=1 AngleXU=0 Radius=19 StartAngle=4.71239 EndAngle=6.28319
  constraints (16):
    c: Horizontal(g0)
    c: Distance(g0) = 98
    c: Coincident(g1,g0)
    c: Block(g1)
    c: Coincident(g2,g0)
    c: Vertical(g2)
    c: Distance(g2) = 19
    c: Horizontal(g3)
    c: Coincident(g4,g1)
    c: Vertical(g4)
    c: Coincident(g3,g4)
    c: Block(g3)
    c: Coincident(g5,g2)
    c: Coincident(g5,g3)
    c: Block(g0)
    c: Block(g5)
FEATURE [Part::Extrusion] Extrude026  label="sideA001"
  Base = -> Sketch035
  Dir = (0,0,1)
  DirMode = 2
  FaceMakerClass = Part::FaceMakerBullseye
  LengthFwd = 3
  LengthRev = 0
  Placement = pos=(0,0,-2.7) rot=(0,0,1;0rad)
  Solid = true
  Symmetric = false
FEATURE [Sketcher::SketchObject] Sketch036  label="topSketch008"
  FullyConstrained = true
  sketch-geometry (6):
    g0: LineSegment StartX=19 StartY=38 StartZ=0 EndX=117 EndY=38 EndZ=0
    g1: ArcOfCircle CenterX=19 CenterY=19 CenterZ=0 NormalX=0 NormalY=0 NormalZ=1 AngleXU=0 Radius=19 StartAngle=1.5708 EndAngle=3.14159
    g2: LineSegment StartX=117 StartY=38 StartZ=0 EndX=117 EndY=19 EndZ=0
    g3: LineSegment StartX=98 StartY=1.0161e-12 StartZ=0 EndX=5.22862e-06 EndY=1.0161e-12 EndZ=0
    g4: LineSegment StartX=5.22862e-06 StartY=19 StartZ=0 EndX=5.22862e-06 EndY=1.0161e-12 EndZ=0
    g5: ArcOfCircle CenterX=98 CenterY=19 CenterZ=0 NormalX=0 NormalY=0 NormalZ=1 AngleXU=0 Radius=19 StartAngle=4.71239 EndAngle=6.28319
  constraints (16):
    c: Horizontal(g0)
    c: Distance(g0) = 98
    c: Coincident(g1,g0)
    c: Block(g1)
    c: Coincident(g2,g0)
    c: Vertical(g2)
    c: Distance(g2) = 19
    c: Horizontal(g3)
    c: Coincident(g4,g1)
    c: Vertical(g4)
    c: Coincident(g3,g4)
    c: Block(g3)
    c: Coincident(g5,g2)
    c: Coincident(g5,g3)
    c: Block(g0)
    c: Block(g5)
FEATURE [Part::Extrusion] Extrude027  label="sideB001"
  Base = -> Sketch036
  Dir = (0,0,1)
  DirMode = 2
  FaceMakerClass = Part::FaceMakerBullseye
  LengthFwd = 3
  LengthRev = 0
  Placement = pos=(0,0,71.7) rot=(0,0,1;0rad)
  Solid = true
  Symmetric = false
FEATURE [Part::MultiFuse] Fusion064  label="removeFromBottom"
  Shapes = -> [Extrude026,Extrude027]
FEATURE [Part::Cut] Cut024  label="bottom009"
  Base = -> Fusion060
  Tool = -> Fusion064
FEATURE [Sketcher::SketchObject] Sketch037  label="topSketch009"
  FullyConstrained = true
  sketch-geometry (6):
    g0: ArcOfCircle CenterX=19 CenterY=19 CenterZ=0 NormalX=0 NormalY=0 NormalZ=1 AngleXU=0 Radius=19 StartAngle=1.5708 EndAngle=3.14159
    g1: LineSegment StartX=5.22862e-06 StartY=19 StartZ=0 EndX=5.22862e-06 EndY=1.19904e-11 EndZ=0
    g2: LineSegment StartX=19 StartY=38 StartZ=0 EndX=124 EndY=38 EndZ=0
    g3: LineSegment StartX=5.22862e-06 StartY=1.19904e-11 StartZ=0 EndX=105 EndY=1.19904e-11 EndZ=0
    g4: ArcOfCircle CenterX=105 CenterY=19 CenterZ=0 NormalX=0 NormalY=0 NormalZ=1 AngleXU=0 Radius=19 StartAngle=4.71239 EndAngle=6.28319
    g5: LineSegment StartX=124 StartY=38 StartZ=0 EndX=124 EndY=19 EndZ=0
  constraints (16):
    c: Block(g0)
    c: Coincident(g1,g0)
    c: Vertical(g1)
    c: Horizontal(g2)
    c: Distance(g2) = 105
    c: Coincident(g2,g0)
    c: Distance(g1) = 19
    c: Coincident(g3,g1)
    c: Horizontal(g3)
    c: Distance(g3) = 105
    c: Block(g4)
    c: Coincident(g4,g3)
    c: Coincident(g5,g2)
    c: Coincident(g5,g4)
    c: Vertical(g5)
    c: Distance(g5) = 19
FEATURE [Part::Extrusion] Extrude028  label="sideB"
  Base = -> Sketch037
  Dir = (0,0,1)
  DirMode = 2
  FaceMakerClass = Part::FaceMakerBullseye
  LengthFwd = 3
  LengthRev = 0
  Placement = pos=(0,0,72) rot=(0,0,1;0rad)
  Solid = true
  Symmetric = false
FEATURE [Sketcher::SketchObject] Sketch038  label="topSketch010"
  FullyConstrained = true
  sketch-geometry (20):
    g0: LineSegment StartX=5.21097e-06 StartY=3 StartZ=0 EndX=5.21097e-06 EndY=19 EndZ=0
    g1: ArcOfCircle CenterX=19 CenterY=19 CenterZ=0 NormalX=0 NormalY=0 NormalZ=1 AngleXU=0 Radius=19 StartAngle=1.5708 EndAngle=3.14159
    g2: ArcOfCircle CenterX=19 CenterY=19 CenterZ=0 NormalX=0 NormalY=0 NormalZ=1 AngleXU=0 Radius=16 StartAngle=1.5708 EndAngle=3.14159
    g3: LineSegment StartX=114 StartY=35 StartZ=0 EndX=19 EndY=35 EndZ=0
    g4: LineSegment StartX=5.21097e-06 StartY=3 StartZ=0 EndX=5.21097e-06 EndY=0 EndZ=0
    g5: LineSegment StartX=3 StartY=0 StartZ=0 EndX=5.21097e-06 EndY=0 EndZ=0
    g6: LineSegment StartX=3 StartY=19 StartZ=0 EndX=3 EndY=0 EndZ=0
    g7: LineSegment StartX=19 StartY=38 StartZ=0 EndX=124 EndY=38 EndZ=0
    g8: Circle CenterX=119 CenterY=35 CenterZ=0 NormalX=0 NormalY=0 NormalZ=1 AngleXU=0 Radius=1
    g9: Circle CenterX=121 CenterY=35 CenterZ=0 NormalX=0 NormalY=0 NormalZ=1 AngleXU=0 Radius=1
    g10: Circle CenterX=121 CenterY=33 CenterZ=0 NormalX=0 NormalY=0 NormalZ=1 AngleXU=0 Radius=1
    g11: BSplineCurve PolesCount=3 KnotsCount=2 Degree=2 IsPeriodic=0
    g12: GeomPoint X=119 Y=35 Z=0
    g13: GeomPoint X=121 Y=33 Z=0
    g14: LineSegment StartX=119 StartY=35 StartZ=0 EndX=114 EndY=35 EndZ=0
    g15: ArcOfCircle CenterX=105 CenterY=19 CenterZ=0 NormalX=0 NormalY=0 NormalZ=1 AngleXU=0 Radius=19 StartAngle=5.7297 EndAngle=6.28319
    g16: ArcOfCircle CenterX=105 CenterY=19 CenterZ=0 NormalX=0 NormalY=0 NormalZ=1 AngleXU=0 Radius=16 StartAngle=5.60905 EndAngle=6.28319
    g17: LineSegment StartX=121 StartY=33 StartZ=0 EndX=121 EndY=19 EndZ=0
    g18: LineSegment StartX=124 StartY=38 StartZ=0 EndX=124 EndY=19 EndZ=0
    g19: LineSegment StartX=117.5 StartY=9.01251 StartZ=0 EndX=121.163 EndY=9.0125 EndZ=0
  constraints (46):
    c: Vertical(g0)
    c: Block(g0)
    c: Coincident(g1,g0)
    c: Block(g1)
    c: Coincident(g2,g1)
    c: Block(g2)
    c: Coincident(g3,g2)
    c: Horizontal(g3)
    c: Tangent(g3,g2)
    c: Coincident(g4,g0)
    c: Distance(g4) = 3
    c: Vertical(g4)
    c: Coincident(g5,g4)
    c: Horizontal(g5)
    c: Coincident(g6,g2)
    c: Coincident(g6,g5)
    c: Vertical(g6)
    c: Horizontal(g7)
    c: Distance(g7) = 105
    c: Coincident(g7,g1)
    c: Block(g3)
    c: Weight(g8) = 1
    c: Equal(g8,g9)
    c: Equal(g8,g10)
    c: InternalAlignment(g8,g11)
    c: InternalAlignment(g9,g11)
    c: InternalAlignment(g10,g11)
    c: InternalAlignment(g12,g11)
    c: InternalAlignment(g13,g11)
    c: Block(g11)
    c: Coincident(g14,g11)
    c: Coincident(g14,g3)
    c: Horizontal(g14)
    c: Block(g15)
    c: Coincident(g16,g15)
    c: Block(g16)
    c: Coincident(g17,g11)
    c: Coincident(g17,g16)
    c: Vertical(g17)
    c: Distance(g17) = 14
    c: Coincident(g18,g7)
    c: Coincident(g18,g15)
    c: Vertical(g18)
    c: Distance(g18) = 19
    c: Coincident(g19,g16)
    c: Coincident(g19,g15)
FEATURE [Part::Extrusion] Extrude029
  Base = -> Sketch038
  Dir = (0,0,1)
  DirMode = 2
  FaceMakerClass = Part::FaceMakerBullseye
  LengthFwd = 72
  LengthRev = 0
  Solid = true
  Symmetric = false
FEATURE [Part::Feature] Face085
  shape: bbox 4.8 x 25.5 x 2e-07 mm, 1 faces, 0 solids (baked)
FEATURE [Part::Revolution] Revolve089  label="moreFrontCaseScrewPost003"
  Angle = 360
  Axis = (0,1,0)
  Base = (0,0,0)
  FaceMakerClass = Part::FaceMakerBullseye
  Placement = pos=(109.5,4.5,3.5) rot=(0,0,1;0rad)
  Solid = false
  Source = -> Face085
  Symmetric = false
FEATURE [Part::Feature] Face086
  shape: bbox 4.8 x 25.5 x 2e-07 mm, 1 faces, 0 solids (baked)
FEATURE [Part::Revolution] Revolve090  label="moreFrontCaseScrewPost004"
  Angle = 360
  Axis = (0,1,0)
  Base = (0,0,0)
  FaceMakerClass = Part::FaceMakerBullseye
  Placement = pos=(109.5,4.5,68.5) rot=(0,0,1;0rad)
  Solid = false
  Source = -> Face086
  Symmetric = false
FEATURE [Part::Fillet] Fillet026  label="top013"
  Base = -> Extrude029
  Edges = 1 edges r=2: [Edge35]
FEATURE [Sketcher::SketchObject] Sketch039
  FullyConstrained = true
  sketch-geometry (7):
    g0: LineSegment StartX=0 StartY=0 StartZ=0 EndX=0 EndY=6 EndZ=0
    g1: Circle CenterX=0 CenterY=0 CenterZ=0 NormalX=0 NormalY=0 NormalZ=1 AngleXU=0 Radius=1
    g2: Circle CenterX=8 CenterY=6 CenterZ=0 NormalX=0 NormalY=0 NormalZ=1 AngleXU=0 Radius=1
    g3: BSplineCurve PolesCount=3 KnotsCount=2 Degree=2 IsPeriodic=0
    g4: GeomPoint X=0 Y=0 Z=0
    g5: GeomPoint X=8 Y=6 Z=0
    g6: LineSegment StartX=0 StartY=6 StartZ=0 EndX=8 EndY=6 EndZ=0
  constraints (14):
    c: Coincident(g0,g-1)
    c: Distance(g0) = 6
    c: Vertical(g0)
    c: Coincident(g3,g0)
    c: Weight(g1) = 1
    c: Equal(g1,g2)
    c: InternalAlignment(g1,g3)
    c: InternalAlignment(g2,g3)
    c: InternalAlignment(g4,g3)
    c: InternalAlignment(g5,g3)
    c: Block(g3)
    c: Coincident(g6,g0)
    c: Coincident(g6,g3)
    c: Horizontal(g6)
FEATURE [Sketcher::SketchObject] Sketch040
  FullyConstrained = true
  sketch-geometry (7):
    g0: LineSegment StartX=0 StartY=0 StartZ=0 EndX=0 EndY=6 EndZ=0
    g1: Circle CenterX=0 CenterY=0 CenterZ=0 NormalX=0 NormalY=0 NormalZ=1 AngleXU=0 Radius=1
    g2: Circle CenterX=8 CenterY=6 CenterZ=0 NormalX=0 NormalY=0 NormalZ=1 AngleXU=0 Radius=1
    g3: BSplineCurve PolesCount=3 KnotsCount=2 Degree=2 IsPeriodic=0
    g4: GeomPoint X=0 Y=0 Z=0
    g5: GeomPoint X=8 Y=6 Z=0
    g6: LineSegment StartX=0 StartY=6 StartZ=0 EndX=8 EndY=6 EndZ=0
  constraints (14):
    c: Coincident(g0,g-1)
    c: Distance(g0) = 6
    c: Vertical(g0)
    c: Coincident(g3,g0)
    c: Weight(g1) = 1
    c: Equal(g1,g2)
    c: InternalAlignment(g1,g3)
    c: InternalAlignment(g2,g3)
    c: InternalAlignment(g4,g3)
    c: InternalAlignment(g5,g3)
    c: Block(g3)
    c: Coincident(g6,g0)
    c: Coincident(g6,g3)
    c: Horizontal(g6)
FEATURE [Sketcher::SketchObject] Sketch041
  FullyConstrained = true
  sketch-geometry (7):
    g0: LineSegment StartX=0 StartY=0 StartZ=0 EndX=0 EndY=6 EndZ=0
    g1: Circle CenterX=0 CenterY=0 CenterZ=0 NormalX=0 NormalY=0 NormalZ=1 AngleXU=0 Radius=1
    g2: Circle CenterX=8 CenterY=6 CenterZ=0 NormalX=0 NormalY=0 NormalZ=1 AngleXU=0 Radius=1
    g3: BSplineCurve PolesCount=3 KnotsCount=2 Degree=2 IsPeriodic=0
    g4: GeomPoint X=0 Y=0 Z=0
    g5: GeomPoint X=8 Y=6 Z=0
    g6: LineSegment StartX=0 StartY=6 StartZ=0 EndX=8 EndY=6 EndZ=0
  constraints (14):
    c: Coincident(g0,g-1)
    c: Distance(g0) = 6
    c: Vertical(g0)
    c: Coincident(g3,g0)
    c: Weight(g1) = 1
    c: Equal(g1,g2)
    c: InternalAlignment(g1,g3)
    c: InternalAlignment(g2,g3)
    c: InternalAlignment(g4,g3)
    c: InternalAlignment(g5,g3)
    c: Block(g3)
    c: Coincident(g6,g0)
    c: Coincident(g6,g3)
    c: Horizontal(g6)
FEATURE [Sketcher::SketchObject] Sketch042
  FullyConstrained = true
  sketch-geometry (7):
    g0: LineSegment StartX=0 StartY=0 StartZ=0 EndX=0 EndY=6 EndZ=0
    g1: Circle CenterX=0 CenterY=0 CenterZ=0 NormalX=0 NormalY=0 NormalZ=1 AngleXU=0 Radius=1
    g2: Circle CenterX=8 CenterY=6 CenterZ=0 NormalX=0 NormalY=0 NormalZ=1 AngleXU=0 Radius=1
    g3: BSplineCurve PolesCount=3 KnotsCount=2 Degree=2 IsPeriodic=0
    g4: GeomPoint X=0 Y=0 Z=0
    g5: GeomPoint X=8 Y=6 Z=0
    g6: LineSegment StartX=0 StartY=6 StartZ=0 EndX=8 EndY=6 EndZ=0
  constraints (14):
    c: Coincident(g0,g-1)
    c: Distance(g0) = 6
    c: Vertical(g0)
    c: Coincident(g3,g0)
    c: Weight(g1) = 1
    c: Equal(g1,g2)
    c: InternalAlignment(g1,g3)
    c: InternalAlignment(g2,g3)
    c: InternalAlignment(g4,g3)
    c: InternalAlignment(g5,g3)
    c: Block(g3)
    c: Coincident(g6,g0)
    c: Coincident(g6,g3)
    c: Horizontal(g6)
FEATURE [Part::Extrusion] Extrude030  label="caseScrewPillarBracket008"
  Base = -> Sketch039
  Dir = (0,0,1)
  DirMode = 2
  FaceMakerClass = Part::FaceMakerBullseye
  LengthFwd = 2.4
  LengthRev = 0
  Placement = pos=(15.76,29,8.8) rot=(0,1,0;0rad)
  Solid = true
  Symmetric = false
FEATURE [Part::Extrusion] Extrude031  label="caseScrewPillarBracket009"
  Base = -> Sketch040
  Dir = (0,0,1)
  DirMode = 2
  FaceMakerClass = Part::FaceMakerBullseye
  LengthFwd = 2.4
  LengthRev = 0
  Placement = pos=(15.76,29,60.8) rot=(0,0,1;0rad)
  Solid = true
  Symmetric = false
FEATURE [Part::Extrusion] Extrude032  label="caseScrewPillarBracket010"
  Base = -> Sketch041
  Dir = (0,0,1)
  DirMode = 2
  FaceMakerClass = Part::FaceMakerBullseye
  LengthFwd = 2.4
  LengthRev = 0
  Placement = pos=(13.7,29,13.26) rot=(0,-1,0;1.5708rad)
  Solid = true
  Symmetric = false
FEATURE [Part::Extrusion] Extrude033  label="caseScrewPillarBracket011"
  Base = -> Sketch042
  Dir = (0,0,1)
  DirMode = 2
  FaceMakerClass = Part::FaceMakerBullseye
  LengthFwd = 2.4
  LengthRev = 0
  Placement = pos=(11.3,29,58.74) rot=(0,1,0;1.5708rad)
  Solid = true
  Symmetric = false
FEATURE [Sketcher::SketchObject] Sketch043
  FullyConstrained = true
  sketch-geometry (7):
    g0: LineSegment StartX=0 StartY=0 StartZ=0 EndX=0 EndY=6 EndZ=0
    g1: Circle CenterX=0 CenterY=0 CenterZ=0 NormalX=0 NormalY=0 NormalZ=1 AngleXU=0 Radius=1
    g2: Circle CenterX=8 CenterY=6 CenterZ=0 NormalX=0 NormalY=0 NormalZ=1 AngleXU=0 Radius=1
    g3: BSplineCurve PolesCount=3 KnotsCount=2 Degree=2 IsPeriodic=0
    g4: GeomPoint X=0 Y=0 Z=0
    g5: GeomPoint X=8 Y=6 Z=0
    g6: LineSegment StartX=0 StartY=6 StartZ=0 EndX=8 EndY=6 EndZ=0
  constraints (14):
    c: Coincident(g0,g-1)
    c: Distance(g0) = 6
    c: Vertical(g0)
    c: Coincident(g3,g0)
    c: Weight(g1) = 1
    c: Equal(g1,g2)
    c: InternalAlignment(g1,g3)
    c: InternalAlignment(g2,g3)
    c: InternalAlignment(g4,g3)
    c: InternalAlignment(g5,g3)
    c: Block(g3)
    c: Coincident(g6,g0)
    c: Coincident(g6,g3)
    c: Horizontal(g6)
FEATURE [Part::Extrusion] Extrude034  label="caseScrewPillarBracket012"
  Base = -> Sketch043
  Dir = (0,0,1)
  DirMode = 2
  FaceMakerClass = Part::FaceMakerBullseye
  LengthFwd = 2.4
  LengthRev = 0
  Placement = pos=(88.3,29,65.23) rot=(0,1,0;1.5708rad)
  Solid = true
  Symmetric = false
FEATURE [Sketcher::SketchObject] Sketch044
  FullyConstrained = true
  sketch-geometry (7):
    g0: LineSegment StartX=0 StartY=0 StartZ=0 EndX=0 EndY=6 EndZ=0
    g1: Circle CenterX=0 CenterY=0 CenterZ=0 NormalX=0 NormalY=0 NormalZ=1 AngleXU=0 Radius=1
    g2: Circle CenterX=8 CenterY=6 CenterZ=0 NormalX=0 NormalY=0 NormalZ=1 AngleXU=0 Radius=1
    g3: BSplineCurve PolesCount=3 KnotsCount=2 Degree=2 IsPeriodic=0
    g4: GeomPoint X=0 Y=0 Z=0
    g5: GeomPoint X=8 Y=6 Z=0
    g6: LineSegment StartX=0 StartY=6 StartZ=0 EndX=8 EndY=6 EndZ=0
  constraints (14):
    c: Coincident(g0,g-1)
    c: Distance(g0) = 6
    c: Vertical(g0)
    c: Coincident(g3,g0)
    c: Weight(g1) = 1
    c: Equal(g1,g2)
    c: InternalAlignment(g1,g3)
    c: InternalAlignment(g2,g3)
    c: InternalAlignment(g4,g3)
    c: InternalAlignment(g5,g3)
    c: Block(g3)
    c: Coincident(g6,g0)
    c: Coincident(g6,g3)
    c: Horizontal(g6)
FEATURE [Part::Extrusion] Extrude035  label="caseScrewPillarBracket013"
  Base = -> Sketch044
  Dir = (0,0,1)
  DirMode = 2
  FaceMakerClass = Part::FaceMakerBullseye
  LengthFwd = 2.4
  LengthRev = 0
  Placement = pos=(90.7,29,6.77) rot=(0,-1,0;1.5708rad)
  Solid = true
  Symmetric = false
FEATURE [Sketcher::SketchObject] Sketch045
  FullyConstrained = true
  sketch-geometry (7):
    g0: LineSegment StartX=0 StartY=0 StartZ=0 EndX=0 EndY=6 EndZ=0
    g1: Circle CenterX=0 CenterY=0 CenterZ=0 NormalX=0 NormalY=0 NormalZ=1 AngleXU=0 Radius=1
    g2: Circle CenterX=8 CenterY=6 CenterZ=0 NormalX=0 NormalY=0 NormalZ=1 AngleXU=0 Radius=1
    g3: BSplineCurve PolesCount=3 KnotsCount=2 Degree=2 IsPeriodic=0
    g4: GeomPoint X=0 Y=0 Z=0
    g5: GeomPoint X=8 Y=6 Z=0
    g6: LineSegment StartX=0 StartY=6 StartZ=0 EndX=8 EndY=6 EndZ=0
  constraints (14):
    c: Coincident(g0,g-1)
    c: Distance(g0) = 6
    c: Vertical(g0)
    c: Coincident(g3,g0)
    c: Weight(g1) = 1
    c: Equal(g1,g2)
    c: InternalAlignment(g1,g3)
    c: InternalAlignment(g2,g3)
    c: InternalAlignment(g4,g3)
    c: InternalAlignment(g5,g3)
    c: Block(g3)
    c: Coincident(g6,g0)
    c: Coincident(g6,g3)
    c: Horizontal(g6)
FEATURE [Sketcher::SketchObject] Sketch046
  FullyConstrained = true
  sketch-geometry (7):
    g0: LineSegment StartX=0 StartY=0 StartZ=0 EndX=0 EndY=6 EndZ=0
    g1: Circle CenterX=0 CenterY=0 CenterZ=0 NormalX=0 NormalY=0 NormalZ=1 AngleXU=0 Radius=1
    g2: Circle CenterX=8 CenterY=6 CenterZ=0 NormalX=0 NormalY=0 NormalZ=1 AngleXU=0 Radius=1
    g3: BSplineCurve PolesCount=3 KnotsCount=2 Degree=2 IsPeriodic=0
    g4: GeomPoint X=0 Y=0 Z=0
    g5: GeomPoint X=8 Y=6 Z=0
    g6: LineSegment StartX=0 StartY=6 StartZ=0 EndX=8 EndY=6 EndZ=0
  constraints (14):
    c: Coincident(g0,g-1)
    c: Distance(g0) = 6
    c: Vertical(g0)
    c: Coincident(g3,g0)
    c: Weight(g1) = 1
    c: Equal(g1,g2)
    c: InternalAlignment(g1,g3)
    c: InternalAlignment(g2,g3)
    c: InternalAlignment(g4,g3)
    c: InternalAlignment(g5,g3)
    c: Block(g3)
    c: Coincident(g6,g0)
    c: Coincident(g6,g3)
    c: Horizontal(g6)
FEATURE [Part::Extrusion] Extrude036  label="caseScrewPillarBracket014"
  Base = -> Sketch045
  Dir = (0,0,1)
  DirMode = 2
  FaceMakerClass = Part::FaceMakerBullseye
  LengthFwd = 2.4
  LengthRev = 0
  Placement = pos=(110.7,29,6.77) rot=(0,-1,0;1.5708rad)
  Solid = true
  Symmetric = false
FEATURE [Part::Extrusion] Extrude037  label="caseScrewPillarBracket015"
  Base = -> Sketch046
  Dir = (0,0,1)
  DirMode = 2
  FaceMakerClass = Part::FaceMakerBullseye
  LengthFwd = 2.4
  LengthRev = 0
  Placement = pos=(108.3,29,65.23) rot=(0,1,0;1.5708rad)
  Solid = true
  Symmetric = false
FEATURE [Part::Box] Box013  label="frontCaseScrewPillarBracket002"
  AttacherType = Attacher::AttachEngine3D
  Height = 2.4
  Length = 22
  Placement = pos=(87,28,2.3) rot=(0,0,1;0rad)
  Width = 7
FEATURE [Part::Box] Box014  label="frontCaseScrewPillarBracket003"
  AttacherType = Attacher::AttachEngine3D
  Height = 2.4
  Length = 22
  Placement = pos=(87,28,67.3) rot=(0,0,1;0rad)
  Width = 7
FEATURE [Part::Feature] Face087
  shape: bbox 4.8 x 30.2 x 2e-07 mm, 1 faces, 0 solids (baked)
FEATURE [Part::Revolution] Revolve091  label="frontCaseScrewPost004"
  Angle = 360
  Axis = (0,1,0)
  Base = (0,0,0)
  FaceMakerClass = Part::FaceMakerBullseye
  Placement = pos=(89.5,4.5,3.5) rot=(0,0,1;0rad)
  Solid = false
  Source = -> Face087
  Symmetric = false
FEATURE [Part::Feature] Face088
  shape: bbox 4.8 x 30.2 x 2e-07 mm, 1 faces, 0 solids (baked)
FEATURE [Part::Revolution] Revolve092  label="frontCaseScrewPost005"
  Angle = 360
  Axis = (0,1,0)
  Base = (0,0,0)
  FaceMakerClass = Part::FaceMakerBullseye
  Placement = pos=(89.5,4.5,68.5) rot=(0,0,1;0rad)
  Solid = false
  Source = -> Face088
  Symmetric = false
FEATURE [Part::Feature] Face089
  shape: bbox 3.5 x 30.2 x 2e-07 mm, 1 faces, 0 solids (baked)
FEATURE [Part::Revolution] Revolve093  label="backCaseScrewPost002"
  Angle = 360
  Axis = (0,1,0)
  Base = (0,0,0)
  FaceMakerClass = Part::FaceMakerBullseye
  Placement = pos=(12.5,4.5,10) rot=(0,0,1;0rad)
  Solid = false
  Source = -> Face089
  Symmetric = false
FEATURE [Part::Feature] Face090
  shape: bbox 3.5 x 30.2 x 2e-07 mm, 1 faces, 0 solids (baked)
FEATURE [Part::Revolution] Revolve094  label="backCaseScrewPost003"
  Angle = 360
  Axis = (0,1,0)
  Base = (0,0,0)
  FaceMakerClass = Part::FaceMakerBullseye
  Placement = pos=(12.5,4.5,62) rot=(0,0,1;0rad)
  Solid = false
  Source = -> Face090
  Symmetric = false
FEATURE [Part::Box] Box015  label="Cube011"
  AttacherType = Attacher::AttachEngine3D
  Height = 28.8
  Length = 3
  Placement = pos=(107.3,28,21.6) rot=(0,0,1;0rad)
  Width = 7
FEATURE [Part::Box] Box016  label="Cube012"
  AttacherType = Attacher::AttachEngine3D
  Height = 3
  Length = 7.4
  Placement = pos=(107.3,28,18.6) rot=(0,0,1;0rad)
  Width = 7
FEATURE [Part::Box] Box017  label="Cube013"
  AttacherType = Attacher::AttachEngine3D
  Height = 3
  Length = 7.4
  Placement = pos=(107.3,28,50.4) rot=(0,0,1;0rad)
  Width = 7
FEATURE [Part::Cylinder] Cylinder024
  Angle = 360
  AttacherType = Attacher::AttachEngine3D
  Height = 20
  Placement = pos=(0,0,36.15) rot=(0,0,1;0rad)
  Radius = 14.3
FEATURE [Part::Cylinder] Cylinder025
  Angle = 360
  AttacherType = Attacher::AttachEngine3D
  Height = 10
  Placement = pos=(0,0,36.15) rot=(0,0,1;0rad)
  Radius = 4
FEATURE [Part::MultiFuse] Fusion066  label="removeToCreteHoleForPlugHousing009"
  Placement = pos=(70,19,36) rot=(0,1,0;1.5708rad)
  Shapes = -> [Cylinder024,Cylinder025]
FEATURE [Part::MultiFuse] Fusion065  label="plugHousingBracketHolder002"
  Shapes = -> [Box017,Box015,Box016]
FEATURE [Part::Cut] Cut025  label="plugHousingBracketHolder003"
  Base = -> Fusion065
  Placement = pos=(7,0,0) rot=(0,0,1;0rad)
  Tool = -> Fusion066
FEATURE [Sketcher::SketchObject] Sketch047
  FullyConstrained = false
  Placement = pos=(0,0,0) rot=(1,0,0;1.5708rad)
  sketch-geometry (24):
    g0: ArcOfCircle CenterX=-4 CenterY=-10.5 CenterZ=0 NormalX=0 NormalY=0 NormalZ=1 AngleXU=0 Radius=1.5 StartAngle=6e-16 EndAngle=3.14159
    g1: ArcOfCircle CenterX=-34.2 CenterY=-10.5 CenterZ=0 NormalX=0 NormalY=0 NormalZ=1 AngleXU=0 Radius=1.5 StartAngle=0 EndAngle=3.14159
    g2: ArcOfCircle CenterX=-34.2 CenterY=-27.7 CenterZ=0 NormalX=0 NormalY=0 NormalZ=1 AngleXU=0 Radius=1.5 StartAngle=3.14159 EndAngle=6.28319
    g3: ArcOfCircle CenterX=-4 CenterY=-27.7 CenterZ=0 NormalX=0 NormalY=0 NormalZ=1 AngleXU=0 Radius=1.5 StartAngle=3.1416 EndAngle=6.28319
    g4: ArcOfCircle CenterX=-10 CenterY=-4.3 CenterZ=0 NormalX=0 NormalY=0 NormalZ=1 AngleXU=0 Radius=1.5 StartAngle=2e-16 EndAngle=3.14159
    g5: ArcOfCircle CenterX=-16.1 CenterY=-1.8 CenterZ=0 NormalX=0 NormalY=0 NormalZ=1 AngleXU=0 Radius=1.5 StartAngle=5e-16 EndAngle=3.14159
    g6: ArcOfCircle CenterX=-22.1 CenterY=-1.8 CenterZ=0 NormalX=0 NormalY=0 NormalZ=1 AngleXU=0 Radius=1.5 StartAngle=5e-16 EndAngle=3.14159
    g7: ArcOfCircle CenterX=-28.2 CenterY=-4.3 CenterZ=0 NormalX=0 NormalY=0 NormalZ=1 AngleXU=0 Radius=1.5 StartAngle=2e-16 EndAngle=3.14159
    g8: ArcOfCircle CenterX=-10 CenterY=-33.9 CenterZ=0 NormalX=0 NormalY=0 NormalZ=1 AngleXU=0 Radius=1.5 StartAngle=3.14159 EndAngle=6.28319
    g9: ArcOfCircle CenterX=-16.1 CenterY=-36.4 CenterZ=0 NormalX=0 NormalY=0 NormalZ=1 AngleXU=0 Radius=1.5 StartAngle=3.14159 EndAngle=6.28319
    g10: ArcOfCircle CenterX=-22.1 CenterY=-36.4 CenterZ=0 NormalX=0 NormalY=0 NormalZ=1 AngleXU=0 Radius=1.5 StartAngle=3.14159 EndAngle=6.28319
    g11: ArcOfCircle CenterX=-28.2 CenterY=-33.9 CenterZ=0 NormalX=0 NormalY=0 NormalZ=1 AngleXU=0 Radius=1.5 StartAngle=3.14159 EndAngle=6.28319
    g12: LineSegment StartX=-35.7 StartY=-10.5 StartZ=0 EndX=-35.7 EndY=-27.7 EndZ=0
    g13: LineSegment StartX=-32.7 StartY=-10.5 StartZ=0 EndX=-32.7 EndY=-27.7 EndZ=0
    g14: LineSegment StartX=-29.7 StartY=-33.9 StartZ=0 EndX=-29.7 EndY=-4.3 EndZ=0
    g15: LineSegment StartX=-26.7 StartY=-33.9 StartZ=0 EndX=-26.7 EndY=-4.3 EndZ=0
    g16: LineSegment StartX=-2.5 StartY=-10.5 StartZ=0 EndX=-2.5 EndY=-27.7 EndZ=0
    g17: LineSegment StartX=-8.5 StartY=-4.3 StartZ=0 EndX=-8.5 EndY=-33.9 EndZ=0
    g18: LineSegment StartX=-5.5 StartY=-10.5 StartZ=0 EndX=-5.5 EndY=-27.7 EndZ=0
    g19: LineSegment StartX=-11.5 StartY=-4.3 StartZ=0 EndX=-11.5 EndY=-33.9 EndZ=0
    g20: LineSegment StartX=-14.6 StartY=-1.8 StartZ=0 EndX=-14.6 EndY=-36.4 EndZ=0
    g21: LineSegment StartX=-17.6 StartY=-1.8 StartZ=0 EndX=-17.6 EndY=-36.4 EndZ=0
    g22: LineSegment StartX=-20.6 StartY=-36.4 StartZ=0 EndX=-20.6 EndY=-1.8 EndZ=0
    g23: LineSegment StartX=-23.6 StartY=-1.8 StartZ=0 EndX=-23.6 EndY=-36.4 EndZ=0
  constraints (48):
    c: Block(g0)
    c: Block(g1)
    c: Block(g2)
    c: Block(g3)
    c: Block(g4)
    c: Block(g5)
    c: Block(g6)
    c: Block(g7)
    c: Block(g8)
    c: Block(g9)
    c: Block(g10)
    c: Block(g11)
    c: Coincident(g12,g1)
    c: Coincident(g12,g2)
    c: Vertical(g12)
    c: Coincident(g13,g1)
    c: Coincident(g13,g2)
    c: Vertical(g13)
    c: Coincident(g14,g11)
    c: Coincident(g14,g7)
    c: Vertical(g14)
    c: Coincident(g15,g11)
    c: Coincident(g15,g7)
    c: Vertical(g15)
    c: Coincident(g16,g0)
    c: Coincident(g16,g3)
    c: Vertical(g16)
    c: Coincident(g17,g4)
    c: Coincident(g17,g8)
    c: Vertical(g17)
    c: Coincident(g18,g0)
    c: Coincident(g18,g3)
    c: Vertical(g18)
    c: Coincident(g19,g4)
    c: Coincident(g19,g8)
    c: Vertical(g19)
    c: Coincident(g20,g5)
    c: Coincident(g20,g9)
    c: Vertical(g20)
    c: Coincident(g21,g5)
    c: Coincident(g21,g9)
    c: Vertical(g21)
    c: Coincident(g22,g10)
    c: Coincident(g22,g6)
    c: Vertical(g22)
    c: Coincident(g23,g6)
    c: Coincident(g23,g10)
    c: Vertical(g23)
FEATURE [Part::Extrusion] Extrude038  label="removeToCreateFanGrillHoles001"
  Base = -> Sketch047
  Dir = (0,-1,6e-16)
  DirMode = 2
  FaceMakerClass = Part::FaceMakerBullseye
  LengthFwd = 10
  LengthRev = 0
  Placement = pos=(65.4,44,54.82) rot=(0,0,1;0rad)
  Solid = true
  Symmetric = false
FEATURE [Part::Feature] Wire004
  shape: bbox 11 x 5.2 x 2e-07 mm, 0 faces, 0 solids (baked)
FEATURE [Part::Revolution] Revolve095
  Angle = 360
  Axis = (0,1,0)
  Base = (0,0,0)
  FaceMakerClass = Part::FaceMakerBullseye
  Placement = pos=(30.3,38,19.7) rot=(0,0,1;0rad)
  Solid = true
  Source = -> Wire004
  Symmetric = false
FEATURE [Part::Feature] Wire005
  shape: bbox 11 x 5.2 x 2e-07 mm, 0 faces, 0 solids (baked)
FEATURE [Part::Revolution] Revolve096
  Angle = 360
  Axis = (0,1,0)
  Base = (0,0,0)
  FaceMakerClass = Part::FaceMakerBullseye
  Placement = pos=(30.3,38,51.7) rot=(0,0,1;0rad)
  Solid = true
  Source = -> Wire005
  Symmetric = false
FEATURE [Part::Feature] Wire006
  shape: bbox 11 x 5.2 x 2e-07 mm, 0 faces, 0 solids (baked)
FEATURE [Part::Revolution] Revolve097
  Angle = 360
  Axis = (0,1,0)
  Base = (0,0,0)
  FaceMakerClass = Part::FaceMakerBullseye
  Placement = pos=(62.3,38,51.7) rot=(0,0,1;0rad)
  Solid = true
  Source = -> Wire006
  Symmetric = false
FEATURE [Part::Feature] Wire007
  shape: bbox 11 x 5.2 x 2e-07 mm, 0 faces, 0 solids (baked)
FEATURE [Part::Revolution] Revolve098
  Angle = 360
  Axis = (0,1,0)
  Base = (0,0,0)
  FaceMakerClass = Part::FaceMakerBullseye
  Placement = pos=(62.3,38,19.7) rot=(0,0,1;0rad)
  Solid = true
  Source = -> Wire007
  Symmetric = false
FEATURE [Part::MultiFuse] Fusion067  label="fanScrewHousing002"
  Shapes = -> [Revolve098,Revolve097,Revolve096,Revolve095]
FEATURE [Part::Feature] Face091 .. Face094  x4 (patterned run collapsed; names and placements below)
  shape: bbox 3.5 x 17.8 x 2e-07 mm, 1 faces, 0 solids (baked)
FEATURE [Part::Revolution] Revolve099  label="removeToCreateScrewAndThreadedInsertHole026"
  Angle = 360
  Axis = (0,1,0)
  Base = (0,0,0)
  FaceMakerClass = Part::FaceMakerBullseye
  Placement = pos=(62.3,30.3,19.7) rot=(0,0,1;0rad)
  Solid = false
  Source = -> Face091
  Symmetric = false
FEATURE [Part::Revolution] Revolve100  label="removeToCreateScrewAndThreadedInsertHole027"
  Angle = 360
  Axis = (0,1,0)
  Base = (0,0,0)
  FaceMakerClass = Part::FaceMakerBullseye
  Placement = pos=(62.3,30.3,51.7) rot=(0,0,1;0rad)
  Solid = false
  Source = -> Face092
  Symmetric = false
FEATURE [Part::Revolution] Revolve101  label="removeToCreateScrewAndThreadedInsertHole028"
  Angle = 360
  Axis = (0,1,0)
  Base = (0,0,0)
  FaceMakerClass = Part::FaceMakerBullseye
  Placement = pos=(30.3,30.3,19.7) rot=(0,0,1;0rad)
  Solid = false
  Source = -> Face093
  Symmetric = false
FEATURE [Part::Revolution] Revolve102  label="removeToCreateScrewAndThreadedInsertHole029"
  Angle = 360
  Axis = (0,1,0)
  Base = (0,0,0)
  FaceMakerClass = Part::FaceMakerBullseye
  Placement = pos=(30.3,30.3,51.7) rot=(0,0,1;0rad)
  Solid = false
  Source = -> Face094
  Symmetric = false
FEATURE [Part::MultiFuse] Fusion068  label="createThreadedInsertHolesForFan002"
  Shapes = -> [Revolve099,Revolve100,Revolve101,Revolve102]
FEATURE [Part::Cut] Cut026  label="fanScrewHousing003"
  Base = -> Fusion067
  Tool = -> Fusion068
FEATURE [Sketcher::SketchObject] Sketch048
  FullyConstrained = false
  Placement = pos=(0,0,0) rot=(1,0,0;1.5708rad)
  sketch-geometry (24):
    g0: ArcOfCircle CenterX=-4 CenterY=-10.5 CenterZ=0 NormalX=0 NormalY=0 NormalZ=1 AngleXU=0 Radius=1.5 StartAngle=6e-16 EndAngle=3.14159
    g1: ArcOfCircle CenterX=-34.2 CenterY=-10.5 CenterZ=0 NormalX=0 NormalY=0 NormalZ=1 AngleXU=0 Radius=1.5 StartAngle=0 EndAngle=3.14159
    g2: ArcOfCircle CenterX=-34.2 CenterY=-27.7 CenterZ=0 NormalX=0 NormalY=0 NormalZ=1 AngleXU=0 Radius=1.5 StartAngle=3.14159 EndAngle=6.28319
    g3: ArcOfCircle CenterX=-4 CenterY=-27.7 CenterZ=0 NormalX=0 NormalY=0 NormalZ=1 AngleXU=0 Radius=1.5 StartAngle=3.1416 EndAngle=6.28319
    g4: ArcOfCircle CenterX=-10 CenterY=-4.3 CenterZ=0 NormalX=0 NormalY=0 NormalZ=1 AngleXU=0 Radius=1.5 StartAngle=2e-16 EndAngle=3.14159
    g5: ArcOfCircle CenterX=-16.1 CenterY=-1.8 CenterZ=0 NormalX=0 NormalY=0 NormalZ=1 AngleXU=0 Radius=1.5 StartAngle=5e-16 EndAngle=3.14159
    g6: ArcOfCircle CenterX=-22.1 CenterY=-1.8 CenterZ=0 NormalX=0 NormalY=0 NormalZ=1 AngleXU=0 Radius=1.5 StartAngle=5e-16 EndAngle=3.14159
    g7: ArcOfCircle CenterX=-28.2 CenterY=-4.3 CenterZ=0 NormalX=0 NormalY=0 NormalZ=1 AngleXU=0 Radius=1.5 StartAngle=2e-16 EndAngle=3.14159
    g8: ArcOfCircle CenterX=-10 CenterY=-33.9 CenterZ=0 NormalX=0 NormalY=0 NormalZ=1 AngleXU=0 Radius=1.5 StartAngle=3.14159 EndAngle=6.28319
    g9: ArcOfCircle CenterX=-16.1 CenterY=-36.4 CenterZ=0 NormalX=0 NormalY=0 NormalZ=1 AngleXU=0 Radius=1.5 StartAngle=3.14159 EndAngle=6.28319
    g10: ArcOfCircle CenterX=-22.1 CenterY=-36.4 CenterZ=0 NormalX=0 NormalY=0 NormalZ=1 AngleXU=0 Radius=1.5 StartAngle=3.14159 EndAngle=6.28319
    g11: ArcOfCircle CenterX=-28.2 CenterY=-33.9 CenterZ=0 NormalX=0 NormalY=0 NormalZ=1 AngleXU=0 Radius=1.5 StartAngle=3.14159 EndAngle=6.28319
    g12: LineSegment StartX=-35.7 StartY=-10.5 StartZ=0 EndX=-35.7 EndY=-27.7 EndZ=0
    g13: LineSegment StartX=-32.7 StartY=-10.5 StartZ=0 EndX=-32.7 EndY=-27.7 EndZ=0
    g14: LineSegment StartX=-29.7 StartY=-33.9 StartZ=0 EndX=-29.7 EndY=-4.3 EndZ=0
    g15: LineSegment StartX=-26.7 StartY=-33.9 StartZ=0 EndX=-26.7 EndY=-4.3 EndZ=0
    g16: LineSegment StartX=-2.5 StartY=-10.5 StartZ=0 EndX=-2.5 EndY=-27.7 EndZ=0
    g17: LineSegment StartX=-8.5 StartY=-4.3 StartZ=0 EndX=-8.5 EndY=-33.9 EndZ=0
    g18: LineSegment StartX=-5.5 StartY=-10.5 StartZ=0 EndX=-5.5 EndY=-27.7 EndZ=0
    g19: LineSegment StartX=-11.5 StartY=-4.3 StartZ=0 EndX=-11.5 EndY=-33.9 EndZ=0
    g20: LineSegment StartX=-14.6 StartY=-1.8 StartZ=0 EndX=-14.6 EndY=-36.4 EndZ=0
    g21: LineSegment StartX=-17.6 StartY=-1.8 StartZ=0 EndX=-17.6 EndY=-36.4 EndZ=0
    g22: LineSegment StartX=-20.6 StartY=-36.4 StartZ=0 EndX=-20.6 EndY=-1.8 EndZ=0
    g23: LineSegment StartX=-23.6 StartY=-1.8 StartZ=0 EndX=-23.6 EndY=-36.4 EndZ=0
  constraints (48):
    c: Block(g0)
    c: Block(g1)
    c: Block(g2)
    c: Block(g3)
    c: Block(g4)
    c: Block(g5)
    c: Block(g6)
    c: Block(g7)
    c: Block(g8)
    c: Block(g9)
    c: Block(g10)
    c: Block(g11)
    c: Coincident(g12,g1)
    c: Coincident(g12,g2)
    c: Vertical(g12)
    c: Coincident(g13,g1)
    c: Coincident(g13,g2)
    c: Vertical(g13)
    c: Coincident(g14,g11)
    c: Coincident(g14,g7)
    c: Vertical(g14)
    c: Coincident(g15,g11)
    c: Coincident(g15,g7)
    c: Vertical(g15)
    c: Coincident(g16,g0)
    c: Coincident(g16,g3)
    c: Vertical(g16)
    c: Coincident(g17,g4)
    c: Coincident(g17,g8)
    c: Vertical(g17)
    c: Coincident(g18,g0)
    c: Coincident(g18,g3)
    c: Vertical(g18)
    c: Coincident(g19,g4)
    c: Coincident(g19,g8)
    c: Vertical(g19)
    c: Coincident(g20,g5)
    c: Coincident(g20,g9)
    c: Vertical(g20)
    c: Coincident(g21,g5)
    c: Coincident(g21,g9)
    c: Vertical(g21)
    c: Coincident(g22,g10)
    c: Coincident(g22,g6)
    c: Vertical(g22)
    c: Coincident(g23,g6)
    c: Coincident(g23,g10)
    c: Vertical(g23)
FEATURE [Part::Extrusion] Extrude039  label="removeToCreateFanGrillHoles002"
  Base = -> Sketch048
  Dir = (0,-1,6e-16)
  DirMode = 2
  FaceMakerClass = Part::FaceMakerBullseye
  LengthFwd = 10
  LengthRev = 0
  Placement = pos=(65.4,44,54.82) rot=(0,0,1;0rad)
  Solid = true
  Symmetric = false
FEATURE [Part::Cut] Cut027  label="fanScrewHousing004"
  Base = -> Cut026
  Tool = -> Extrude038
FEATURE [Part::Cut] Cut028  label="top014"
  Base = -> Fillet026
  Tool = -> Extrude039
FEATURE [Part::Feature] Face095 .. Face098  x4 (patterned run collapsed; names and placements below)
  shape: bbox 3.5 x 17.8 x 2e-07 mm, 1 faces, 0 solids (baked)
FEATURE [Part::Revolution] Revolve103  label="removeToCreateScrewAndThreadedInsertHole030"
  Angle = 360
  Axis = (0,1,0)
  Base = (0,0,0)
  FaceMakerClass = Part::FaceMakerBullseye
  Placement = pos=(62.3,30.3,19.7) rot=(0,0,1;0rad)
  Solid = false
  Source = -> Face095
  Symmetric = false
FEATURE [Part::Revolution] Revolve104  label="removeToCreateScrewAndThreadedInsertHole031"
  Angle = 360
  Axis = (0,1,0)
  Base = (0,0,0)
  FaceMakerClass = Part::FaceMakerBullseye
  Placement = pos=(62.3,30.3,51.7) rot=(0,0,1;0rad)
  Solid = false
  Source = -> Face096
  Symmetric = false
FEATURE [Part::Revolution] Revolve105  label="removeToCreateScrewAndThreadedInsertHole032"
  Angle = 360
  Axis = (0,1,0)
  Base = (0,0,0)
  FaceMakerClass = Part::FaceMakerBullseye
  Placement = pos=(30.3,30.3,19.7) rot=(0,0,1;0rad)
  Solid = false
  Source = -> Face097
  Symmetric = false
FEATURE [Part::Revolution] Revolve106  label="removeToCreateScrewAndThreadedInsertHole033"
  Angle = 360
  Axis = (0,1,0)
  Base = (0,0,0)
  FaceMakerClass = Part::FaceMakerBullseye
  Placement = pos=(30.3,30.3,51.7) rot=(0,0,1;0rad)
  Solid = false
  Source = -> Face098
  Symmetric = false
FEATURE [Part::MultiFuse] Fusion069  label="createThreadedInsertHolesForFan003"
  Shapes = -> [Revolve103,Revolve104,Revolve105,Revolve106]
FEATURE [Part::Cut] Cut029  label="top015"
  Base = -> Cut028
  Tool = -> Fusion054
FEATURE [Part::Cut] Cut030  label="fanScrewHousing005"
  Base = -> Cut027
  Tool = -> Fusion069
FEATURE [Part::Cylinder] Cylinder026  label="removeToCreteHoleForPlugHousing010"
  Angle = 360
  AttacherType = Attacher::AttachEngine3D
  Height = 20
  Placement = pos=(-2,19,36) rot=(0,1,0;1.5708rad)
  Radius = 14.3
FEATURE [Part::Box] Box018  label="removeToCreteHoleForPlugHousing011"
  AttacherType = Attacher::AttachEngine3D
  Height = 28.6
  Length = 10
  Placement = pos=(-2,0,21.7) rot=(0,0,1;0rad)
  Width = 19
FEATURE [Part::Box] Box019  label="wireHolderBottomCaseBit"
  AttacherType = Attacher::AttachEngine3D
  Height = 28
  Length = 3
  Placement = pos=(0,0,22) rot=(0,0,1;0rad)
  Width = 21
FEATURE [Part::Cylinder] Cylinder027  label="removeToCreteHoleForPlugHousing012"
  Angle = 360
  AttacherType = Attacher::AttachEngine3D
  Height = 20
  Placement = pos=(-2,19,36) rot=(0,1,0;1.5708rad)
  Radius = 14.3
FEATURE [Part::Cut] Cut031  label="wireHolderBottomCaseBit001"
  Base = -> Box019
  Tool = -> Cylinder027
FEATURE [Part::MultiFuse] Fusion070  label="removeToCreteHoleForPlugHousing013"
  Shapes = -> [Box018,Cylinder026]
FEATURE [Part::Cut] Cut032  label="top016"
  Base = -> Cut029
  Tool = -> Fusion070
FEATURE [Part::Cylinder] Cylinder028
  Angle = 360
  AttacherType = Attacher::AttachEngine3D
  Height = 20
  Placement = pos=(0,0,36.15) rot=(0,0,1;0rad)
  Radius = 14.3
FEATURE [Part::Cylinder] Cylinder029
  Angle = 360
  AttacherType = Attacher::AttachEngine3D
  Height = 10
  Placement = pos=(0,0,36.15) rot=(0,0,1;0rad)
  Radius = 4
FEATURE [Part::MultiFuse] Fusion071  label="removeToCreteHoleForPlugHousing014"
  Placement = pos=(70,19,36) rot=(0,1,0;1.5708rad)
  Shapes = -> [Cylinder028,Cylinder029]
FEATURE [Sketcher::SketchObject] Sketch049  label="topSketch011"
  FullyConstrained = false
  sketch-geometry (4):
    g0: ArcOfCircle CenterX=105 CenterY=19 CenterZ=0 NormalX=0 NormalY=0 NormalZ=1 AngleXU=0 Radius=16 StartAngle=5.54125 EndAngle=6.28319
    g1: ArcOfCircle CenterX=105 CenterY=19 CenterZ=0 NormalX=0 NormalY=0 NormalZ=1 AngleXU=0 Radius=19 StartAngle=5.54125 EndAngle=6.28319
    g2: LineSegment StartX=116.795 StartY=8.18859 StartZ=0 EndX=119.006 EndY=6.16145 EndZ=0
    g3: LineSegment StartX=121 StartY=19 StartZ=0 EndX=124 EndY=19 EndZ=0
  constraints (9):
    c: Block(g0)
    c: Block(g2)
    c: Block(g1)
    c: Coincident(g2,g1)
    c: Coincident(g2,g0)
    c: Coincident(g3,g0)
    c: Coincident(g3,g1)
    c: Horizontal(g3)
    c: Block(g3)
FEATURE [Part::Box] Box020  label="removeToCreteHoleForPlugHousing015"
  AttacherType = Attacher::AttachEngine3D
  Height = 28.6
  Length = 20
  Placement = pos=(106.15,0,21.7) rot=(0,0,1;0rad)
  Width = 19
FEATURE [Part::MultiFuse] Fusion072  label="removeToCreteHoleForPlugHousing016"
  Shapes = -> [Box020,Fusion071]
FEATURE [Part::Cut] Cut033  label="removeToCreteHoleForPlugHousing017"
  Base = -> Cut032
  Tool = -> Fusion072
FEATURE [Part::Cylinder] Cylinder030
  Angle = 360
  AttacherType = Attacher::AttachEngine3D
  Height = 20
  Placement = pos=(0,0,36.15) rot=(0,0,1;0rad)
  Radius = 14.3
FEATURE [Part::Cylinder] Cylinder031
  Angle = 360
  AttacherType = Attacher::AttachEngine3D
  Height = 10
  Placement = pos=(0,0,36.15) rot=(0,0,1;0rad)
  Radius = 4
FEATURE [Part::Box] Box021  label="removeToCreteHoleForPlugHousing019"
  AttacherType = Attacher::AttachEngine3D
  Height = 28.6
  Length = 20
  Placement = pos=(106.15,0,21.7) rot=(0,0,1;0rad)
  Width = 19
FEATURE [Part::MultiFuse] Fusion074  label="removeToCreteHoleForPlugHousing020"
  Placement = pos=(70,19,36) rot=(0,1,0;1.5708rad)
  Shapes = -> [Cylinder030,Cylinder031]
FEATURE [Part::MultiFuse] Fusion073  label="removeToCreteHoleForPlugHousing018"
  Placement = pos=(0,0,28.3) rot=(0,0,1;0rad)
  Shapes = -> [Box021,Fusion074]
FEATURE [Part::Cylinder] Cylinder032
  Angle = 360
  AttacherType = Attacher::AttachEngine3D
  Height = 20
  Placement = pos=(0,0,36.15) rot=(0,0,1;0rad)
  Radius = 14.3
FEATURE [Part::Cylinder] Cylinder033
  Angle = 360
  AttacherType = Attacher::AttachEngine3D
  Height = 10
  Placement = pos=(0,0,36.15) rot=(0,0,1;0rad)
  Radius = 4
FEATURE [Part::Box] Box022  label="removeToCreteHoleForPlugHousing021"
  AttacherType = Attacher::AttachEngine3D
  Height = 28.6
  Length = 20
  Placement = pos=(106.15,0,21.7) rot=(0,0,1;0rad)
  Width = 19
FEATURE [Part::MultiFuse] Fusion076  label="removeToCreteHoleForPlugHousing023"
  Placement = pos=(70,19,36) rot=(0,1,0;1.5708rad)
  Shapes = -> [Cylinder032,Cylinder033]
FEATURE [Part::MultiFuse] Fusion075  label="removeToCreteHoleForPlugHousing022"
  Placement = pos=(0,0,-28.3) rot=(0,0,1;0rad)
  Shapes = -> [Box022,Fusion076]
FEATURE [Part::MultiFuse] Fusion077  label="removeToCreatePlugHousingBottomBit"
  Shapes = -> [Fusion075,Fusion073]
FEATURE [Part::Cylinder] Cylinder034
  Angle = 360
  AttacherType = Attacher::AttachEngine3D
  Height = 20
  Placement = pos=(0,0,36.15) rot=(0,0,1;0rad)
  Radius = 14.3
FEATURE [Part::Cylinder] Cylinder035
  Angle = 360
  AttacherType = Attacher::AttachEngine3D
  Height = 10
  Placement = pos=(0,0,36.15) rot=(0,0,1;0rad)
  Radius = 4
FEATURE [Part::MultiFuse] Fusion078  label="removeToCreteHoleForPlugHousing024"
  Placement = pos=(70,19,36) rot=(0,1,0;1.5708rad)
  Shapes = -> [Cylinder034,Cylinder035]
FEATURE [Part::MultiFuse] Fusion079  label="removeToCreatePlugHousingBottomBit001"
  Shapes = -> [Fusion078,Fusion077]
FEATURE [Part::Extrusion] Extrude040  label="bottomPlugHousingBit"
  Base = -> Sketch049
  Dir = (0,0,1)
  DirMode = 2
  FaceMakerClass = Part::FaceMakerBullseye
  LengthFwd = 72
  LengthRev = 0
  Solid = true
  Symmetric = false
FEATURE [Part::Cut] Cut034  label="bottomPlugHousingBit001"
  Base = -> Extrude040
  Tool = -> Fusion079
